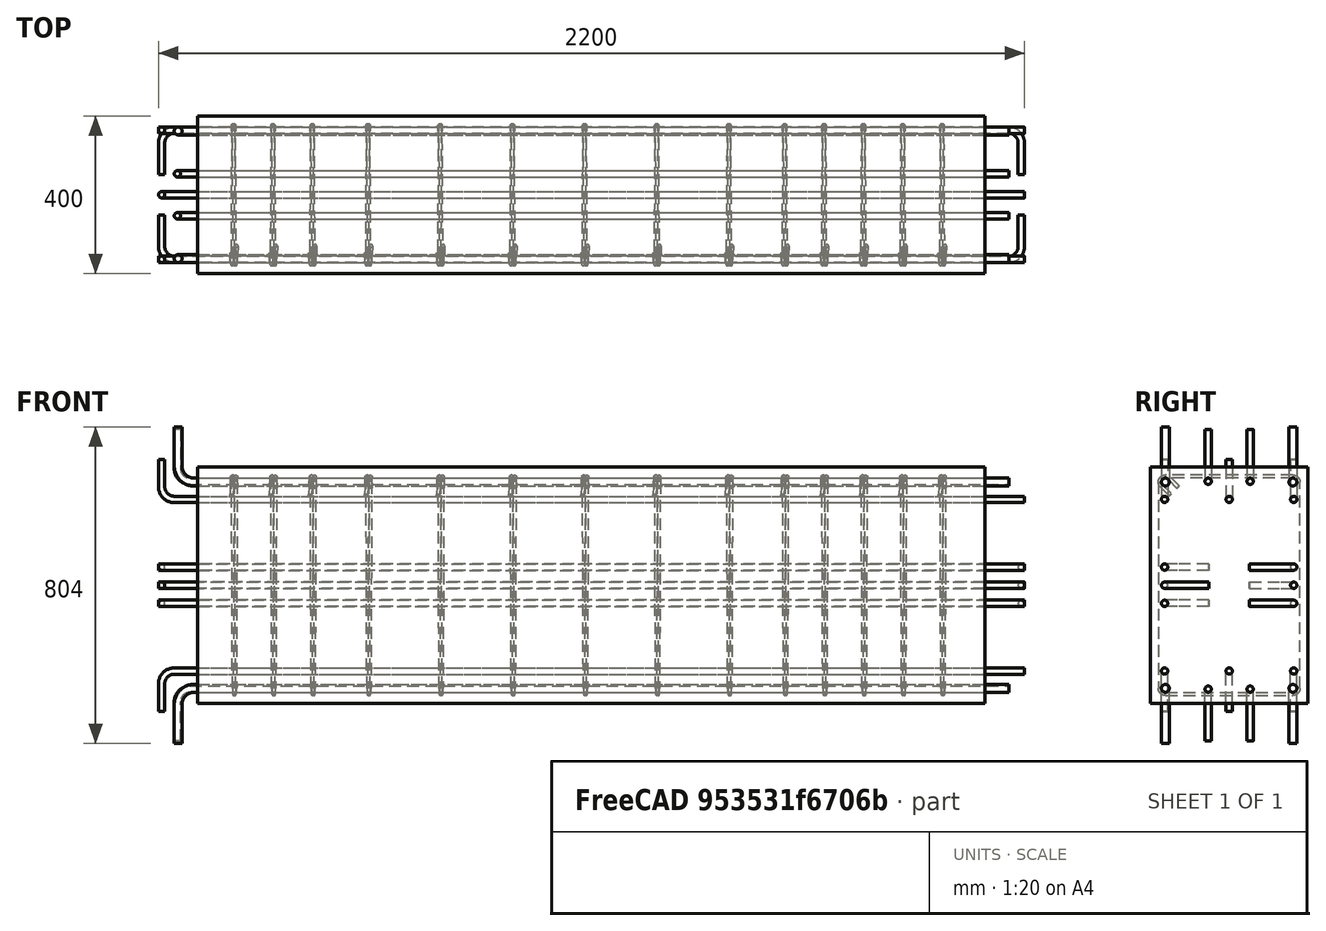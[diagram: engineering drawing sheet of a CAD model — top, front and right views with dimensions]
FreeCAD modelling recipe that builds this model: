
FCSTD DOCUMENT  (FreeCAD 0.19R20802 (Git))
Label: beam_drawing_dimension
License: All rights reserved
LicenseURL: http://en.wikipedia.org/wiki/All_rights_reserved
objects: TechDraw::DrawViewSymbolPython×88, Part::FeaturePython×16, Sketcher::SketchObject×14, App::DocumentObjectGroupPython×7, TechDraw::DrawSVGTemplate×6, TechDraw::DrawPage×6, Part::Part2DObjectPython×1
note: 31 computed .brp shape members not serialized (recipe doc carries the construction recipe); baked Part::Feature solids carry a one-line shape summary decoded from their .brp

FEATURE [Part::FeaturePython] Structure  label="Beam"  # Arch/BIM 7 (typed FeaturePython)
  FaceMaker = 0
  Height = 600
  HorizontalArea = 800000
  IfcData = attributes={"GlobalId": {"name": "GlobalId", "type": "IfcGloballyUniqueId", "is_enum": false, "enum_values": []}, "Description": {"... (+475 chars omitted),+1 more (map truncated)
  IfcType = 7
  Length = 2000
  MoveBase = false
  MoveWithHost = false
  Nodes = (2) [(0,0,1.11022e-15),(0,0,2000)]
  NodesOffset = 0
  Normal = (0,0,0)
  PerimeterLength = 4800
  PredefinedType = 0
  VerticalArea = 2880000
  Width = 400
FEATURE [Part::Part2DObjectPython] Wire  # Draft 2D object (typed FeaturePython)
  Area = 0
  ChamferSize = 0
  Closed = false
  End = (1989.44,-149.272,229.473)
  FilletRadius = 0
  Length = 1979.28
  MakeFace = true
  Points = (7) [(2002.11,-129.473,249.272),(2000,-176,295.799),(1997.89,-176,-276),(1995.78,176,-276),(1993.66,176,276),(1991.55,-195.799,276),(1989.44,-149.272,229.473)]
  Start = (2002.11,-129.473,249.272)
  Subdivisions = 0
  Support = -> [Structure]
FEATURE [Part::FeaturePython] Rebar  label="Stirrup"  # Arch/BIM 110 (typed FeaturePython)
  Amount = 14
  AmountCheck = false
  Base = -> Wire
  BentAngle = 135
  BentFactor = 4
  BottomCover = 20
  CustomSpacing = 5@100.0+6@183.33333333333334+3@100.0
  Diameter = 8
  Direction = (-1,0,0)
  Distance = 0
  FrontCover = 100
  HorizontalArea = 0
  Host = -> Structure
  IfcType = 110
  LeftCover = 20
  Length = 1979.28
  Mark = STRP
  MoveBase = false
  MoveWithHost = false
  OffsetEnd = 104
  OffsetStart = 104
  PerimeterLength = 0
  PlacementList = 14 placements: [(-104,0,0),(-204,0,0),(-304,0,0),(-404,0,0),(-504,0,0),(-645.667,0,0),(-829,0,0),(-1012.33,0,0),(-1195.67,0,0),(-1379,0,0),(-1562.33,0,0),(-1704,0,0),(-1804,0,0),(-1904,0,0)]
  RebarShape = 3
  RightCover = 20
  Rounding = 1.75
  Spacing = 0
  TopCover = 20
  TotalLength = 27710
  TrueSpacing = 100
  VerticalArea = 0
FEATURE [App::DocumentObjectGroupPython] Stirrups  # scripted group (container) (typed FeaturePython)
  Group = -> [Rebar]
  Stirrups = -> [Rebar]
  StirrupsConfiguration = Two Legged Stirrups
FEATURE [Sketcher::SketchObject] Sketch
  MapMode = 5
  Placement = pos=(0,-200,0) rot=(1,0,0;1.5708rad)
  Support = -> [Structure]
  sketch-geometry (2):
    g0: LineSegment StartX=-50 StartY=402 StartZ=0 EndX=-50 EndY=262 EndZ=0
    g1: LineSegment StartX=-50 StartY=262 StartZ=0 EndX=2060 EndY=262 EndZ=0
FEATURE [Part::FeaturePython] Rebar001  label="LShapeRebar"  # Arch/BIM 110 (typed FeaturePython)
  Amount = 1
  AmountCheck = true
  Base = -> Sketch
  BottomCover = 702
  Diameter = 20
  Direction = (0,0,0)
  Distance = 0
  FrontCover = 28
  HorizontalArea = 0
  Host = -> Structure
  IfcType = 110
  LeftCover = -60
  Length = 2250
  Mark = TLRb
  MoveBase = false
  MoveWithHost = false
  OffsetEnd = 38
  OffsetStart = 38
  Orientation = Top Left
  PerimeterLength = 0
  PlacementList = 1 placements: [(0,38,-8.43769e-15)]
  RebarShape = 2
  RightCover = -60
  Rounding = 2
  Spacing = 0
  TopCover = 28
  TotalLength = 2250
  TrueSpacing = 1
  VerticalArea = 0
FEATURE [Sketcher::SketchObject] Sketch001
  MapMode = 5
  Placement = pos=(0,-200,0) rot=(1,0,0;1.5708rad)
  Support = -> [Structure]
  sketch-geometry (2):
    g0: LineSegment StartX=-52 StartY=396 StartZ=0 EndX=-52 EndY=264 EndZ=0
    g1: LineSegment StartX=-52 StartY=264 StartZ=0 EndX=2060 EndY=264 EndZ=0
FEATURE [Part::FeaturePython] Rebar002  label="LShapeRebar001"  # Arch/BIM 110 (typed FeaturePython)
  Amount = 2
  AmountCheck = true
  Base = -> Sketch001
  BottomCover = 696
  Diameter = 16
  Direction = (0,0,0)
  Distance = 0
  FrontCover = 138.667
  HorizontalArea = 0
  Host = -> Structure
  IfcType = 110
  LeftCover = -60
  Length = 2244
  Mark = TLRb
  MoveBase = false
  MoveWithHost = false
  OffsetEnd = 146.667
  OffsetStart = 146.667
  Orientation = Top Left
  PerimeterLength = 0
  PlacementList = 2 placements: [(0,146.667,-3.25665e-14),(0,253.333,-5.62513e-14)]
  RebarShape = 2
  RightCover = -60
  Rounding = 2
  Spacing = 106.667
  TopCover = 28
  TotalLength = 4488
  TrueSpacing = 2
  VerticalArea = 0
FEATURE [Sketcher::SketchObject] Sketch002
  MapMode = 5
  Placement = pos=(0,-200,0) rot=(1,0,0;1.5708rad)
  Support = -> [Structure]
  sketch-geometry (2):
    g0: LineSegment StartX=-50 StartY=402 StartZ=0 EndX=-50 EndY=262 EndZ=0
    g1: LineSegment StartX=-50 StartY=262 StartZ=0 EndX=2060 EndY=262 EndZ=0
FEATURE [Part::FeaturePython] Rebar003  label="LShapeRebar002"  # Arch/BIM 110 (typed FeaturePython)
  Amount = 1
  AmountCheck = true
  Base = -> Sketch002
  BottomCover = 702
  Diameter = 20
  Direction = (0,0,0)
  Distance = 0
  FrontCover = 352
  HorizontalArea = 0
  Host = -> Structure
  IfcType = 110
  LeftCover = -60
  Length = 2250
  Mark = TLRb
  MoveBase = false
  MoveWithHost = false
  OffsetEnd = 362
  OffsetStart = 362
  Orientation = Top Left
  PerimeterLength = 0
  PlacementList = 1 placements: [(0,362,-8.03801e-14)]
  RebarShape = 2
  RightCover = -60
  Rounding = 2
  Spacing = 0
  TopCover = 28
  TotalLength = 2250
  TrueSpacing = 1
  VerticalArea = 0
FEATURE [Sketcher::SketchObject] Sketch003
  MapMode = 5
  Placement = pos=(0,-200,0) rot=(1,0,0;1.5708rad)
  Support = -> [Structure]
  sketch-geometry (2):
    g0: LineSegment StartX=-92 StartY=320 StartZ=0 EndX=-92 EndY=218 EndZ=0
    g1: LineSegment StartX=-92 StartY=218 StartZ=0 EndX=2100 EndY=218 EndZ=0
FEATURE [Part::FeaturePython] Rebar004  label="LShapeRebar003"  # Arch/BIM 110 (typed FeaturePython)
  Amount = 3
  AmountCheck = true
  Base = -> Sketch003
  BottomCover = 620
  Diameter = 16
  Direction = (0,0,0)
  Distance = 0
  FrontCover = 28
  HorizontalArea = 0
  Host = -> Structure
  IfcType = 110
  LeftCover = -100
  Length = 2294
  Mark = TLRb
  MoveBase = false
  MoveWithHost = false
  OffsetEnd = 36
  OffsetStart = 36
  Orientation = Top Left
  PerimeterLength = 0
  PlacementList = 3 placements: arithmetic series from (0,36,-7.99361e-15) step (0,164,-3.64153e-14) to (0,364,-8.08242e-14)
  RebarShape = 2
  RightCover = -100
  Rounding = 2
  Spacing = 164
  TopCover = 74
  TotalLength = 6882
  TrueSpacing = 3
  VerticalArea = 0
FEATURE [App::DocumentObjectGroupPython] TopReinforcement  # scripted group (container) (typed FeaturePython)
  Group = -> [Rebar001,Rebar002,Rebar003,Rebar004]
  HookExtension = [(100.0, 100.0, 100.0), (100.0,)]
  HookOrientation = [('Rear Outside', 'Rear Outside', 'Rear Outside'), ('Rear Outside',)]
  LRebarRounding = [(2, 2, 2), (2,)]
  LayerSpacing = [30,30]
  NumberDiameterOffset = 1#20@-60+2#16@-60+1#20@-60 | 3#16@-100
  RebarType = [('LShapeRebar', 'LShapeRebar', 'LShapeRebar'), ('LShapeRebar',)]
  TopRebars = -> [Rebar001,Rebar002,Rebar003,Rebar004]
FEATURE [Sketcher::SketchObject] Sketch004
  MapMode = 5
  Placement = pos=(0,-200,0) rot=(1,0,0;1.5708rad)
  Support = -> [Structure]
  sketch-geometry (2):
    g0: LineSegment StartX=-50 StartY=-402 StartZ=0 EndX=-50 EndY=-262 EndZ=0
    g1: LineSegment StartX=-50 StartY=-262 StartZ=0 EndX=2060 EndY=-262 EndZ=0
FEATURE [Part::FeaturePython] Rebar005  label="LShapeRebar004"  # Arch/BIM 110 (typed FeaturePython)
  Amount = 1
  AmountCheck = true
  Base = -> Sketch004
  BottomCover = 28
  Diameter = 20
  Direction = (0,0,0)
  Distance = 0
  FrontCover = 28
  HorizontalArea = 0
  Host = -> Structure
  IfcType = 110
  LeftCover = -60
  Length = 2250
  Mark = BLRb
  MoveBase = false
  MoveWithHost = false
  OffsetEnd = 38
  OffsetStart = 38
  Orientation = Bottom Left
  PerimeterLength = 0
  PlacementList = 1 placements: [(0,38,-8.43769e-15)]
  RebarShape = 2
  RightCover = -60
  Rounding = 2
  Spacing = 0
  TopCover = 702
  TotalLength = 2250
  TrueSpacing = 1
  VerticalArea = 0
FEATURE [Sketcher::SketchObject] Sketch005
  MapMode = 5
  Placement = pos=(0,-200,0) rot=(1,0,0;1.5708rad)
  Support = -> [Structure]
  sketch-geometry (2):
    g0: LineSegment StartX=-52 StartY=-396 StartZ=0 EndX=-52 EndY=-264 EndZ=0
    g1: LineSegment StartX=-52 StartY=-264 StartZ=0 EndX=2060 EndY=-264 EndZ=0
FEATURE [Part::FeaturePython] Rebar006  label="LShapeRebar005"  # Arch/BIM 110 (typed FeaturePython)
  Amount = 2
  AmountCheck = true
  Base = -> Sketch005
  BottomCover = 28
  Diameter = 16
  Direction = (0,0,0)
  Distance = 0
  FrontCover = 138.667
  HorizontalArea = 0
  Host = -> Structure
  IfcType = 110
  LeftCover = -60
  Length = 2244
  Mark = BLRb
  MoveBase = false
  MoveWithHost = false
  OffsetEnd = 146.667
  OffsetStart = 146.667
  Orientation = Bottom Left
  PerimeterLength = 0
  PlacementList = 2 placements: [(0,146.667,-3.25665e-14),(0,253.333,-5.62513e-14)]
  RebarShape = 2
  RightCover = -60
  Rounding = 2
  Spacing = 106.667
  TopCover = 696
  TotalLength = 4488
  TrueSpacing = 2
  VerticalArea = 0
FEATURE [Sketcher::SketchObject] Sketch006
  MapMode = 5
  Placement = pos=(0,-200,0) rot=(1,0,0;1.5708rad)
  Support = -> [Structure]
  sketch-geometry (2):
    g0: LineSegment StartX=-50 StartY=-402 StartZ=0 EndX=-50 EndY=-262 EndZ=0
    g1: LineSegment StartX=-50 StartY=-262 StartZ=0 EndX=2060 EndY=-262 EndZ=0
FEATURE [Part::FeaturePython] Rebar007  label="LShapeRebar006"  # Arch/BIM 110 (typed FeaturePython)
  Amount = 1
  AmountCheck = true
  Base = -> Sketch006
  BottomCover = 28
  Diameter = 20
  Direction = (0,0,0)
  Distance = 0
  FrontCover = 352
  HorizontalArea = 0
  Host = -> Structure
  IfcType = 110
  LeftCover = -60
  Length = 2250
  Mark = BLRb
  MoveBase = false
  MoveWithHost = false
  OffsetEnd = 362
  OffsetStart = 362
  Orientation = Bottom Left
  PerimeterLength = 0
  PlacementList = 1 placements: [(0,362,-8.03801e-14)]
  RebarShape = 2
  RightCover = -60
  Rounding = 2
  Spacing = 0
  TopCover = 702
  TotalLength = 2250
  TrueSpacing = 1
  VerticalArea = 0
FEATURE [Sketcher::SketchObject] Sketch007
  MapMode = 5
  Placement = pos=(0,-200,0) rot=(1,0,0;1.5708rad)
  Support = -> [Structure]
  sketch-geometry (2):
    g0: LineSegment StartX=-92 StartY=-320 StartZ=0 EndX=-92 EndY=-218 EndZ=0
    g1: LineSegment StartX=-92 StartY=-218 StartZ=0 EndX=2100 EndY=-218 EndZ=0
FEATURE [Part::FeaturePython] Rebar008  label="LShapeRebar007"  # Arch/BIM 110 (typed FeaturePython)
  Amount = 3
  AmountCheck = true
  Base = -> Sketch007
  BottomCover = 74
  Diameter = 16
  Direction = (0,0,0)
  Distance = 0
  FrontCover = 28
  HorizontalArea = 0
  Host = -> Structure
  IfcType = 110
  LeftCover = -100
  Length = 2294
  Mark = BLRb
  MoveBase = false
  MoveWithHost = false
  OffsetEnd = 36
  OffsetStart = 36
  Orientation = Bottom Left
  PerimeterLength = 0
  PlacementList = 3 placements: arithmetic series from (0,36,-7.99361e-15) step (0,164,-3.64153e-14) to (0,364,-8.08242e-14)
  RebarShape = 2
  RightCover = -100
  Rounding = 2
  Spacing = 164
  TopCover = 620
  TotalLength = 6882
  TrueSpacing = 3
  VerticalArea = 0
FEATURE [App::DocumentObjectGroupPython] BottomReinforcement  # scripted group (container) (typed FeaturePython)
  BottomRebars = -> [Rebar005,Rebar006,Rebar007,Rebar008]
  Group = -> [Rebar005,Rebar006,Rebar007,Rebar008]
  HookExtension = [(100.0, 100.0, 100.0), (100.0,)]
  HookOrientation = [('Rear Outside', 'Rear Outside', 'Rear Outside'), ('Rear Outside',)]
  LRebarRounding = [(2, 2, 2), (2,)]
  LayerSpacing = [30,30]
  NumberDiameterOffset = 1#20@-60+2#16@-60+1#20@-60 | 3#16@-100
  RebarType = [('LShapeRebar', 'LShapeRebar', 'LShapeRebar'), ('LShapeRebar',)]
FEATURE [Sketcher::SketchObject] Sketch008
  MapMode = 5
  Placement = pos=(6.6e-14,0,-300) rot=(1,0,0;3.14159rad)
  Support = -> [Structure]
  sketch-geometry (2):
    g0: LineSegment StartX=-92 StartY=52 StartZ=0 EndX=-92 EndY=164 EndZ=0
    g1: LineSegment StartX=-92 StartY=164 StartZ=0 EndX=2100 EndY=164 EndZ=0
FEATURE [Part::FeaturePython] Rebar009  label="LShapeRebar008"  # Arch/BIM 110 (typed FeaturePython)
  Amount = 1
  AmountCheck = true
  Base = -> Sketch008
  BottomCover = 252
  Diameter = 16
  Direction = (0,0,0)
  Distance = 0
  FrontCover = 246
  HorizontalArea = 0
  Host = -> Structure
  IfcType = 110
  LeftCover = -100
  Length = 2304
  Mark = LLRb
  MoveBase = false
  MoveWithHost = false
  OffsetEnd = 346
  OffsetStart = 254
  Orientation = Top Left
  PerimeterLength = 0
  PlacementList = 1 placements: [(-5.588e-14,0,254)]
  RebarShape = 2
  RightCover = -100
  Rounding = 2
  Spacing = 0
  TopCover = 28
  TotalLength = 2304
  TrueSpacing = 1
  VerticalArea = 0
FEATURE [Sketcher::SketchObject] Sketch009
  MapMode = 5
  Placement = pos=(6.6e-14,0,-300) rot=(1,0,0;3.14159rad)
  Support = -> [Structure]
  sketch-geometry (2):
    g0: LineSegment StartX=2092 StartY=52 StartZ=0 EndX=2092 EndY=164 EndZ=0
    g1: LineSegment StartX=2092 StartY=164 StartZ=0 EndX=-100 EndY=164 EndZ=0
FEATURE [Part::FeaturePython] Rebar010  label="LShapeRebar009"  # Arch/BIM 110 (typed FeaturePython)
  Amount = 1
  AmountCheck = true
  Base = -> Sketch009
  BottomCover = 252
  Diameter = 16
  Direction = (0,0,0)
  Distance = 0
  FrontCover = 292
  HorizontalArea = 0
  Host = -> Structure
  IfcType = 110
  LeftCover = -100
  Length = 2304
  Mark = LLRb
  MoveBase = false
  MoveWithHost = false
  OffsetEnd = 300
  OffsetStart = 300
  Orientation = Top Right
  PerimeterLength = 0
  PlacementList = 1 placements: [(-6.6e-14,0,300)]
  RebarShape = 2
  RightCover = -100
  Rounding = 2
  Spacing = 0
  TopCover = 28
  TotalLength = 2304
  TrueSpacing = 1
  VerticalArea = 0
FEATURE [Sketcher::SketchObject] Sketch010
  MapMode = 5
  Placement = pos=(6.6e-14,0,-300) rot=(1,0,0;3.14159rad)
  Support = -> [Structure]
  sketch-geometry (2):
    g0: LineSegment StartX=-92 StartY=52 StartZ=0 EndX=-92 EndY=164 EndZ=0
    g1: LineSegment StartX=-92 StartY=164 StartZ=0 EndX=2100 EndY=164 EndZ=0
FEATURE [Part::FeaturePython] Rebar011  label="LShapeRebar010"  # Arch/BIM 110 (typed FeaturePython)
  Amount = 1
  AmountCheck = true
  Base = -> Sketch010
  BottomCover = 252
  Diameter = 16
  Direction = (0,0,0)
  Distance = 0
  FrontCover = 338
  HorizontalArea = 0
  Host = -> Structure
  IfcType = 110
  LeftCover = -100
  Length = 2304
  Mark = LLRb
  MoveBase = false
  MoveWithHost = false
  OffsetEnd = 254
  OffsetStart = 346
  Orientation = Top Left
  PerimeterLength = 0
  PlacementList = 1 placements: [(-7.612e-14,0,346)]
  RebarShape = 2
  RightCover = -100
  Rounding = 2
  Spacing = 0
  TopCover = 28
  TotalLength = 2304
  TrueSpacing = 1
  VerticalArea = 0
FEATURE [App::DocumentObjectGroupPython] LeftRebars  # scripted group (container) (typed FeaturePython)
  Group = -> [Rebar009,Rebar010,Rebar011]
  HookExtension = [80,80,80]
  HookOrientation = Rear Inside | Front Inside | Rear Inside
  LRebarRounding = [2,2,2]
  LeftRebars = -> [Rebar009,Rebar010,Rebar011]
  NumberDiameterOffset = 1#16@-100+1#16@-100+1#16@-100
  RebarSpacing = 30
  RebarType = LShapeRebar | LShapeRebar | LShapeRebar
FEATURE [Sketcher::SketchObject] Sketch011
  MapMode = 5
  Placement = pos=(6.6e-14,0,-300) rot=(1,0,0;3.14159rad)
  Support = -> [Structure]
  sketch-geometry (2):
    g0: LineSegment StartX=2092 StartY=-52 StartZ=0 EndX=2092 EndY=-164 EndZ=0
    g1: LineSegment StartX=2092 StartY=-164 StartZ=0 EndX=-100 EndY=-164 EndZ=0
FEATURE [Part::FeaturePython] Rebar012  label="LShapeRebar011"  # Arch/BIM 110 (typed FeaturePython)
  Amount = 1
  AmountCheck = true
  Base = -> Sketch011
  BottomCover = 28
  Diameter = 16
  Direction = (0,0,0)
  Distance = 0
  FrontCover = 246
  HorizontalArea = 0
  Host = -> Structure
  IfcType = 110
  LeftCover = -100
  Length = 2304
  Mark = RLRb
  MoveBase = false
  MoveWithHost = false
  OffsetEnd = 346
  OffsetStart = 254
  Orientation = Bottom Right
  PerimeterLength = 0
  PlacementList = 1 placements: [(-5.588e-14,0,254)]
  RebarShape = 2
  RightCover = -100
  Rounding = 2
  Spacing = 0
  TopCover = 252
  TotalLength = 2304
  TrueSpacing = 1
  VerticalArea = 0
FEATURE [Sketcher::SketchObject] Sketch012
  MapMode = 5
  Placement = pos=(6.6e-14,0,-300) rot=(1,0,0;3.14159rad)
  Support = -> [Structure]
  sketch-geometry (2):
    g0: LineSegment StartX=-92 StartY=-52 StartZ=0 EndX=-92 EndY=-164 EndZ=0
    g1: LineSegment StartX=-92 StartY=-164 StartZ=0 EndX=2100 EndY=-164 EndZ=0
FEATURE [Part::FeaturePython] Rebar013  label="LShapeRebar012"  # Arch/BIM 110 (typed FeaturePython)
  Amount = 1
  AmountCheck = true
  Base = -> Sketch012
  BottomCover = 28
  Diameter = 16
  Direction = (0,0,0)
  Distance = 0
  FrontCover = 292
  HorizontalArea = 0
  Host = -> Structure
  IfcType = 110
  LeftCover = -100
  Length = 2304
  Mark = RLRb
  MoveBase = false
  MoveWithHost = false
  OffsetEnd = 300
  OffsetStart = 300
  Orientation = Bottom Left
  PerimeterLength = 0
  PlacementList = 1 placements: [(-6.6e-14,0,300)]
  RebarShape = 2
  RightCover = -100
  Rounding = 2
  Spacing = 0
  TopCover = 252
  TotalLength = 2304
  TrueSpacing = 1
  VerticalArea = 0
FEATURE [Sketcher::SketchObject] Sketch013
  MapMode = 5
  Placement = pos=(6.6e-14,0,-300) rot=(1,0,0;3.14159rad)
  Support = -> [Structure]
  sketch-geometry (2):
    g0: LineSegment StartX=2092 StartY=-52 StartZ=0 EndX=2092 EndY=-164 EndZ=0
    g1: LineSegment StartX=2092 StartY=-164 StartZ=0 EndX=-100 EndY=-164 EndZ=0
FEATURE [Part::FeaturePython] Rebar014  label="LShapeRebar013"  # Arch/BIM 110 (typed FeaturePython)
  Amount = 1
  AmountCheck = true
  Base = -> Sketch013
  BottomCover = 28
  Diameter = 16
  Direction = (0,0,0)
  Distance = 0
  FrontCover = 338
  HorizontalArea = 0
  Host = -> Structure
  IfcType = 110
  LeftCover = -100
  Length = 2304
  Mark = RLRb
  MoveBase = false
  MoveWithHost = false
  OffsetEnd = 254
  OffsetStart = 346
  Orientation = Bottom Right
  PerimeterLength = 0
  PlacementList = 1 placements: [(-7.612e-14,0,346)]
  RebarShape = 2
  RightCover = -100
  Rounding = 2
  Spacing = 0
  TopCover = 252
  TotalLength = 2304
  TrueSpacing = 1
  VerticalArea = 0
FEATURE [App::DocumentObjectGroupPython] RightRebars  # scripted group (container) (typed FeaturePython)
  Group = -> [Rebar012,Rebar013,Rebar014]
  HookExtension = [80,80,80]
  HookOrientation = Front Inside | Rear Inside | Front Inside
  LRebarRounding = [2,2,2]
  NumberDiameterOffset = 1#16@-100+1#16@-100+1#16@-100
  RebarSpacing = 30
  RebarType = LShapeRebar | LShapeRebar | LShapeRebar
  RightRebars = -> [Rebar012,Rebar013,Rebar014]
FEATURE [App::DocumentObjectGroupPython] ShearReinforcement  # scripted group (container) (typed FeaturePython)
  Group = -> [LeftRebars,RightRebars]
  ShearReinforcementGroups = -> [LeftRebars,RightRebars]
FEATURE [App::DocumentObjectGroupPython] BeamReinforcement  # scripted group (container) (typed FeaturePython)
  Group = -> [Stirrups,TopReinforcement,BottomReinforcement,ShearReinforcement]
  ReinforcementGroups = -> [Stirrups,TopReinforcement,BottomReinforcement,ShearReinforcement]
FEATURE [TechDraw::DrawSVGTemplate] Template
  Height = 210
  Orientation = 1
  Width = 297
FEATURE [TechDraw::DrawViewSymbolPython] ReinforcementDrawingView  label="Front View"  # drawing view (typed FeaturePython)
  DimensionBottomOffset = 40
  DimensionLeftOffset = 10
  DimensionRightOffset = 10
  DimensionTopOffset = 58
  Height = 804
  LeftOffset = 20
  LockPosition = false
  MaxHeight = 210
  MaxWidth = 297
  MinBottomOffset = 20
  MinRightOffset = 20
  PositionType = 0
  Rebars = -> [Rebar,Rebar001,Rebar002,Rebar003,Rebar004,Rebar005,Rebar006,Rebar007,Rebar008,Rebar009,Rebar010,Rebar011,Rebar012,Rebar013,Rebar014]
  RebarsColorStyle = 0
  RebarsStrokeWidth = 0.35
  Rotation = 0
  Scale = 0.116818
  ScaleType = 1
  Structure = -> Structure
  StructureColorStyle = 0
  StructureStrokeWidth = 0.5
  Symbol = <blob: 8325 chars omitted>
  Template = -> Template
  TopOffset = 58.0391
  View = 0
  VisibleRebars = -> [Rebar,Rebar001,Rebar002,Rebar004,Rebar005,Rebar006,Rebar008,Rebar009,Rebar010,Rebar011,Rebar012,Rebar013,Rebar014]
  Width = 2200
  X = 148.5
  Y = 105
  expr: TopOffset = .Template.Height.Value / 2 - .Height.Value * .Scale / 2
  expr: LeftOffset = .Template.Width.Value / 2 - .Width.Value * .Scale / 2
FEATURE [TechDraw::DrawViewSymbolPython] ReinforcementDimensioning  # drawing view (typed FeaturePython)
  DimensionBottomOffset = 10
  DimensionFormat = %M %C⌀%D,span=%S
  DimensionLeftOffset = 10
  DimensionRightOffset = 10
  DimensionTopOffset = 10
  Font = DejaVu Sans
  FontSize = 3
  LineEndSymbol = 0
  LineMidPointSymbol = 1
  LineStartSymbol = 3
  LineStyle = 0
  LockPosition = false
  MultiRebar_LineEndSymbol = 0
  MultiRebar_LineStartSymbol = 0
  MultiRebar_OuterDimension = true
  MultiRebar_TextPositionType = 0
  ParentDrawingView = -> ReinforcementDrawingView
  Rebar = -> Rebar
  Rotation = 0
  Scale = 0.116818
  ScaleType = 2
  SingleRebar_LineEndSymbol = 0
  SingleRebar_LineStartSymbol = 3
  SingleRebar_OuterDimension = false
  SingleRebar_TextPositionType = 1
  StrokeWidth = 0.25
  Symbol = <blob: 5914 chars omitted>
  TextPositionType = 0
  WayPoints = (2) [(0,0,0),(50,0,0)]
  WayPointsType = 0
  X = 148.5
  Y = 105
FEATURE [TechDraw::DrawViewSymbolPython] ReinforcementDimensioning001  # drawing view (typed FeaturePython)
  DimensionBottomOffset = 10
  DimensionFormat = %M %C⌀%D,span=%S
  DimensionLeftOffset = 10
  DimensionRightOffset = 10
  DimensionTopOffset = 16
  Font = DejaVu Sans
  FontSize = 3
  LineEndSymbol = 0
  LineMidPointSymbol = 1
  LineStartSymbol = 3
  LineStyle = 0
  LockPosition = false
  MultiRebar_LineEndSymbol = 0
  MultiRebar_LineStartSymbol = 0
  MultiRebar_OuterDimension = true
  MultiRebar_TextPositionType = 0
  ParentDrawingView = -> ReinforcementDrawingView
  Rebar = -> Rebar001
  Rotation = 0
  Scale = 0.116818
  ScaleType = 2
  SingleRebar_LineEndSymbol = 0
  SingleRebar_LineStartSymbol = 3
  SingleRebar_OuterDimension = false
  SingleRebar_TextPositionType = 1
  StrokeWidth = 0.25
  Symbol = <svg version="1.1" xmlns="http://www.w3.org/2000/svg" xmlns:xlink="http://www.w3.org/1999/xlink" xmlns:freecad="http://www.freecadweb.org/wiki/index.php?title=Svg_Namespace" width="2200.0mm" height="804.0mm" viewBox="0 0 2200.0 804.0"><g transform="translate(100.00000000000023, 402.0000000000002)"><g><path d="M1197.0 -538.9649805447473 L1197.0 -262.0000000000002" style="stroke:#00007f;stroke-width:2.140077821011673;stroke-linecap:round;fill:none;" stroke-dasharray="" /><g id="line_mid_points" /><path d="M0,0 -8,-1.5 V1.5 L0,0" style="stroke:#00007f;fill:#00007f;stroke-width:2.140077821011673;stroke-linecap:round;stroke-linejoin:bevel;" transform="translate(1197.0 -262.0000000000002) rotate(90.0 0 0)" /></g><text x="1197.0" y="-538.9649805447473" style="white-space:pre;" fill="#005400" font-family="DejaVu Sans" font-size="25.68093385214008" text-anchor="middle" dominant-baseline="baseline" xml:space="preserve">TLRb 1⌀20,span=0</text></g></svg>
  TextPositionType = 0
  WayPoints = (2) [(0,0,0),(50,0,0)]
  WayPointsType = 0
  X = 148.5
  Y = 105
FEATURE [TechDraw::DrawViewSymbolPython] ReinforcementDimensioning002  # drawing view (typed FeaturePython)
  DimensionBottomOffset = 10
  DimensionFormat = %M %C⌀%D,span=%S
  DimensionLeftOffset = 10
  DimensionRightOffset = 10
  DimensionTopOffset = 22
  Font = DejaVu Sans
  FontSize = 3
  LineEndSymbol = 0
  LineMidPointSymbol = 1
  LineStartSymbol = 3
  LineStyle = 0
  LockPosition = false
  MultiRebar_LineEndSymbol = 0
  MultiRebar_LineStartSymbol = 0
  MultiRebar_OuterDimension = true
  MultiRebar_TextPositionType = 0
  ParentDrawingView = -> ReinforcementDrawingView
  Rebar = -> Rebar002
  Rotation = 0
  Scale = 0.116818
  ScaleType = 2
  SingleRebar_LineEndSymbol = 0
  SingleRebar_LineStartSymbol = 3
  SingleRebar_OuterDimension = false
  SingleRebar_TextPositionType = 1
  StrokeWidth = 0.25
  Symbol = <svg version="1.1" xmlns="http://www.w3.org/2000/svg" xmlns:xlink="http://www.w3.org/1999/xlink" xmlns:freecad="http://www.freecadweb.org/wiki/index.php?title=Svg_Namespace" width="2200.0mm" height="804.0mm" viewBox="0 0 2200.0 804.0"><g transform="translate(100.00000000000023, 402.0000000000002)"><g><path d="M1213.0 -590.3268482490274 L1213.0 -264.00000000000017" style="stroke:#00007f;stroke-width:2.140077821011673;stroke-linecap:round;fill:none;" stroke-dasharray="" /><g id="line_mid_points" /><path d="M0,0 -8,-1.5 V1.5 L0,0" style="stroke:#00007f;fill:#00007f;stroke-width:2.140077821011673;stroke-linecap:round;stroke-linejoin:bevel;" transform="translate(1213.0 -264.00000000000017) rotate(90.0 0 0)" /></g><text x="1213.0" y="-590.3268482490274" style="white-space:pre;" fill="#005400" font-family="DejaVu Sans" font-size="25.68093385214008" text-anchor="middle" dominant-baseline="baseline" xml:space="preserve">TLRb 2⌀16,span=107</text></g></svg>
  TextPositionType = 0
  WayPoints = (2) [(0,0,0),(50,0,0)]
  WayPointsType = 0
  X = 148.5
  Y = 105
FEATURE [TechDraw::DrawViewSymbolPython] ReinforcementDimensioning003  # drawing view (typed FeaturePython)
  DimensionBottomOffset = 10
  DimensionFormat = %M %C⌀%D,span=%S
  DimensionLeftOffset = 10
  DimensionRightOffset = 10
  DimensionTopOffset = 28
  Font = DejaVu Sans
  FontSize = 3
  LineEndSymbol = 0
  LineMidPointSymbol = 1
  LineStartSymbol = 3
  LineStyle = 0
  LockPosition = false
  MultiRebar_LineEndSymbol = 0
  MultiRebar_LineStartSymbol = 0
  MultiRebar_OuterDimension = true
  MultiRebar_TextPositionType = 0
  ParentDrawingView = -> ReinforcementDrawingView
  Rebar = -> Rebar004
  Rotation = 0
  Scale = 0.116818
  ScaleType = 2
  SingleRebar_LineEndSymbol = 0
  SingleRebar_LineStartSymbol = 3
  SingleRebar_OuterDimension = false
  SingleRebar_TextPositionType = 1
  StrokeWidth = 0.25
  Symbol = <svg version="1.1" xmlns="http://www.w3.org/2000/svg" xmlns:xlink="http://www.w3.org/1999/xlink" xmlns:freecad="http://www.freecadweb.org/wiki/index.php?title=Svg_Namespace" width="2200.0mm" height="804.0mm" viewBox="0 0 2200.0 804.0"><g transform="translate(100.00000000000023, 402.0000000000002)"><g><path d="M1938.0 -641.6887159533076 L1938.0 -218.00000000000023" style="stroke:#00007f;stroke-width:2.140077821011673;stroke-linecap:round;fill:none;" stroke-dasharray="" /><g id="line_mid_points" /><path d="M0,0 -8,-1.5 V1.5 L0,0" style="stroke:#00007f;fill:#00007f;stroke-width:2.140077821011673;stroke-linecap:round;stroke-linejoin:bevel;" transform="translate(1938.0 -218.00000000000023) rotate(90.0 0 0)" /></g><text x="1938.0" y="-641.6887159533076" style="white-space:pre;" fill="#005400" font-family="DejaVu Sans" font-size="25.68093385214008" text-anchor="middle" dominant-baseline="baseline" xml:space="preserve">TLRb 3⌀16,span=328</text></g></svg>
  TextPositionType = 0
  WayPoints = (2) [(0,0,0),(50,0,0)]
  WayPointsType = 0
  X = 148.5
  Y = 105
FEATURE [TechDraw::DrawViewSymbolPython] ReinforcementDimensioning004  # drawing view (typed FeaturePython)
  DimensionBottomOffset = 10
  DimensionFormat = %M %C⌀%D,span=%S
  DimensionLeftOffset = 10
  DimensionRightOffset = 10
  DimensionTopOffset = 34
  Font = DejaVu Sans
  FontSize = 3
  LineEndSymbol = 0
  LineMidPointSymbol = 1
  LineStartSymbol = 3
  LineStyle = 0
  LockPosition = false
  MultiRebar_LineEndSymbol = 0
  MultiRebar_LineStartSymbol = 0
  MultiRebar_OuterDimension = true
  MultiRebar_TextPositionType = 0
  ParentDrawingView = -> ReinforcementDrawingView
  Rebar = -> Rebar005
  Rotation = 0
  Scale = 0.116818
  ScaleType = 2
  SingleRebar_LineEndSymbol = 0
  SingleRebar_LineStartSymbol = 3
  SingleRebar_OuterDimension = false
  SingleRebar_TextPositionType = 1
  StrokeWidth = 0.25
  Symbol = <svg version="1.1" xmlns="http://www.w3.org/2000/svg" xmlns:xlink="http://www.w3.org/1999/xlink" xmlns:freecad="http://www.freecadweb.org/wiki/index.php?title=Svg_Namespace" width="2200.0mm" height="804.0mm" viewBox="0 0 2200.0 804.0"><g transform="translate(100.00000000000023, 402.0000000000002)"><g><path d="M319.0 487.60311284046674 L319.0 261.9999999999998" style="stroke:#00007f;stroke-width:2.140077821011673;stroke-linecap:round;fill:none;" stroke-dasharray="" /><g id="line_mid_points" /><path d="M0,0 -8,-1.5 V1.5 L0,0" style="stroke:#00007f;fill:#00007f;stroke-width:2.140077821011673;stroke-linecap:round;stroke-linejoin:bevel;" transform="translate(319.0 261.9999999999998) rotate(-90.0 0 0)" /></g><text x="319.0" y="500.4435797665368" style="white-space:pre;" fill="#005400" font-family="DejaVu Sans" font-size="25.68093385214008" text-anchor="middle" dominant-baseline="baseline" xml:space="preserve">BLRb 1⌀20,span=0</text></g></svg>
  TextPositionType = 0
  WayPoints = (2) [(0,0,0),(50,0,0)]
  WayPointsType = 0
  X = 148.5
  Y = 105
FEATURE [TechDraw::DrawViewSymbolPython] ReinforcementDimensioning005  # drawing view (typed FeaturePython)
  DimensionBottomOffset = 16
  DimensionFormat = %M %C⌀%D,span=%S
  DimensionLeftOffset = 10
  DimensionRightOffset = 10
  DimensionTopOffset = 34
  Font = DejaVu Sans
  FontSize = 3
  LineEndSymbol = 0
  LineMidPointSymbol = 1
  LineStartSymbol = 3
  LineStyle = 0
  LockPosition = false
  MultiRebar_LineEndSymbol = 0
  MultiRebar_LineStartSymbol = 0
  MultiRebar_OuterDimension = true
  MultiRebar_TextPositionType = 0
  ParentDrawingView = -> ReinforcementDrawingView
  Rebar = -> Rebar006
  Rotation = 0
  Scale = 0.116818
  ScaleType = 2
  SingleRebar_LineEndSymbol = 0
  SingleRebar_LineStartSymbol = 3
  SingleRebar_OuterDimension = false
  SingleRebar_TextPositionType = 1
  StrokeWidth = 0.25
  Symbol = <svg version="1.1" xmlns="http://www.w3.org/2000/svg" xmlns:xlink="http://www.w3.org/1999/xlink" xmlns:freecad="http://www.freecadweb.org/wiki/index.php?title=Svg_Namespace" width="2200.0mm" height="804.0mm" viewBox="0 0 2200.0 804.0"><g transform="translate(100.00000000000023, 402.0000000000002)"><g><path d="M1466.0 538.9649805447469 L1466.0 263.99999999999983" style="stroke:#00007f;stroke-width:2.140077821011673;stroke-linecap:round;fill:none;" stroke-dasharray="" /><g id="line_mid_points" /><path d="M0,0 -8,-1.5 V1.5 L0,0" style="stroke:#00007f;fill:#00007f;stroke-width:2.140077821011673;stroke-linecap:round;stroke-linejoin:bevel;" transform="translate(1466.0 263.99999999999983) rotate(-90.0 0 0)" /></g><text x="1466.0" y="551.805447470817" style="white-space:pre;" fill="#005400" font-family="DejaVu Sans" font-size="25.68093385214008" text-anchor="middle" dominant-baseline="baseline" xml:space="preserve">BLRb 2⌀16,span=107</text></g></svg>
  TextPositionType = 0
  WayPoints = (2) [(0,0,0),(50,0,0)]
  WayPointsType = 0
  X = 148.5
  Y = 105
FEATURE [TechDraw::DrawViewSymbolPython] ReinforcementDimensioning006  # drawing view (typed FeaturePython)
  DimensionBottomOffset = 22
  DimensionFormat = %M %C⌀%D,span=%S
  DimensionLeftOffset = 10
  DimensionRightOffset = 10
  DimensionTopOffset = 34
  Font = DejaVu Sans
  FontSize = 3
  LineEndSymbol = 0
  LineMidPointSymbol = 1
  LineStartSymbol = 3
  LineStyle = 0
  LockPosition = false
  MultiRebar_LineEndSymbol = 0
  MultiRebar_LineStartSymbol = 0
  MultiRebar_OuterDimension = true
  MultiRebar_TextPositionType = 0
  ParentDrawingView = -> ReinforcementDrawingView
  Rebar = -> Rebar008
  Rotation = 0
  Scale = 0.116818
  ScaleType = 2
  SingleRebar_LineEndSymbol = 0
  SingleRebar_LineStartSymbol = 3
  SingleRebar_OuterDimension = false
  SingleRebar_TextPositionType = 1
  StrokeWidth = 0.25
  Symbol = <svg version="1.1" xmlns="http://www.w3.org/2000/svg" xmlns:xlink="http://www.w3.org/1999/xlink" xmlns:freecad="http://www.freecadweb.org/wiki/index.php?title=Svg_Namespace" width="2200.0mm" height="804.0mm" viewBox="0 0 2200.0 804.0"><g transform="translate(100.00000000000023, 402.0000000000002)"><g><path d="M1960.0 590.3268482490271 L1960.0 217.99999999999977" style="stroke:#00007f;stroke-width:2.140077821011673;stroke-linecap:round;fill:none;" stroke-dasharray="" /><g id="line_mid_points" /><path d="M0,0 -8,-1.5 V1.5 L0,0" style="stroke:#00007f;fill:#00007f;stroke-width:2.140077821011673;stroke-linecap:round;stroke-linejoin:bevel;" transform="translate(1960.0 217.99999999999977) rotate(-90.0 0 0)" /></g><text x="1960.0" y="603.1673151750971" style="white-space:pre;" fill="#005400" font-family="DejaVu Sans" font-size="25.68093385214008" text-anchor="middle" dominant-baseline="baseline" xml:space="preserve">BLRb 3⌀16,span=328</text></g></svg>
  TextPositionType = 0
  WayPoints = (2) [(0,0,0),(50,0,0)]
  WayPointsType = 0
  X = 148.5
  Y = 105
FEATURE [TechDraw::DrawViewSymbolPython] ReinforcementDimensioning007  # drawing view (typed FeaturePython)
  DimensionBottomOffset = 28
  DimensionFormat = %M %C⌀%D,span=%S
  DimensionLeftOffset = 10
  DimensionRightOffset = 10
  DimensionTopOffset = 34
  Font = DejaVu Sans
  FontSize = 3
  LineEndSymbol = 0
  LineMidPointSymbol = 1
  LineStartSymbol = 3
  LineStyle = 0
  LockPosition = false
  MultiRebar_LineEndSymbol = 0
  MultiRebar_LineStartSymbol = 0
  MultiRebar_OuterDimension = true
  MultiRebar_TextPositionType = 0
  ParentDrawingView = -> ReinforcementDrawingView
  Rebar = -> Rebar009
  Rotation = 0
  Scale = 0.116818
  ScaleType = 2
  SingleRebar_LineEndSymbol = 0
  SingleRebar_LineStartSymbol = 3
  SingleRebar_OuterDimension = false
  SingleRebar_TextPositionType = 1
  StrokeWidth = 0.25
  Symbol = <svg version="1.1" xmlns="http://www.w3.org/2000/svg" xmlns:xlink="http://www.w3.org/1999/xlink" xmlns:freecad="http://www.freecadweb.org/wiki/index.php?title=Svg_Namespace" width="2200.0mm" height="804.0mm" viewBox="0 0 2200.0 804.0"><g transform="translate(100.00000000000023, 402.0000000000002)"><g><path d="M18.0 641.6887159533072 L18.0 45.99999999999998" style="stroke:#00007f;stroke-width:2.140077821011673;stroke-linecap:round;fill:none;" stroke-dasharray="" /><g id="line_mid_points" /><path d="M0,0 -8,-1.5 V1.5 L0,0" style="stroke:#00007f;fill:#00007f;stroke-width:2.140077821011673;stroke-linecap:round;stroke-linejoin:bevel;" transform="translate(18.0 45.99999999999998) rotate(-90.0 0 0)" /></g><text x="18.0" y="654.5291828793772" style="white-space:pre;" fill="#005400" font-family="DejaVu Sans" font-size="25.68093385214008" text-anchor="middle" dominant-baseline="baseline" xml:space="preserve">LLRb 1⌀16,span=0</text></g></svg>
  TextPositionType = 0
  WayPoints = (2) [(0,0,0),(50,0,0)]
  WayPointsType = 0
  X = 148.5
  Y = 105
FEATURE [TechDraw::DrawViewSymbolPython] ReinforcementDimensioning008  # drawing view (typed FeaturePython)
  DimensionBottomOffset = 34
  DimensionFormat = %M %C⌀%D,span=%S
  DimensionLeftOffset = 10
  DimensionRightOffset = 10
  DimensionTopOffset = 34
  Font = DejaVu Sans
  FontSize = 3
  LineEndSymbol = 0
  LineMidPointSymbol = 1
  LineStartSymbol = 3
  LineStyle = 0
  LockPosition = false
  MultiRebar_LineEndSymbol = 0
  MultiRebar_LineStartSymbol = 0
  MultiRebar_OuterDimension = true
  MultiRebar_TextPositionType = 0
  ParentDrawingView = -> ReinforcementDrawingView
  Rebar = -> Rebar010
  Rotation = 0
  Scale = 0.116818
  ScaleType = 2
  SingleRebar_LineEndSymbol = 0
  SingleRebar_LineStartSymbol = 3
  SingleRebar_OuterDimension = false
  SingleRebar_TextPositionType = 1
  StrokeWidth = 0.25
  Symbol = <svg version="1.1" xmlns="http://www.w3.org/2000/svg" xmlns:xlink="http://www.w3.org/1999/xlink" xmlns:freecad="http://www.freecadweb.org/wiki/index.php?title=Svg_Namespace" width="2200.0mm" height="804.0mm" viewBox="0 0 2200.0 804.0"><g transform="translate(100.00000000000023, 402.0000000000002)"><g><path d="M809.0 -693.0505836575878 L809.0 -1.8857907935939593e-13" style="stroke:#00007f;stroke-width:2.140077821011673;stroke-linecap:round;fill:none;" stroke-dasharray="" /><g id="line_mid_points" /><path d="M0,0 -8,-1.5 V1.5 L0,0" style="stroke:#00007f;fill:#00007f;stroke-width:2.140077821011673;stroke-linecap:round;stroke-linejoin:bevel;" transform="translate(809.0 -1.8857907935939593e-13) rotate(90.0 0 0)" /></g><text x="809.0" y="-693.0505836575878" style="white-space:pre;" fill="#005400" font-family="DejaVu Sans" font-size="25.68093385214008" text-anchor="middle" dominant-baseline="baseline" xml:space="preserve">LLRb 1⌀16,span=0</text></g></svg>
  TextPositionType = 0
  WayPoints = (2) [(0,0,0),(50,0,0)]
  WayPointsType = 0
  X = 148.5
  Y = 105
FEATURE [TechDraw::DrawViewSymbolPython] ReinforcementDimensioning009  # drawing view (typed FeaturePython)
  DimensionBottomOffset = 34
  DimensionFormat = %M %C⌀%D,span=%S
  DimensionLeftOffset = 10
  DimensionRightOffset = 10
  DimensionTopOffset = 40
  Font = DejaVu Sans
  FontSize = 3
  LineEndSymbol = 0
  LineMidPointSymbol = 1
  LineStartSymbol = 3
  LineStyle = 0
  LockPosition = false
  MultiRebar_LineEndSymbol = 0
  MultiRebar_LineStartSymbol = 0
  MultiRebar_OuterDimension = true
  MultiRebar_TextPositionType = 0
  ParentDrawingView = -> ReinforcementDrawingView
  Rebar = -> Rebar011
  Rotation = 0
  Scale = 0.116818
  ScaleType = 2
  SingleRebar_LineEndSymbol = 0
  SingleRebar_LineStartSymbol = 3
  SingleRebar_OuterDimension = false
  SingleRebar_TextPositionType = 1
  StrokeWidth = 0.25
  Symbol = <svg version="1.1" xmlns="http://www.w3.org/2000/svg" xmlns:xlink="http://www.w3.org/1999/xlink" xmlns:freecad="http://www.freecadweb.org/wiki/index.php?title=Svg_Namespace" width="2200.0mm" height="804.0mm" viewBox="0 0 2200.0 804.0"><g transform="translate(100.00000000000023, 402.0000000000002)"><g><path d="M1230.0 -744.4124513618679 L1230.0 -46.00000000000028" style="stroke:#00007f;stroke-width:2.140077821011673;stroke-linecap:round;fill:none;" stroke-dasharray="" /><g id="line_mid_points" /><path d="M0,0 -8,-1.5 V1.5 L0,0" style="stroke:#00007f;fill:#00007f;stroke-width:2.140077821011673;stroke-linecap:round;stroke-linejoin:bevel;" transform="translate(1230.0 -46.00000000000028) rotate(90.0 0 0)" /></g><text x="1230.0" y="-744.4124513618679" style="white-space:pre;" fill="#005400" font-family="DejaVu Sans" font-size="25.68093385214008" text-anchor="middle" dominant-baseline="baseline" xml:space="preserve">LLRb 1⌀16,span=0</text></g></svg>
  TextPositionType = 0
  WayPoints = (2) [(0,0,0),(50,0,0)]
  WayPointsType = 0
  X = 148.5
  Y = 105
FEATURE [TechDraw::DrawViewSymbolPython] ReinforcementDimensioning010  # drawing view (typed FeaturePython)
  DimensionBottomOffset = 34
  DimensionFormat = %M %C⌀%D,span=%S
  DimensionLeftOffset = 10
  DimensionRightOffset = 10
  DimensionTopOffset = 46
  Font = DejaVu Sans
  FontSize = 3
  LineEndSymbol = 0
  LineMidPointSymbol = 1
  LineStartSymbol = 3
  LineStyle = 0
  LockPosition = false
  MultiRebar_LineEndSymbol = 0
  MultiRebar_LineStartSymbol = 0
  MultiRebar_OuterDimension = true
  MultiRebar_TextPositionType = 0
  ParentDrawingView = -> ReinforcementDrawingView
  Rebar = -> Rebar012
  Rotation = 0
  Scale = 0.116818
  ScaleType = 2
  SingleRebar_LineEndSymbol = 0
  SingleRebar_LineStartSymbol = 3
  SingleRebar_OuterDimension = false
  SingleRebar_TextPositionType = 1
  StrokeWidth = 0.25
  Symbol = <svg version="1.1" xmlns="http://www.w3.org/2000/svg" xmlns:xlink="http://www.w3.org/1999/xlink" xmlns:freecad="http://www.freecadweb.org/wiki/index.php?title=Svg_Namespace" width="2200.0mm" height="804.0mm" viewBox="0 0 2200.0 804.0"><g transform="translate(100.00000000000023, 402.0000000000002)"><g><path d="M536.0 693.0505836575874 L536.0 45.999999999999865" style="stroke:#00007f;stroke-width:2.140077821011673;stroke-linecap:round;fill:none;" stroke-dasharray="" /><g id="line_mid_points" /><path d="M0,0 -8,-1.5 V1.5 L0,0" style="stroke:#00007f;fill:#00007f;stroke-width:2.140077821011673;stroke-linecap:round;stroke-linejoin:bevel;" transform="translate(536.0 45.999999999999865) rotate(-90.0 0 0)" /></g><text x="536.0" y="705.8910505836574" style="white-space:pre;" fill="#005400" font-family="DejaVu Sans" font-size="25.68093385214008" text-anchor="middle" dominant-baseline="baseline" xml:space="preserve">RLRb 1⌀16,span=0</text></g></svg>
  TextPositionType = 0
  WayPoints = (2) [(0,0,0),(50,0,0)]
  WayPointsType = 0
  X = 148.5
  Y = 105
FEATURE [TechDraw::DrawViewSymbolPython] ReinforcementDimensioning011  # drawing view (typed FeaturePython)
  DimensionBottomOffset = 40
  DimensionFormat = %M %C⌀%D,span=%S
  DimensionLeftOffset = 10
  DimensionRightOffset = 10
  DimensionTopOffset = 46
  Font = DejaVu Sans
  FontSize = 3
  LineEndSymbol = 0
  LineMidPointSymbol = 1
  LineStartSymbol = 3
  LineStyle = 0
  LockPosition = false
  MultiRebar_LineEndSymbol = 0
  MultiRebar_LineStartSymbol = 0
  MultiRebar_OuterDimension = true
  MultiRebar_TextPositionType = 0
  ParentDrawingView = -> ReinforcementDrawingView
  Rebar = -> Rebar013
  Rotation = 0
  Scale = 0.116818
  ScaleType = 2
  SingleRebar_LineEndSymbol = 0
  SingleRebar_LineStartSymbol = 3
  SingleRebar_OuterDimension = false
  SingleRebar_TextPositionType = 1
  StrokeWidth = 0.25
  Symbol = <svg version="1.1" xmlns="http://www.w3.org/2000/svg" xmlns:xlink="http://www.w3.org/1999/xlink" xmlns:freecad="http://www.freecadweb.org/wiki/index.php?title=Svg_Namespace" width="2200.0mm" height="804.0mm" viewBox="0 0 2200.0 804.0"><g transform="translate(100.00000000000023, 402.0000000000002)"><g><path d="M241.0 -795.7743190661481 L241.0 -6.90834251118579e-14" style="stroke:#00007f;stroke-width:2.140077821011673;stroke-linecap:round;fill:none;" stroke-dasharray="" /><g id="line_mid_points" /><path d="M0,0 -8,-1.5 V1.5 L0,0" style="stroke:#00007f;fill:#00007f;stroke-width:2.140077821011673;stroke-linecap:round;stroke-linejoin:bevel;" transform="translate(241.0 -6.90834251118579e-14) rotate(90.0 0 0)" /></g><text x="241.0" y="-795.7743190661481" style="white-space:pre;" fill="#005400" font-family="DejaVu Sans" font-size="25.68093385214008" text-anchor="middle" dominant-baseline="baseline" xml:space="preserve">RLRb 1⌀16,span=0</text></g></svg>
  TextPositionType = 0
  WayPoints = (2) [(0,0,0),(50,0,0)]
  WayPointsType = 0
  X = 148.5
  Y = 105
FEATURE [TechDraw::DrawViewSymbolPython] ReinforcementDimensioning012  # drawing view (typed FeaturePython)
  DimensionBottomOffset = 40
  DimensionFormat = %M %C⌀%D,span=%S
  DimensionLeftOffset = 10
  DimensionRightOffset = 10
  DimensionTopOffset = 52
  Font = DejaVu Sans
  FontSize = 3
  LineEndSymbol = 0
  LineMidPointSymbol = 1
  LineStartSymbol = 3
  LineStyle = 0
  LockPosition = false
  MultiRebar_LineEndSymbol = 0
  MultiRebar_LineStartSymbol = 0
  MultiRebar_OuterDimension = true
  MultiRebar_TextPositionType = 0
  ParentDrawingView = -> ReinforcementDrawingView
  Rebar = -> Rebar014
  Rotation = 0
  Scale = 0.116818
  ScaleType = 2
  SingleRebar_LineEndSymbol = 0
  SingleRebar_LineStartSymbol = 3
  SingleRebar_OuterDimension = false
  SingleRebar_TextPositionType = 1
  StrokeWidth = 0.25
  Symbol = <svg version="1.1" xmlns="http://www.w3.org/2000/svg" xmlns:xlink="http://www.w3.org/1999/xlink" xmlns:freecad="http://www.freecadweb.org/wiki/index.php?title=Svg_Namespace" width="2200.0mm" height="804.0mm" viewBox="0 0 2200.0 804.0"><g transform="translate(100.00000000000023, 402.0000000000002)"><g><path d="M728.0 -847.1361867704283 L728.0 -46.00000000000017" style="stroke:#00007f;stroke-width:2.140077821011673;stroke-linecap:round;fill:none;" stroke-dasharray="" /><g id="line_mid_points" /><path d="M0,0 -8,-1.5 V1.5 L0,0" style="stroke:#00007f;fill:#00007f;stroke-width:2.140077821011673;stroke-linecap:round;stroke-linejoin:bevel;" transform="translate(728.0 -46.00000000000017) rotate(90.0 0 0)" /></g><text x="728.0" y="-847.1361867704283" style="white-space:pre;" fill="#005400" font-family="DejaVu Sans" font-size="25.68093385214008" text-anchor="middle" dominant-baseline="baseline" xml:space="preserve">RLRb 1⌀16,span=0</text></g></svg>
  TextPositionType = 0
  WayPoints = (2) [(0,0,0),(50,0,0)]
  WayPointsType = 0
  X = 148.5
  Y = 105
FEATURE [TechDraw::DrawPage] TechDraw__DrawPage  label="Beam Drawing"
  KeepUpdated = true
  NextBalloonIndex = 1
  ProjectionType = 0
  Template = -> Template
  Views = -> [ReinforcementDrawingView,ReinforcementDimensioning,ReinforcementDimensioning001,ReinforcementDimensioning002,ReinforcementDimensioning003,ReinforcementDimensioning004,ReinforcementDimensioning005,ReinforcementDimensioning006,ReinforcementDimensioning007,ReinforcementDimensioning008,ReinforcementDimensioning009,ReinforcementDimensioning010,ReinforcementDimensioning011,ReinforcementDimensioning012]
FEATURE [TechDraw::DrawSVGTemplate] Template001
  Height = 210
  Orientation = 1
  Width = 297
FEATURE [TechDraw::DrawViewSymbolPython] ReinforcementDrawingView001  label="Rear View"  # drawing view (typed FeaturePython)
  DimensionBottomOffset = 40
  DimensionLeftOffset = 10
  DimensionRightOffset = 10
  DimensionTopOffset = 58
  Height = 804
  LeftOffset = 20
  LockPosition = false
  MaxHeight = 210
  MaxWidth = 297
  MinBottomOffset = 20
  MinRightOffset = 20
  PositionType = 0
  Rebars = -> [Rebar,Rebar001,Rebar002,Rebar003,Rebar004,Rebar005,Rebar006,Rebar007,Rebar008,Rebar009,Rebar010,Rebar011,Rebar012,Rebar013,Rebar014]
  RebarsColorStyle = 0
  RebarsStrokeWidth = 0.35
  Rotation = 0
  Scale = 0.116818
  ScaleType = 1
  Structure = -> Structure
  StructureColorStyle = 0
  StructureStrokeWidth = 0.5
  Symbol = <blob: 8343 chars omitted>
  Template = -> Template001
  TopOffset = 58.0391
  View = 1
  VisibleRebars = -> [Rebar,Rebar001,Rebar002,Rebar004,Rebar005,Rebar006,Rebar008,Rebar009,Rebar010,Rebar011,Rebar012,Rebar013,Rebar014]
  Width = 2200
  X = 148.5
  Y = 105
  expr: TopOffset = .Template.Height.Value / 2 - .Height.Value * .Scale / 2
  expr: LeftOffset = .Template.Width.Value / 2 - .Width.Value * .Scale / 2
FEATURE [TechDraw::DrawViewSymbolPython] ReinforcementDimensioning013  # drawing view (typed FeaturePython)
  DimensionBottomOffset = 10
  DimensionFormat = %M %C⌀%D,span=%S
  DimensionLeftOffset = 10
  DimensionRightOffset = 10
  DimensionTopOffset = 10
  Font = DejaVu Sans
  FontSize = 3
  LineEndSymbol = 0
  LineMidPointSymbol = 1
  LineStartSymbol = 3
  LineStyle = 0
  LockPosition = false
  MultiRebar_LineEndSymbol = 0
  MultiRebar_LineStartSymbol = 0
  MultiRebar_OuterDimension = true
  MultiRebar_TextPositionType = 0
  ParentDrawingView = -> ReinforcementDrawingView001
  Rebar = -> Rebar
  Rotation = 0
  Scale = 0.116818
  ScaleType = 2
  SingleRebar_LineEndSymbol = 0
  SingleRebar_LineStartSymbol = 3
  SingleRebar_OuterDimension = false
  SingleRebar_TextPositionType = 1
  StrokeWidth = 0.25
  Symbol = <blob: 5899 chars omitted>
  TextPositionType = 0
  WayPoints = (2) [(0,0,0),(50,0,0)]
  WayPointsType = 0
  X = 148.5
  Y = 105
FEATURE [TechDraw::DrawViewSymbolPython] ReinforcementDimensioning014  # drawing view (typed FeaturePython)
  DimensionBottomOffset = 10
  DimensionFormat = %M %C⌀%D,span=%S
  DimensionLeftOffset = 10
  DimensionRightOffset = 10
  DimensionTopOffset = 16
  Font = DejaVu Sans
  FontSize = 3
  LineEndSymbol = 0
  LineMidPointSymbol = 1
  LineStartSymbol = 3
  LineStyle = 0
  LockPosition = false
  MultiRebar_LineEndSymbol = 0
  MultiRebar_LineStartSymbol = 0
  MultiRebar_OuterDimension = true
  MultiRebar_TextPositionType = 0
  ParentDrawingView = -> ReinforcementDrawingView001
  Rebar = -> Rebar001
  Rotation = 0
  Scale = 0.116818
  ScaleType = 2
  SingleRebar_LineEndSymbol = 0
  SingleRebar_LineStartSymbol = 3
  SingleRebar_OuterDimension = false
  SingleRebar_TextPositionType = 1
  StrokeWidth = 0.25
  Symbol = <svg version="1.1" xmlns="http://www.w3.org/2000/svg" xmlns:xlink="http://www.w3.org/1999/xlink" xmlns:freecad="http://www.freecadweb.org/wiki/index.php?title=Svg_Namespace" width="2200.0mm" height="804.0mm" viewBox="0 0 2200.0 804.0"><g transform="translate(2100.0, 402.0000000000002)"><g><path d="M-1297.0 -538.9649805447473 L-1297.0 -262.0000000000002" style="stroke:#00007f;stroke-width:2.140077821011673;stroke-linecap:round;fill:none;" stroke-dasharray="" /><g id="line_mid_points" /><path d="M0,0 -8,-1.5 V1.5 L0,0" style="stroke:#00007f;fill:#00007f;stroke-width:2.140077821011673;stroke-linecap:round;stroke-linejoin:bevel;" transform="translate(-1297.0 -262.0000000000002) rotate(90.0 0 0)" /></g><text x="-1297.0" y="-538.9649805447473" style="white-space:pre;" fill="#005400" font-family="DejaVu Sans" font-size="25.68093385214008" text-anchor="middle" dominant-baseline="baseline" xml:space="preserve">TLRb 1⌀20,span=0</text></g></svg>
  TextPositionType = 0
  WayPoints = (2) [(0,0,0),(50,0,0)]
  WayPointsType = 0
  X = 148.5
  Y = 105
FEATURE [TechDraw::DrawViewSymbolPython] ReinforcementDimensioning015  # drawing view (typed FeaturePython)
  DimensionBottomOffset = 10
  DimensionFormat = %M %C⌀%D,span=%S
  DimensionLeftOffset = 10
  DimensionRightOffset = 10
  DimensionTopOffset = 22
  Font = DejaVu Sans
  FontSize = 3
  LineEndSymbol = 0
  LineMidPointSymbol = 1
  LineStartSymbol = 3
  LineStyle = 0
  LockPosition = false
  MultiRebar_LineEndSymbol = 0
  MultiRebar_LineStartSymbol = 0
  MultiRebar_OuterDimension = true
  MultiRebar_TextPositionType = 0
  ParentDrawingView = -> ReinforcementDrawingView001
  Rebar = -> Rebar002
  Rotation = 0
  Scale = 0.116818
  ScaleType = 2
  SingleRebar_LineEndSymbol = 0
  SingleRebar_LineStartSymbol = 3
  SingleRebar_OuterDimension = false
  SingleRebar_TextPositionType = 1
  StrokeWidth = 0.25
  Symbol = <svg version="1.1" xmlns="http://www.w3.org/2000/svg" xmlns:xlink="http://www.w3.org/1999/xlink" xmlns:freecad="http://www.freecadweb.org/wiki/index.php?title=Svg_Namespace" width="2200.0mm" height="804.0mm" viewBox="0 0 2200.0 804.0"><g transform="translate(2100.0, 402.0000000000002)"><g><path d="M-1574.0 -590.3268482490274 L-1574.0 -264.00000000000017" style="stroke:#00007f;stroke-width:2.140077821011673;stroke-linecap:round;fill:none;" stroke-dasharray="" /><g id="line_mid_points" /><path d="M0,0 -8,-1.5 V1.5 L0,0" style="stroke:#00007f;fill:#00007f;stroke-width:2.140077821011673;stroke-linecap:round;stroke-linejoin:bevel;" transform="translate(-1574.0 -264.00000000000017) rotate(90.0 0 0)" /></g><text x="-1574.0" y="-590.3268482490274" style="white-space:pre;" fill="#005400" font-family="DejaVu Sans" font-size="25.68093385214008" text-anchor="middle" dominant-baseline="baseline" xml:space="preserve">TLRb 2⌀16,span=107</text></g></svg>
  TextPositionType = 0
  WayPoints = (2) [(0,0,0),(50,0,0)]
  WayPointsType = 0
  X = 148.5
  Y = 105
FEATURE [TechDraw::DrawViewSymbolPython] ReinforcementDimensioning016  # drawing view (typed FeaturePython)
  DimensionBottomOffset = 10
  DimensionFormat = %M %C⌀%D,span=%S
  DimensionLeftOffset = 10
  DimensionRightOffset = 10
  DimensionTopOffset = 28
  Font = DejaVu Sans
  FontSize = 3
  LineEndSymbol = 0
  LineMidPointSymbol = 1
  LineStartSymbol = 3
  LineStyle = 0
  LockPosition = false
  MultiRebar_LineEndSymbol = 0
  MultiRebar_LineStartSymbol = 0
  MultiRebar_OuterDimension = true
  MultiRebar_TextPositionType = 0
  ParentDrawingView = -> ReinforcementDrawingView001
  Rebar = -> Rebar004
  Rotation = 0
  Scale = 0.116818
  ScaleType = 2
  SingleRebar_LineEndSymbol = 0
  SingleRebar_LineStartSymbol = 3
  SingleRebar_OuterDimension = false
  SingleRebar_TextPositionType = 1
  StrokeWidth = 0.25
  Symbol = <svg version="1.1" xmlns="http://www.w3.org/2000/svg" xmlns:xlink="http://www.w3.org/1999/xlink" xmlns:freecad="http://www.freecadweb.org/wiki/index.php?title=Svg_Namespace" width="2200.0mm" height="804.0mm" viewBox="0 0 2200.0 804.0"><g transform="translate(2100.0, 402.0000000000002)"><g><path d="M-248.0 -641.6887159533076 L-248.0 -218.00000000000023" style="stroke:#00007f;stroke-width:2.140077821011673;stroke-linecap:round;fill:none;" stroke-dasharray="" /><g id="line_mid_points" /><path d="M0,0 -8,-1.5 V1.5 L0,0" style="stroke:#00007f;fill:#00007f;stroke-width:2.140077821011673;stroke-linecap:round;stroke-linejoin:bevel;" transform="translate(-248.0 -218.00000000000023) rotate(90.0 0 0)" /></g><text x="-248.0" y="-641.6887159533076" style="white-space:pre;" fill="#005400" font-family="DejaVu Sans" font-size="25.68093385214008" text-anchor="middle" dominant-baseline="baseline" xml:space="preserve">TLRb 3⌀16,span=328</text></g></svg>
  TextPositionType = 0
  WayPoints = (2) [(0,0,0),(50,0,0)]
  WayPointsType = 0
  X = 148.5
  Y = 105
FEATURE [TechDraw::DrawViewSymbolPython] ReinforcementDimensioning017  # drawing view (typed FeaturePython)
  DimensionBottomOffset = 10
  DimensionFormat = %M %C⌀%D,span=%S
  DimensionLeftOffset = 10
  DimensionRightOffset = 10
  DimensionTopOffset = 34
  Font = DejaVu Sans
  FontSize = 3
  LineEndSymbol = 0
  LineMidPointSymbol = 1
  LineStartSymbol = 3
  LineStyle = 0
  LockPosition = false
  MultiRebar_LineEndSymbol = 0
  MultiRebar_LineStartSymbol = 0
  MultiRebar_OuterDimension = true
  MultiRebar_TextPositionType = 0
  ParentDrawingView = -> ReinforcementDrawingView001
  Rebar = -> Rebar005
  Rotation = 0
  Scale = 0.116818
  ScaleType = 2
  SingleRebar_LineEndSymbol = 0
  SingleRebar_LineStartSymbol = 3
  SingleRebar_OuterDimension = false
  SingleRebar_TextPositionType = 1
  StrokeWidth = 0.25
  Symbol = <svg version="1.1" xmlns="http://www.w3.org/2000/svg" xmlns:xlink="http://www.w3.org/1999/xlink" xmlns:freecad="http://www.freecadweb.org/wiki/index.php?title=Svg_Namespace" width="2200.0mm" height="804.0mm" viewBox="0 0 2200.0 804.0"><g transform="translate(2100.0, 402.0000000000002)"><g><path d="M-166.0 487.60311284046674 L-166.0 261.9999999999998" style="stroke:#00007f;stroke-width:2.140077821011673;stroke-linecap:round;fill:none;" stroke-dasharray="" /><g id="line_mid_points" /><path d="M0,0 -8,-1.5 V1.5 L0,0" style="stroke:#00007f;fill:#00007f;stroke-width:2.140077821011673;stroke-linecap:round;stroke-linejoin:bevel;" transform="translate(-166.0 261.9999999999998) rotate(-90.0 0 0)" /></g><text x="-166.0" y="500.4435797665368" style="white-space:pre;" fill="#005400" font-family="DejaVu Sans" font-size="25.68093385214008" text-anchor="middle" dominant-baseline="baseline" xml:space="preserve">BLRb 1⌀20,span=0</text></g></svg>
  TextPositionType = 0
  WayPoints = (2) [(0,0,0),(50,0,0)]
  WayPointsType = 0
  X = 148.5
  Y = 105
FEATURE [TechDraw::DrawViewSymbolPython] ReinforcementDimensioning018  # drawing view (typed FeaturePython)
  DimensionBottomOffset = 16
  DimensionFormat = %M %C⌀%D,span=%S
  DimensionLeftOffset = 10
  DimensionRightOffset = 10
  DimensionTopOffset = 34
  Font = DejaVu Sans
  FontSize = 3
  LineEndSymbol = 0
  LineMidPointSymbol = 1
  LineStartSymbol = 3
  LineStyle = 0
  LockPosition = false
  MultiRebar_LineEndSymbol = 0
  MultiRebar_LineStartSymbol = 0
  MultiRebar_OuterDimension = true
  MultiRebar_TextPositionType = 0
  ParentDrawingView = -> ReinforcementDrawingView001
  Rebar = -> Rebar006
  Rotation = 0
  Scale = 0.116818
  ScaleType = 2
  SingleRebar_LineEndSymbol = 0
  SingleRebar_LineStartSymbol = 3
  SingleRebar_OuterDimension = false
  SingleRebar_TextPositionType = 1
  StrokeWidth = 0.25
  Symbol = <svg version="1.1" xmlns="http://www.w3.org/2000/svg" xmlns:xlink="http://www.w3.org/1999/xlink" xmlns:freecad="http://www.freecadweb.org/wiki/index.php?title=Svg_Namespace" width="2200.0mm" height="804.0mm" viewBox="0 0 2200.0 804.0"><g transform="translate(2100.0, 402.0000000000002)"><g><path d="M-1002.0 538.9649805447469 L-1002.0 263.99999999999983" style="stroke:#00007f;stroke-width:2.140077821011673;stroke-linecap:round;fill:none;" stroke-dasharray="" /><g id="line_mid_points" /><path d="M0,0 -8,-1.5 V1.5 L0,0" style="stroke:#00007f;fill:#00007f;stroke-width:2.140077821011673;stroke-linecap:round;stroke-linejoin:bevel;" transform="translate(-1002.0 263.99999999999983) rotate(-90.0 0 0)" /></g><text x="-1002.0" y="551.805447470817" style="white-space:pre;" fill="#005400" font-family="DejaVu Sans" font-size="25.68093385214008" text-anchor="middle" dominant-baseline="baseline" xml:space="preserve">BLRb 2⌀16,span=107</text></g></svg>
  TextPositionType = 0
  WayPoints = (2) [(0,0,0),(50,0,0)]
  WayPointsType = 0
  X = 148.5
  Y = 105
FEATURE [TechDraw::DrawViewSymbolPython] ReinforcementDimensioning019  # drawing view (typed FeaturePython)
  DimensionBottomOffset = 22
  DimensionFormat = %M %C⌀%D,span=%S
  DimensionLeftOffset = 10
  DimensionRightOffset = 10
  DimensionTopOffset = 34
  Font = DejaVu Sans
  FontSize = 3
  LineEndSymbol = 0
  LineMidPointSymbol = 1
  LineStartSymbol = 3
  LineStyle = 0
  LockPosition = false
  MultiRebar_LineEndSymbol = 0
  MultiRebar_LineStartSymbol = 0
  MultiRebar_OuterDimension = true
  MultiRebar_TextPositionType = 0
  ParentDrawingView = -> ReinforcementDrawingView001
  Rebar = -> Rebar008
  Rotation = 0
  Scale = 0.116818
  ScaleType = 2
  SingleRebar_LineEndSymbol = 0
  SingleRebar_LineStartSymbol = 3
  SingleRebar_OuterDimension = false
  SingleRebar_TextPositionType = 1
  StrokeWidth = 0.25
  Symbol = <svg version="1.1" xmlns="http://www.w3.org/2000/svg" xmlns:xlink="http://www.w3.org/1999/xlink" xmlns:freecad="http://www.freecadweb.org/wiki/index.php?title=Svg_Namespace" width="2200.0mm" height="804.0mm" viewBox="0 0 2200.0 804.0"><g transform="translate(2100.0, 402.0000000000002)"><g><path d="M-1748.0 590.3268482490271 L-1748.0 217.99999999999977" style="stroke:#00007f;stroke-width:2.140077821011673;stroke-linecap:round;fill:none;" stroke-dasharray="" /><g id="line_mid_points" /><path d="M0,0 -8,-1.5 V1.5 L0,0" style="stroke:#00007f;fill:#00007f;stroke-width:2.140077821011673;stroke-linecap:round;stroke-linejoin:bevel;" transform="translate(-1748.0 217.99999999999977) rotate(-90.0 0 0)" /></g><text x="-1748.0" y="603.1673151750971" style="white-space:pre;" fill="#005400" font-family="DejaVu Sans" font-size="25.68093385214008" text-anchor="middle" dominant-baseline="baseline" xml:space="preserve">BLRb 3⌀16,span=328</text></g></svg>
  TextPositionType = 0
  WayPoints = (2) [(0,0,0),(50,0,0)]
  WayPointsType = 0
  X = 148.5
  Y = 105
FEATURE [TechDraw::DrawViewSymbolPython] ReinforcementDimensioning020  # drawing view (typed FeaturePython)
  DimensionBottomOffset = 28
  DimensionFormat = %M %C⌀%D,span=%S
  DimensionLeftOffset = 10
  DimensionRightOffset = 10
  DimensionTopOffset = 34
  Font = DejaVu Sans
  FontSize = 3
  LineEndSymbol = 0
  LineMidPointSymbol = 1
  LineStartSymbol = 3
  LineStyle = 0
  LockPosition = false
  MultiRebar_LineEndSymbol = 0
  MultiRebar_LineStartSymbol = 0
  MultiRebar_OuterDimension = true
  MultiRebar_TextPositionType = 0
  ParentDrawingView = -> ReinforcementDrawingView001
  Rebar = -> Rebar009
  Rotation = 0
  Scale = 0.116818
  ScaleType = 2
  SingleRebar_LineEndSymbol = 0
  SingleRebar_LineStartSymbol = 3
  SingleRebar_OuterDimension = false
  SingleRebar_TextPositionType = 1
  StrokeWidth = 0.25
  Symbol = <svg version="1.1" xmlns="http://www.w3.org/2000/svg" xmlns:xlink="http://www.w3.org/1999/xlink" xmlns:freecad="http://www.freecadweb.org/wiki/index.php?title=Svg_Namespace" width="2200.0mm" height="804.0mm" viewBox="0 0 2200.0 804.0"><g transform="translate(2100.0, 402.0000000000002)"><g><path d="M-1728.0 641.6887159533072 L-1728.0 45.99999999999962" style="stroke:#00007f;stroke-width:2.140077821011673;stroke-linecap:round;fill:none;" stroke-dasharray="" /><g id="line_mid_points" /><path d="M0,0 -8,-1.5 V1.5 L0,0" style="stroke:#00007f;fill:#00007f;stroke-width:2.140077821011673;stroke-linecap:round;stroke-linejoin:bevel;" transform="translate(-1728.0 45.99999999999962) rotate(-90.0 0 0)" /></g><text x="-1728.0" y="654.5291828793772" style="white-space:pre;" fill="#005400" font-family="DejaVu Sans" font-size="25.68093385214008" text-anchor="middle" dominant-baseline="baseline" xml:space="preserve">LLRb 1⌀16,span=0</text></g></svg>
  TextPositionType = 0
  WayPoints = (2) [(0,0,0),(50,0,0)]
  WayPointsType = 0
  X = 148.5
  Y = 105
FEATURE [TechDraw::DrawViewSymbolPython] ReinforcementDimensioning021  # drawing view (typed FeaturePython)
  DimensionBottomOffset = 34
  DimensionFormat = %M %C⌀%D,span=%S
  DimensionLeftOffset = 10
  DimensionRightOffset = 10
  DimensionTopOffset = 34
  Font = DejaVu Sans
  FontSize = 3
  LineEndSymbol = 0
  LineMidPointSymbol = 1
  LineStartSymbol = 3
  LineStyle = 0
  LockPosition = false
  MultiRebar_LineEndSymbol = 0
  MultiRebar_LineStartSymbol = 0
  MultiRebar_OuterDimension = true
  MultiRebar_TextPositionType = 0
  ParentDrawingView = -> ReinforcementDrawingView001
  Rebar = -> Rebar010
  Rotation = 0
  Scale = 0.116818
  ScaleType = 2
  SingleRebar_LineEndSymbol = 0
  SingleRebar_LineStartSymbol = 3
  SingleRebar_OuterDimension = false
  SingleRebar_TextPositionType = 1
  StrokeWidth = 0.25
  Symbol = <svg version="1.1" xmlns="http://www.w3.org/2000/svg" xmlns:xlink="http://www.w3.org/1999/xlink" xmlns:freecad="http://www.freecadweb.org/wiki/index.php?title=Svg_Namespace" width="2200.0mm" height="804.0mm" viewBox="0 0 2200.0 804.0"><g transform="translate(2100.0, 402.0000000000002)"><g><path d="M-235.0 -693.0505836575878 L-235.0 -6.94983405779952e-14" style="stroke:#00007f;stroke-width:2.140077821011673;stroke-linecap:round;fill:none;" stroke-dasharray="" /><g id="line_mid_points" /><path d="M0,0 -8,-1.5 V1.5 L0,0" style="stroke:#00007f;fill:#00007f;stroke-width:2.140077821011673;stroke-linecap:round;stroke-linejoin:bevel;" transform="translate(-235.0 -6.94983405779952e-14) rotate(90.0 0 0)" /></g><text x="-235.0" y="-693.0505836575878" style="white-space:pre;" fill="#005400" font-family="DejaVu Sans" font-size="25.68093385214008" text-anchor="middle" dominant-baseline="baseline" xml:space="preserve">LLRb 1⌀16,span=0</text></g></svg>
  TextPositionType = 0
  WayPoints = (2) [(0,0,0),(50,0,0)]
  WayPointsType = 0
  X = 148.5
  Y = 105
FEATURE [TechDraw::DrawViewSymbolPython] ReinforcementDimensioning022  # drawing view (typed FeaturePython)
  DimensionBottomOffset = 34
  DimensionFormat = %M %C⌀%D,span=%S
  DimensionLeftOffset = 10
  DimensionRightOffset = 10
  DimensionTopOffset = 40
  Font = DejaVu Sans
  FontSize = 3
  LineEndSymbol = 0
  LineMidPointSymbol = 1
  LineStartSymbol = 3
  LineStyle = 0
  LockPosition = false
  MultiRebar_LineEndSymbol = 0
  MultiRebar_LineStartSymbol = 0
  MultiRebar_OuterDimension = true
  MultiRebar_TextPositionType = 0
  ParentDrawingView = -> ReinforcementDrawingView001
  Rebar = -> Rebar011
  Rotation = 0
  Scale = 0.116818
  ScaleType = 2
  SingleRebar_LineEndSymbol = 0
  SingleRebar_LineStartSymbol = 3
  SingleRebar_OuterDimension = false
  SingleRebar_TextPositionType = 1
  StrokeWidth = 0.25
  Symbol = <svg version="1.1" xmlns="http://www.w3.org/2000/svg" xmlns:xlink="http://www.w3.org/1999/xlink" xmlns:freecad="http://www.freecadweb.org/wiki/index.php?title=Svg_Namespace" width="2200.0mm" height="804.0mm" viewBox="0 0 2200.0 804.0"><g transform="translate(2100.0, 402.0000000000002)"><g><path d="M-1028.0 -744.4124513618679 L-1028.0 -46.000000000000234" style="stroke:#00007f;stroke-width:2.140077821011673;stroke-linecap:round;fill:none;" stroke-dasharray="" /><g id="line_mid_points" /><path d="M0,0 -8,-1.5 V1.5 L0,0" style="stroke:#00007f;fill:#00007f;stroke-width:2.140077821011673;stroke-linecap:round;stroke-linejoin:bevel;" transform="translate(-1028.0 -46.000000000000234) rotate(90.0 0 0)" /></g><text x="-1028.0" y="-744.4124513618679" style="white-space:pre;" fill="#005400" font-family="DejaVu Sans" font-size="25.68093385214008" text-anchor="middle" dominant-baseline="baseline" xml:space="preserve">LLRb 1⌀16,span=0</text></g></svg>
  TextPositionType = 0
  WayPoints = (2) [(0,0,0),(50,0,0)]
  WayPointsType = 0
  X = 148.5
  Y = 105
FEATURE [TechDraw::DrawViewSymbolPython] ReinforcementDimensioning023  # drawing view (typed FeaturePython)
  DimensionBottomOffset = 34
  DimensionFormat = %M %C⌀%D,span=%S
  DimensionLeftOffset = 10
  DimensionRightOffset = 10
  DimensionTopOffset = 46
  Font = DejaVu Sans
  FontSize = 3
  LineEndSymbol = 0
  LineMidPointSymbol = 1
  LineStartSymbol = 3
  LineStyle = 0
  LockPosition = false
  MultiRebar_LineEndSymbol = 0
  MultiRebar_LineStartSymbol = 0
  MultiRebar_OuterDimension = true
  MultiRebar_TextPositionType = 0
  ParentDrawingView = -> ReinforcementDrawingView001
  Rebar = -> Rebar012
  Rotation = 0
  Scale = 0.116818
  ScaleType = 2
  SingleRebar_LineEndSymbol = 0
  SingleRebar_LineStartSymbol = 3
  SingleRebar_OuterDimension = false
  SingleRebar_TextPositionType = 1
  StrokeWidth = 0.25
  Symbol = <svg version="1.1" xmlns="http://www.w3.org/2000/svg" xmlns:xlink="http://www.w3.org/1999/xlink" xmlns:freecad="http://www.freecadweb.org/wiki/index.php?title=Svg_Namespace" width="2200.0mm" height="804.0mm" viewBox="0 0 2200.0 804.0"><g transform="translate(2100.0, 402.0000000000002)"><g><path d="M-863.0 693.0505836575874 L-863.0 45.9999999999998" style="stroke:#00007f;stroke-width:2.140077821011673;stroke-linecap:round;fill:none;" stroke-dasharray="" /><g id="line_mid_points" /><path d="M0,0 -8,-1.5 V1.5 L0,0" style="stroke:#00007f;fill:#00007f;stroke-width:2.140077821011673;stroke-linecap:round;stroke-linejoin:bevel;" transform="translate(-863.0 45.9999999999998) rotate(-90.0 0 0)" /></g><text x="-863.0" y="705.8910505836574" style="white-space:pre;" fill="#005400" font-family="DejaVu Sans" font-size="25.68093385214008" text-anchor="middle" dominant-baseline="baseline" xml:space="preserve">RLRb 1⌀16,span=0</text></g></svg>
  TextPositionType = 0
  WayPoints = (2) [(0,0,0),(50,0,0)]
  WayPointsType = 0
  X = 148.5
  Y = 105
FEATURE [TechDraw::DrawViewSymbolPython] ReinforcementDimensioning024  # drawing view (typed FeaturePython)
  DimensionBottomOffset = 40
  DimensionFormat = %M %C⌀%D,span=%S
  DimensionLeftOffset = 10
  DimensionRightOffset = 10
  DimensionTopOffset = 46
  Font = DejaVu Sans
  FontSize = 3
  LineEndSymbol = 0
  LineMidPointSymbol = 1
  LineStartSymbol = 3
  LineStyle = 0
  LockPosition = false
  MultiRebar_LineEndSymbol = 0
  MultiRebar_LineStartSymbol = 0
  MultiRebar_OuterDimension = true
  MultiRebar_TextPositionType = 0
  ParentDrawingView = -> ReinforcementDrawingView001
  Rebar = -> Rebar013
  Rotation = 0
  Scale = 0.116818
  ScaleType = 2
  SingleRebar_LineEndSymbol = 0
  SingleRebar_LineStartSymbol = 3
  SingleRebar_OuterDimension = false
  SingleRebar_TextPositionType = 1
  StrokeWidth = 0.25
  Symbol = <svg version="1.1" xmlns="http://www.w3.org/2000/svg" xmlns:xlink="http://www.w3.org/1999/xlink" xmlns:freecad="http://www.freecadweb.org/wiki/index.php?title=Svg_Namespace" width="2200.0mm" height="804.0mm" viewBox="0 0 2200.0 804.0"><g transform="translate(2100.0, 402.0000000000002)"><g><path d="M-1331.0 -795.7743190661481 L-1331.0 -2.9521235415667815e-13" style="stroke:#00007f;stroke-width:2.140077821011673;stroke-linecap:round;fill:none;" stroke-dasharray="" /><g id="line_mid_points" /><path d="M0,0 -8,-1.5 V1.5 L0,0" style="stroke:#00007f;fill:#00007f;stroke-width:2.140077821011673;stroke-linecap:round;stroke-linejoin:bevel;" transform="translate(-1331.0 -2.9521235415667815e-13) rotate(90.0 0 0)" /></g><text x="-1331.0" y="-795.7743190661481" style="white-space:pre;" fill="#005400" font-family="DejaVu Sans" font-size="25.68093385214008" text-anchor="middle" dominant-baseline="baseline" xml:space="preserve">RLRb 1⌀16,span=0</text></g></svg>
  TextPositionType = 0
  WayPoints = (2) [(0,0,0),(50,0,0)]
  WayPointsType = 0
  X = 148.5
  Y = 105
FEATURE [TechDraw::DrawViewSymbolPython] ReinforcementDimensioning025  # drawing view (typed FeaturePython)
  DimensionBottomOffset = 40
  DimensionFormat = %M %C⌀%D,span=%S
  DimensionLeftOffset = 10
  DimensionRightOffset = 10
  DimensionTopOffset = 52
  Font = DejaVu Sans
  FontSize = 3
  LineEndSymbol = 0
  LineMidPointSymbol = 1
  LineStartSymbol = 3
  LineStyle = 0
  LockPosition = false
  MultiRebar_LineEndSymbol = 0
  MultiRebar_LineStartSymbol = 0
  MultiRebar_OuterDimension = true
  MultiRebar_TextPositionType = 0
  ParentDrawingView = -> ReinforcementDrawingView001
  Rebar = -> Rebar014
  Rotation = 0
  Scale = 0.116818
  ScaleType = 2
  SingleRebar_LineEndSymbol = 0
  SingleRebar_LineStartSymbol = 3
  SingleRebar_OuterDimension = false
  SingleRebar_TextPositionType = 1
  StrokeWidth = 0.25
  Symbol = <svg version="1.1" xmlns="http://www.w3.org/2000/svg" xmlns:xlink="http://www.w3.org/1999/xlink" xmlns:freecad="http://www.freecadweb.org/wiki/index.php?title=Svg_Namespace" width="2200.0mm" height="804.0mm" viewBox="0 0 2200.0 804.0"><g transform="translate(2100.0, 402.0000000000002)"><g><path d="M-351.0 -847.1361867704283 L-351.0 -46.00000000000009" style="stroke:#00007f;stroke-width:2.140077821011673;stroke-linecap:round;fill:none;" stroke-dasharray="" /><g id="line_mid_points" /><path d="M0,0 -8,-1.5 V1.5 L0,0" style="stroke:#00007f;fill:#00007f;stroke-width:2.140077821011673;stroke-linecap:round;stroke-linejoin:bevel;" transform="translate(-351.0 -46.00000000000009) rotate(90.0 0 0)" /></g><text x="-351.0" y="-847.1361867704283" style="white-space:pre;" fill="#005400" font-family="DejaVu Sans" font-size="25.68093385214008" text-anchor="middle" dominant-baseline="baseline" xml:space="preserve">RLRb 1⌀16,span=0</text></g></svg>
  TextPositionType = 0
  WayPoints = (2) [(0,0,0),(50,0,0)]
  WayPointsType = 0
  X = 148.5
  Y = 105
FEATURE [TechDraw::DrawPage] TechDraw__DrawPage001  label="Beam Drawing001"
  KeepUpdated = true
  NextBalloonIndex = 1
  ProjectionType = 0
  Template = -> Template001
  Views = -> [ReinforcementDrawingView001,ReinforcementDimensioning013,ReinforcementDimensioning014,ReinforcementDimensioning015,ReinforcementDimensioning016,ReinforcementDimensioning017,ReinforcementDimensioning018,ReinforcementDimensioning019,ReinforcementDimensioning020,ReinforcementDimensioning021,ReinforcementDimensioning022,ReinforcementDimensioning023,ReinforcementDimensioning024,+1 more]
FEATURE [TechDraw::DrawSVGTemplate] Template002
  Height = 210
  Orientation = 1
  Width = 297
FEATURE [TechDraw::DrawViewSymbolPython] ReinforcementDrawingView002  label="Left View"  # drawing view (typed FeaturePython)
  DimensionBottomOffset = 40
  DimensionLeftOffset = 22
  DimensionRightOffset = 22
  DimensionTopOffset = 40
  Height = 804
  LeftOffset = 108.699
  LockPosition = false
  MaxHeight = 210
  MaxWidth = 297
  MinBottomOffset = 30
  MinRightOffset = 20
  PositionType = 0
  Rebars = -> [Rebar,Rebar001,Rebar002,Rebar003,Rebar004,Rebar005,Rebar006,Rebar007,Rebar008,Rebar009,Rebar010,Rebar011,Rebar012,Rebar013,Rebar014]
  RebarsColorStyle = 0
  RebarsStrokeWidth = 0.35
  Rotation = 0
  Scale = 0.186567
  ScaleType = 1
  Structure = -> Structure
  StructureColorStyle = 0
  StructureStrokeWidth = 0.5
  Symbol = <blob: 10176 chars omitted>
  Template = -> Template002
  TopOffset = 30
  View = 2
  VisibleRebars = -> [Rebar,Rebar001,Rebar002,Rebar003,Rebar004,Rebar005,Rebar006,Rebar007,Rebar008,Rebar009,Rebar010,Rebar011,Rebar012,Rebar013,Rebar014]
  Width = 400
  X = 146.012
  Y = 105
  expr: LeftOffset = .Template.Width.Value / 2 - .Width.Value * .Scale / 2
FEATURE [TechDraw::DrawViewSymbolPython] ReinforcementDimensioning026  # drawing view (typed FeaturePython)
  DimensionBottomOffset = 10
  DimensionFormat = %M %C⌀%D,span=%S
  DimensionLeftOffset = 10
  DimensionRightOffset = 10
  DimensionTopOffset = 10
  Font = DejaVu Sans
  FontSize = 3
  LineEndSymbol = 0
  LineMidPointSymbol = 1
  LineStartSymbol = 3
  LineStyle = 0
  LockPosition = false
  MultiRebar_LineEndSymbol = 0
  MultiRebar_LineStartSymbol = 0
  MultiRebar_OuterDimension = true
  MultiRebar_TextPositionType = 0
  ParentDrawingView = -> ReinforcementDrawingView002
  Rebar = -> Rebar
  Rotation = 0
  Scale = 0.186567
  ScaleType = 2
  SingleRebar_LineEndSymbol = 0
  SingleRebar_LineStartSymbol = 3
  SingleRebar_OuterDimension = false
  SingleRebar_TextPositionType = 1
  StrokeWidth = 0.25
  Symbol = <svg version="1.1" xmlns="http://www.w3.org/2000/svg" xmlns:xlink="http://www.w3.org/1999/xlink" xmlns:freecad="http://www.freecadweb.org/wiki/index.php?title=Svg_Namespace" width="400.0mm" height="804.0mm" viewBox="0 0 400.0 804.0"><text x="-176.0" y="-4.547473508864641e-13" style="white-space:pre;" fill="#005400" font-family="DejaVu Sans" font-size="16.08" text-anchor="middle" dominant-baseline="baseline" xml:space="preserve" transform="translate(200.0, 402.0000000000002)">STRP 14⌀8,span=1800</text></svg>
  TextPositionType = 0
  WayPoints = (2) [(0,0,0),(50,0,0)]
  WayPointsType = 0
  X = 146.012
  Y = 105
FEATURE [TechDraw::DrawViewSymbolPython] ReinforcementDimensioning027  # drawing view (typed FeaturePython)
  DimensionBottomOffset = 10
  DimensionFormat = %M %C⌀%D,span=%S
  DimensionLeftOffset = 10
  DimensionRightOffset = 10
  DimensionTopOffset = 10
  Font = DejaVu Sans
  FontSize = 3
  LineEndSymbol = 0
  LineMidPointSymbol = 1
  LineStartSymbol = 3
  LineStyle = 0
  LockPosition = false
  MultiRebar_LineEndSymbol = 0
  MultiRebar_LineStartSymbol = 0
  MultiRebar_OuterDimension = true
  MultiRebar_TextPositionType = 0
  ParentDrawingView = -> ReinforcementDrawingView002
  Rebar = -> Rebar001
  Rotation = 0
  Scale = 0.186567
  ScaleType = 2
  SingleRebar_LineEndSymbol = 0
  SingleRebar_LineStartSymbol = 3
  SingleRebar_OuterDimension = false
  SingleRebar_TextPositionType = 1
  StrokeWidth = 0.25
  Symbol = <svg version="1.1" xmlns="http://www.w3.org/2000/svg" xmlns:xlink="http://www.w3.org/1999/xlink" xmlns:freecad="http://www.freecadweb.org/wiki/index.php?title=Svg_Namespace" width="400.0mm" height="804.0mm" viewBox="0 0 400.0 804.0"><g transform="translate(200.0, 402.0000000000002)"><g><path d="M253.6 -351.0 L161.99999999999991 -351.0" style="stroke:#00007f;stroke-width:1.3399999999999999;stroke-linecap:round;fill:none;" stroke-dasharray="" /><g id="line_mid_points" /><path d="M0,0 -8,-1.5 V1.5 L0,0" style="stroke:#00007f;fill:#00007f;stroke-width:1.3399999999999999;stroke-linecap:round;stroke-linejoin:bevel;" transform="translate(161.99999999999991 -351.0) rotate(180.0 0 0)" /></g><text x="253.6" y="-342.96" style="white-space:pre;" fill="#005400" font-family="DejaVu Sans" font-size="16.08" text-anchor="start" dominant-baseline="baseline" xml:space="preserve">TLRb 1⌀20,span=0</text></g></svg>
  TextPositionType = 0
  WayPoints = (2) [(0,0,0),(50,0,0)]
  WayPointsType = 0
  X = 146.012
  Y = 105
FEATURE [TechDraw::DrawViewSymbolPython] ReinforcementDimensioning028  # drawing view (typed FeaturePython)
  DimensionBottomOffset = 10
  DimensionFormat = %M %C⌀%D,span=%S
  DimensionLeftOffset = 10
  DimensionRightOffset = 16
  DimensionTopOffset = 10
  Font = DejaVu Sans
  FontSize = 3
  LineEndSymbol = 0
  LineMidPointSymbol = 1
  LineStartSymbol = 3
  LineStyle = 0
  LockPosition = false
  MultiRebar_LineEndSymbol = 0
  MultiRebar_LineStartSymbol = 0
  MultiRebar_OuterDimension = true
  MultiRebar_TextPositionType = 0
  ParentDrawingView = -> ReinforcementDrawingView002
  Rebar = -> Rebar002
  Rotation = 0
  Scale = 0.186567
  ScaleType = 2
  SingleRebar_LineEndSymbol = 0
  SingleRebar_LineStartSymbol = 3
  SingleRebar_OuterDimension = false
  SingleRebar_TextPositionType = 1
  StrokeWidth = 0.25
  Symbol = <svg version="1.1" xmlns="http://www.w3.org/2000/svg" xmlns:xlink="http://www.w3.org/1999/xlink" xmlns:freecad="http://www.freecadweb.org/wiki/index.php?title=Svg_Namespace" width="400.0mm" height="804.0mm" viewBox="0 0 400.0 804.0"><g transform="translate(200.0, 402.0000000000002)"><g><path d="M53.33333333333323 -428.80000000000024 L53.33333333333323 -455.60000000000025 L-53.33333333333351 -455.60000000000025 L-53.33333333333351 -428.80000000000024" style="stroke:#00007f;stroke-width:1.3399999999999999;stroke-linecap:round;fill:none;" stroke-dasharray="" /><path d="M0,0 -8,-1.5 V1.5 L0,0" style="stroke:#00007f;fill:#00007f;stroke-width:1.3399999999999999;stroke-linecap:round;stroke-linejoin:bevel;" transform="translate(53.33333333333323 -428.80000000000024) rotate(90.0 0 0)" /><g id="line_mid_points"><circle cx="0" cy="0" r="2.6799999999999997" fill="#00007f" transform="translate(53.33333333333323 -455.60000000000025) rotate(-90.0 0 0)" /><circle cx="0" cy="0" r="2.6799999999999997" fill="#00007f" transform="translate(-53.33333333333351 -455.60000000000025) rotate(180.0 0 0)" /></g><path d="M0,0 -8,-1.5 V1.5 L0,0" style="stroke:#00007f;fill:#00007f;stroke-width:1.3399999999999999;stroke-linecap:round;stroke-linejoin:bevel;" transform="translate(-53.33333333333351 -428.80000000000024) rotate(90.0 0 0)" /></g><text x="-1.4210854715202004e-13" y="-458.28000000000026" style="white-space:pre;" fill="#005400" font-family="DejaVu Sans" font-size="16.08" text-anchor="middle" dominant-baseline="baseline" xml:space="preserve" transform="rotate(-0.0 -1.4210854715202004e-13 -455.60000000000025)">TLRb 2⌀16,span=107</text></g></svg>
  TextPositionType = 0
  WayPoints = (2) [(0,0,0),(50,0,0)]
  WayPointsType = 0
  X = 146.012
  Y = 105
FEATURE [TechDraw::DrawViewSymbolPython] ReinforcementDimensioning029  # drawing view (typed FeaturePython)
  DimensionBottomOffset = 10
  DimensionFormat = %M %C⌀%D,span=%S
  DimensionLeftOffset = 10
  DimensionRightOffset = 16
  DimensionTopOffset = 16
  Font = DejaVu Sans
  FontSize = 3
  LineEndSymbol = 0
  LineMidPointSymbol = 1
  LineStartSymbol = 3
  LineStyle = 0
  LockPosition = false
  MultiRebar_LineEndSymbol = 0
  MultiRebar_LineStartSymbol = 0
  MultiRebar_OuterDimension = true
  MultiRebar_TextPositionType = 0
  ParentDrawingView = -> ReinforcementDrawingView002
  Rebar = -> Rebar003
  Rotation = 0
  Scale = 0.186567
  ScaleType = 2
  SingleRebar_LineEndSymbol = 0
  SingleRebar_LineStartSymbol = 3
  SingleRebar_OuterDimension = false
  SingleRebar_TextPositionType = 1
  StrokeWidth = 0.25
  Symbol = <svg version="1.1" xmlns="http://www.w3.org/2000/svg" xmlns:xlink="http://www.w3.org/1999/xlink" xmlns:freecad="http://www.freecadweb.org/wiki/index.php?title=Svg_Namespace" width="400.0mm" height="804.0mm" viewBox="0 0 400.0 804.0"><g transform="translate(200.0, 402.0000000000002)"><g><path d="M-253.6 -326.0 L-162.00000000000006 -326.0" style="stroke:#00007f;stroke-width:1.3399999999999999;stroke-linecap:round;fill:none;" stroke-dasharray="" /><g id="line_mid_points" /><path d="M0,0 -8,-1.5 V1.5 L0,0" style="stroke:#00007f;fill:#00007f;stroke-width:1.3399999999999999;stroke-linecap:round;stroke-linejoin:bevel;" transform="translate(-162.00000000000006 -326.0) rotate(0.0 0 0)" /></g><text x="-253.6" y="-317.96" style="white-space:pre;" fill="#005400" font-family="DejaVu Sans" font-size="16.08" text-anchor="end" dominant-baseline="baseline" xml:space="preserve">TLRb 1⌀20,span=0</text></g></svg>
  TextPositionType = 0
  WayPoints = (2) [(0,0,0),(50,0,0)]
  WayPointsType = 0
  X = 146.012
  Y = 105
FEATURE [TechDraw::DrawViewSymbolPython] ReinforcementDimensioning030  # drawing view (typed FeaturePython)
  DimensionBottomOffset = 10
  DimensionFormat = %M %C⌀%D,span=%S
  DimensionLeftOffset = 16
  DimensionRightOffset = 16
  DimensionTopOffset = 16
  Font = DejaVu Sans
  FontSize = 3
  LineEndSymbol = 0
  LineMidPointSymbol = 1
  LineStartSymbol = 3
  LineStyle = 0
  LockPosition = false
  MultiRebar_LineEndSymbol = 0
  MultiRebar_LineStartSymbol = 0
  MultiRebar_OuterDimension = true
  MultiRebar_TextPositionType = 0
  ParentDrawingView = -> ReinforcementDrawingView002
  Rebar = -> Rebar004
  Rotation = 0
  Scale = 0.186567
  ScaleType = 2
  SingleRebar_LineEndSymbol = 0
  SingleRebar_LineStartSymbol = 3
  SingleRebar_OuterDimension = false
  SingleRebar_TextPositionType = 1
  StrokeWidth = 0.25
  Symbol = <svg version="1.1" xmlns="http://www.w3.org/2000/svg" xmlns:xlink="http://www.w3.org/1999/xlink" xmlns:freecad="http://www.freecadweb.org/wiki/index.php?title=Svg_Namespace" width="400.0mm" height="804.0mm" viewBox="0 0 400.0 804.0"><g transform="translate(200.0, 402.0000000000002)"><g><path d="M163.99999999999991 -460.9600000000002 L163.99999999999991 -487.7600000000002 L-1.4210854715202004e-13 -487.7600000000002 L-164.0000000000002 -487.7600000000002 L-164.0000000000002 -460.9600000000002" style="stroke:#00007f;stroke-width:1.3399999999999999;stroke-linecap:round;fill:none;" stroke-dasharray="" /><path d="M0,0 -8,-1.5 V1.5 L0,0" style="stroke:#00007f;fill:#00007f;stroke-width:1.3399999999999999;stroke-linecap:round;stroke-linejoin:bevel;" transform="translate(163.99999999999991 -460.9600000000002) rotate(90.0 0 0)" /><g id="line_mid_points"><circle cx="0" cy="0" r="2.6799999999999997" fill="#00007f" transform="translate(163.99999999999991 -487.7600000000002) rotate(-90.0 0 0)" /><circle cx="0" cy="0" r="2.6799999999999997" fill="#00007f" transform="translate(-1.4210854715202004e-13 -487.7600000000002) rotate(180.0 0 0)" /><circle cx="0" cy="0" r="2.6799999999999997" fill="#00007f" transform="translate(-164.0000000000002 -487.7600000000002) rotate(180.0 0 0)" /></g><path d="M0,0 -8,-1.5 V1.5 L0,0" style="stroke:#00007f;fill:#00007f;stroke-width:1.3399999999999999;stroke-linecap:round;stroke-linejoin:bevel;" transform="translate(-164.0000000000002 -460.9600000000002) rotate(90.0 0 0)" /></g><text x="-1.4210854715202004e-13" y="-490.4400000000002" style="white-space:pre;" fill="#005400" font-family="DejaVu Sans" font-size="16.08" text-anchor="middle" dominant-baseline="baseline" xml:space="preserve" transform="rotate(-0.0 -1.4210854715202004e-13 -487.7600000000002)">TLRb 3⌀16,span=328</text></g></svg>
  TextPositionType = 0
  WayPoints = (2) [(0,0,0),(50,0,0)]
  WayPointsType = 0
  X = 146.012
  Y = 105
FEATURE [TechDraw::DrawViewSymbolPython] ReinforcementDimensioning031  # drawing view (typed FeaturePython)
  DimensionBottomOffset = 10
  DimensionFormat = %M %C⌀%D,span=%S
  DimensionLeftOffset = 16
  DimensionRightOffset = 16
  DimensionTopOffset = 22
  Font = DejaVu Sans
  FontSize = 3
  LineEndSymbol = 0
  LineMidPointSymbol = 1
  LineStartSymbol = 3
  LineStyle = 0
  LockPosition = false
  MultiRebar_LineEndSymbol = 0
  MultiRebar_LineStartSymbol = 0
  MultiRebar_OuterDimension = true
  MultiRebar_TextPositionType = 0
  ParentDrawingView = -> ReinforcementDrawingView002
  Rebar = -> Rebar005
  Rotation = 0
  Scale = 0.186567
  ScaleType = 2
  SingleRebar_LineEndSymbol = 0
  SingleRebar_LineStartSymbol = 3
  SingleRebar_OuterDimension = false
  SingleRebar_TextPositionType = 1
  StrokeWidth = 0.25
  Symbol = <svg version="1.1" xmlns="http://www.w3.org/2000/svg" xmlns:xlink="http://www.w3.org/1999/xlink" xmlns:freecad="http://www.freecadweb.org/wiki/index.php?title=Svg_Namespace" width="400.0mm" height="804.0mm" viewBox="0 0 400.0 804.0"><g transform="translate(200.0, 402.0000000000002)"><g><path d="M285.76 320.0 L162.00000000000006 320.0" style="stroke:#00007f;stroke-width:1.3399999999999999;stroke-linecap:round;fill:none;" stroke-dasharray="" /><g id="line_mid_points" /><path d="M0,0 -8,-1.5 V1.5 L0,0" style="stroke:#00007f;fill:#00007f;stroke-width:1.3399999999999999;stroke-linecap:round;stroke-linejoin:bevel;" transform="translate(162.00000000000006 320.0) rotate(180.0 0 0)" /></g><text x="285.76" y="328.04" style="white-space:pre;" fill="#005400" font-family="DejaVu Sans" font-size="16.08" text-anchor="start" dominant-baseline="baseline" xml:space="preserve">BLRb 1⌀20,span=0</text></g></svg>
  TextPositionType = 0
  WayPoints = (2) [(0,0,0),(50,0,0)]
  WayPointsType = 0
  X = 146.012
  Y = 105
FEATURE [TechDraw::DrawViewSymbolPython] ReinforcementDimensioning032  # drawing view (typed FeaturePython)
  DimensionBottomOffset = 10
  DimensionFormat = %M %C⌀%D,span=%S
  DimensionLeftOffset = 16
  DimensionRightOffset = 22
  DimensionTopOffset = 22
  Font = DejaVu Sans
  FontSize = 3
  LineEndSymbol = 0
  LineMidPointSymbol = 1
  LineStartSymbol = 3
  LineStyle = 0
  LockPosition = false
  MultiRebar_LineEndSymbol = 0
  MultiRebar_LineStartSymbol = 0
  MultiRebar_OuterDimension = true
  MultiRebar_TextPositionType = 0
  ParentDrawingView = -> ReinforcementDrawingView002
  Rebar = -> Rebar006
  Rotation = 0
  Scale = 0.186567
  ScaleType = 2
  SingleRebar_LineEndSymbol = 0
  SingleRebar_LineStartSymbol = 3
  SingleRebar_OuterDimension = false
  SingleRebar_TextPositionType = 1
  StrokeWidth = 0.25
  Symbol = <svg version="1.1" xmlns="http://www.w3.org/2000/svg" xmlns:xlink="http://www.w3.org/1999/xlink" xmlns:freecad="http://www.freecadweb.org/wiki/index.php?title=Svg_Namespace" width="400.0mm" height="804.0mm" viewBox="0 0 400.0 804.0"><g transform="translate(200.0, 402.0000000000002)"><g><path d="M53.3333333333334 428.7999999999998 L53.3333333333334 455.5999999999998 L-53.33333333333334 455.5999999999998 L-53.33333333333334 428.7999999999998" style="stroke:#00007f;stroke-width:1.3399999999999999;stroke-linecap:round;fill:none;" stroke-dasharray="" /><path d="M0,0 -8,-1.5 V1.5 L0,0" style="stroke:#00007f;fill:#00007f;stroke-width:1.3399999999999999;stroke-linecap:round;stroke-linejoin:bevel;" transform="translate(53.3333333333334 428.7999999999998) rotate(-90.0 0 0)" /><g id="line_mid_points"><circle cx="0" cy="0" r="2.6799999999999997" fill="#00007f" transform="translate(53.3333333333334 455.5999999999998) rotate(90.0 0 0)" /><circle cx="0" cy="0" r="2.6799999999999997" fill="#00007f" transform="translate(-53.33333333333334 455.5999999999998) rotate(180.0 0 0)" /></g><path d="M0,0 -8,-1.5 V1.5 L0,0" style="stroke:#00007f;fill:#00007f;stroke-width:1.3399999999999999;stroke-linecap:round;stroke-linejoin:bevel;" transform="translate(-53.33333333333334 428.7999999999998) rotate(-90.0 0 0)" /></g><text x="2.842170943040401e-14" y="452.9199999999998" style="white-space:pre;" fill="#005400" font-family="DejaVu Sans" font-size="16.08" text-anchor="middle" dominant-baseline="baseline" xml:space="preserve" transform="rotate(-0.0 2.842170943040401e-14 455.5999999999998)">BLRb 2⌀16,span=107</text></g></svg>
  TextPositionType = 0
  WayPoints = (2) [(0,0,0),(50,0,0)]
  WayPointsType = 0
  X = 146.012
  Y = 105
FEATURE [TechDraw::DrawViewSymbolPython] ReinforcementDimensioning033  # drawing view (typed FeaturePython)
  DimensionBottomOffset = 16
  DimensionFormat = %M %C⌀%D,span=%S
  DimensionLeftOffset = 16
  DimensionRightOffset = 22
  DimensionTopOffset = 22
  Font = DejaVu Sans
  FontSize = 3
  LineEndSymbol = 0
  LineMidPointSymbol = 1
  LineStartSymbol = 3
  LineStyle = 0
  LockPosition = false
  MultiRebar_LineEndSymbol = 0
  MultiRebar_LineStartSymbol = 0
  MultiRebar_OuterDimension = true
  MultiRebar_TextPositionType = 0
  ParentDrawingView = -> ReinforcementDrawingView002
  Rebar = -> Rebar007
  Rotation = 0
  Scale = 0.186567
  ScaleType = 2
  SingleRebar_LineEndSymbol = 0
  SingleRebar_LineStartSymbol = 3
  SingleRebar_OuterDimension = false
  SingleRebar_TextPositionType = 1
  StrokeWidth = 0.25
  Symbol = <svg version="1.1" xmlns="http://www.w3.org/2000/svg" xmlns:xlink="http://www.w3.org/1999/xlink" xmlns:freecad="http://www.freecadweb.org/wiki/index.php?title=Svg_Namespace" width="400.0mm" height="804.0mm" viewBox="0 0 400.0 804.0"><g transform="translate(200.0, 402.0000000000002)"><g><path d="M-285.76 328.0 L-161.99999999999994 328.0" style="stroke:#00007f;stroke-width:1.3399999999999999;stroke-linecap:round;fill:none;" stroke-dasharray="" /><g id="line_mid_points" /><path d="M0,0 -8,-1.5 V1.5 L0,0" style="stroke:#00007f;fill:#00007f;stroke-width:1.3399999999999999;stroke-linecap:round;stroke-linejoin:bevel;" transform="translate(-161.99999999999994 328.0) rotate(0.0 0 0)" /></g><text x="-285.76" y="336.04" style="white-space:pre;" fill="#005400" font-family="DejaVu Sans" font-size="16.08" text-anchor="end" dominant-baseline="baseline" xml:space="preserve">BLRb 1⌀20,span=0</text></g></svg>
  TextPositionType = 0
  WayPoints = (2) [(0,0,0),(50,0,0)]
  WayPointsType = 0
  X = 146.012
  Y = 105
FEATURE [TechDraw::DrawViewSymbolPython] ReinforcementDimensioning034  # drawing view (typed FeaturePython)
  DimensionBottomOffset = 16
  DimensionFormat = %M %C⌀%D,span=%S
  DimensionLeftOffset = 22
  DimensionRightOffset = 22
  DimensionTopOffset = 22
  Font = DejaVu Sans
  FontSize = 3
  LineEndSymbol = 0
  LineMidPointSymbol = 1
  LineStartSymbol = 3
  LineStyle = 0
  LockPosition = false
  MultiRebar_LineEndSymbol = 0
  MultiRebar_LineStartSymbol = 0
  MultiRebar_OuterDimension = true
  MultiRebar_TextPositionType = 0
  ParentDrawingView = -> ReinforcementDrawingView002
  Rebar = -> Rebar008
  Rotation = 0
  Scale = 0.186567
  ScaleType = 2
  SingleRebar_LineEndSymbol = 0
  SingleRebar_LineStartSymbol = 3
  SingleRebar_OuterDimension = false
  SingleRebar_TextPositionType = 1
  StrokeWidth = 0.25
  Symbol = <svg version="1.1" xmlns="http://www.w3.org/2000/svg" xmlns:xlink="http://www.w3.org/1999/xlink" xmlns:freecad="http://www.freecadweb.org/wiki/index.php?title=Svg_Namespace" width="400.0mm" height="804.0mm" viewBox="0 0 400.0 804.0"><g transform="translate(200.0, 402.0000000000002)"><g><path d="M164.00000000000006 460.9599999999998 L164.00000000000006 487.7599999999998 L-0.0 487.7599999999998 L-164.00000000000006 487.7599999999998 L-164.00000000000006 460.9599999999998" style="stroke:#00007f;stroke-width:1.3399999999999999;stroke-linecap:round;fill:none;" stroke-dasharray="" /><path d="M0,0 -8,-1.5 V1.5 L0,0" style="stroke:#00007f;fill:#00007f;stroke-width:1.3399999999999999;stroke-linecap:round;stroke-linejoin:bevel;" transform="translate(164.00000000000006 460.9599999999998) rotate(-90.0 0 0)" /><g id="line_mid_points"><circle cx="0" cy="0" r="2.6799999999999997" fill="#00007f" transform="translate(164.00000000000006 487.7599999999998) rotate(90.0 0 0)" /><circle cx="0" cy="0" r="2.6799999999999997" fill="#00007f" transform="translate(-0.0 487.7599999999998) rotate(180.0 0 0)" /><circle cx="0" cy="0" r="2.6799999999999997" fill="#00007f" transform="translate(-164.00000000000006 487.7599999999998) rotate(180.0 0 0)" /></g><path d="M0,0 -8,-1.5 V1.5 L0,0" style="stroke:#00007f;fill:#00007f;stroke-width:1.3399999999999999;stroke-linecap:round;stroke-linejoin:bevel;" transform="translate(-164.00000000000006 460.9599999999998) rotate(-90.0 0 0)" /></g><text x="-0.0" y="485.0799999999998" style="white-space:pre;" fill="#005400" font-family="DejaVu Sans" font-size="16.08" text-anchor="middle" dominant-baseline="baseline" xml:space="preserve" transform="rotate(-0.0 -0.0 487.7599999999998)">BLRb 3⌀16,span=328</text></g></svg>
  TextPositionType = 0
  WayPoints = (2) [(0,0,0),(50,0,0)]
  WayPointsType = 0
  X = 146.012
  Y = 105
FEATURE [TechDraw::DrawViewSymbolPython] ReinforcementDimensioning035  # drawing view (typed FeaturePython)
  DimensionBottomOffset = 22
  DimensionFormat = %M %C⌀%D,span=%S
  DimensionLeftOffset = 22
  DimensionRightOffset = 22
  DimensionTopOffset = 22
  Font = DejaVu Sans
  FontSize = 3
  LineEndSymbol = 0
  LineMidPointSymbol = 1
  LineStartSymbol = 3
  LineStyle = 0
  LockPosition = false
  MultiRebar_LineEndSymbol = 0
  MultiRebar_LineStartSymbol = 0
  MultiRebar_OuterDimension = true
  MultiRebar_TextPositionType = 0
  ParentDrawingView = -> ReinforcementDrawingView002
  Rebar = -> Rebar009
  Rotation = 0
  Scale = 0.186567
  ScaleType = 2
  SingleRebar_LineEndSymbol = 0
  SingleRebar_LineStartSymbol = 3
  SingleRebar_OuterDimension = false
  SingleRebar_TextPositionType = 1
  StrokeWidth = 0.25
  Symbol = <svg version="1.1" xmlns="http://www.w3.org/2000/svg" xmlns:xlink="http://www.w3.org/1999/xlink" xmlns:freecad="http://www.freecadweb.org/wiki/index.php?title=Svg_Namespace" width="400.0mm" height="804.0mm" viewBox="0 0 400.0 804.0"><g transform="translate(200.0, 402.0000000000002)"><g><path d="M70.0 519.9199999999998 L70.0 46.0" style="stroke:#00007f;stroke-width:1.3399999999999999;stroke-linecap:round;fill:none;" stroke-dasharray="" /><g id="line_mid_points" /><path d="M0,0 -8,-1.5 V1.5 L0,0" style="stroke:#00007f;fill:#00007f;stroke-width:1.3399999999999999;stroke-linecap:round;stroke-linejoin:bevel;" transform="translate(70.0 46.0) rotate(-90.0 0 0)" /></g><text x="70.0" y="527.9599999999998" style="white-space:pre;" fill="#005400" font-family="DejaVu Sans" font-size="16.08" text-anchor="middle" dominant-baseline="baseline" xml:space="preserve">LLRb 1⌀16,span=0</text></g></svg>
  TextPositionType = 0
  WayPoints = (2) [(0,0,0),(50,0,0)]
  WayPointsType = 0
  X = 146.012
  Y = 105
FEATURE [TechDraw::DrawViewSymbolPython] ReinforcementDimensioning036  # drawing view (typed FeaturePython)
  DimensionBottomOffset = 28
  DimensionFormat = %M %C⌀%D,span=%S
  DimensionLeftOffset = 22
  DimensionRightOffset = 22
  DimensionTopOffset = 22
  Font = DejaVu Sans
  FontSize = 3
  LineEndSymbol = 0
  LineMidPointSymbol = 1
  LineStartSymbol = 3
  LineStyle = 0
  LockPosition = false
  MultiRebar_LineEndSymbol = 0
  MultiRebar_LineStartSymbol = 0
  MultiRebar_OuterDimension = true
  MultiRebar_TextPositionType = 0
  ParentDrawingView = -> ReinforcementDrawingView002
  Rebar = -> Rebar010
  Rotation = 0
  Scale = 0.186567
  ScaleType = 2
  SingleRebar_LineEndSymbol = 0
  SingleRebar_LineStartSymbol = 3
  SingleRebar_OuterDimension = false
  SingleRebar_TextPositionType = 1
  StrokeWidth = 0.25
  Symbol = <svg version="1.1" xmlns="http://www.w3.org/2000/svg" xmlns:xlink="http://www.w3.org/1999/xlink" xmlns:freecad="http://www.freecadweb.org/wiki/index.php?title=Svg_Namespace" width="400.0mm" height="804.0mm" viewBox="0 0 400.0 804.0"><g transform="translate(200.0, 402.0000000000002)"><g><path d="M136.0 -519.9200000000002 L136.0 -4.547473508864641e-13" style="stroke:#00007f;stroke-width:1.3399999999999999;stroke-linecap:round;fill:none;" stroke-dasharray="" /><g id="line_mid_points" /><path d="M0,0 -8,-1.5 V1.5 L0,0" style="stroke:#00007f;fill:#00007f;stroke-width:1.3399999999999999;stroke-linecap:round;stroke-linejoin:bevel;" transform="translate(136.0 -4.547473508864641e-13) rotate(90.0 0 0)" /></g><text x="136.0" y="-519.9200000000002" style="white-space:pre;" fill="#005400" font-family="DejaVu Sans" font-size="16.08" text-anchor="middle" dominant-baseline="baseline" xml:space="preserve">LLRb 1⌀16,span=0</text></g></svg>
  TextPositionType = 0
  WayPoints = (2) [(0,0,0),(50,0,0)]
  WayPointsType = 0
  X = 146.012
  Y = 105
FEATURE [TechDraw::DrawViewSymbolPython] ReinforcementDimensioning037  # drawing view (typed FeaturePython)
  DimensionBottomOffset = 28
  DimensionFormat = %M %C⌀%D,span=%S
  DimensionLeftOffset = 22
  DimensionRightOffset = 22
  DimensionTopOffset = 28
  Font = DejaVu Sans
  FontSize = 3
  LineEndSymbol = 0
  LineMidPointSymbol = 1
  LineStartSymbol = 3
  LineStyle = 0
  LockPosition = false
  MultiRebar_LineEndSymbol = 0
  MultiRebar_LineStartSymbol = 0
  MultiRebar_OuterDimension = true
  MultiRebar_TextPositionType = 0
  ParentDrawingView = -> ReinforcementDrawingView002
  Rebar = -> Rebar011
  Rotation = 0
  Scale = 0.186567
  ScaleType = 2
  SingleRebar_LineEndSymbol = 0
  SingleRebar_LineStartSymbol = 3
  SingleRebar_OuterDimension = false
  SingleRebar_TextPositionType = 1
  StrokeWidth = 0.25
  Symbol = <svg version="1.1" xmlns="http://www.w3.org/2000/svg" xmlns:xlink="http://www.w3.org/1999/xlink" xmlns:freecad="http://www.freecadweb.org/wiki/index.php?title=Svg_Namespace" width="400.0mm" height="804.0mm" viewBox="0 0 400.0 804.0"><g transform="translate(200.0, 402.0000000000002)"><g><path d="M63.0 -552.0800000000002 L63.0 -46.0" style="stroke:#00007f;stroke-width:1.3399999999999999;stroke-linecap:round;fill:none;" stroke-dasharray="" /><g id="line_mid_points" /><path d="M0,0 -8,-1.5 V1.5 L0,0" style="stroke:#00007f;fill:#00007f;stroke-width:1.3399999999999999;stroke-linecap:round;stroke-linejoin:bevel;" transform="translate(63.0 -46.0) rotate(90.0 0 0)" /></g><text x="63.0" y="-552.0800000000002" style="white-space:pre;" fill="#005400" font-family="DejaVu Sans" font-size="16.08" text-anchor="middle" dominant-baseline="baseline" xml:space="preserve">LLRb 1⌀16,span=0</text></g></svg>
  TextPositionType = 0
  WayPoints = (2) [(0,0,0),(50,0,0)]
  WayPointsType = 0
  X = 146.012
  Y = 105
FEATURE [TechDraw::DrawViewSymbolPython] ReinforcementDimensioning038  # drawing view (typed FeaturePython)
  DimensionBottomOffset = 28
  DimensionFormat = %M %C⌀%D,span=%S
  DimensionLeftOffset = 22
  DimensionRightOffset = 22
  DimensionTopOffset = 34
  Font = DejaVu Sans
  FontSize = 3
  LineEndSymbol = 0
  LineMidPointSymbol = 1
  LineStartSymbol = 3
  LineStyle = 0
  LockPosition = false
  MultiRebar_LineEndSymbol = 0
  MultiRebar_LineStartSymbol = 0
  MultiRebar_OuterDimension = true
  MultiRebar_TextPositionType = 0
  ParentDrawingView = -> ReinforcementDrawingView002
  Rebar = -> Rebar012
  Rotation = 0
  Scale = 0.186567
  ScaleType = 2
  SingleRebar_LineEndSymbol = 0
  SingleRebar_LineStartSymbol = 3
  SingleRebar_OuterDimension = false
  SingleRebar_TextPositionType = 1
  StrokeWidth = 0.25
  Symbol = <svg version="1.1" xmlns="http://www.w3.org/2000/svg" xmlns:xlink="http://www.w3.org/1999/xlink" xmlns:freecad="http://www.freecadweb.org/wiki/index.php?title=Svg_Namespace" width="400.0mm" height="804.0mm" viewBox="0 0 400.0 804.0"><g transform="translate(200.0, 402.0000000000002)"><g><path d="M-98.0 552.0799999999998 L-98.0 45.999999999999545" style="stroke:#00007f;stroke-width:1.3399999999999999;stroke-linecap:round;fill:none;" stroke-dasharray="" /><g id="line_mid_points" /><path d="M0,0 -8,-1.5 V1.5 L0,0" style="stroke:#00007f;fill:#00007f;stroke-width:1.3399999999999999;stroke-linecap:round;stroke-linejoin:bevel;" transform="translate(-98.0 45.999999999999545) rotate(-90.0 0 0)" /></g><text x="-98.0" y="560.1199999999998" style="white-space:pre;" fill="#005400" font-family="DejaVu Sans" font-size="16.08" text-anchor="middle" dominant-baseline="baseline" xml:space="preserve">RLRb 1⌀16,span=0</text></g></svg>
  TextPositionType = 0
  WayPoints = (2) [(0,0,0),(50,0,0)]
  WayPointsType = 0
  X = 146.012
  Y = 105
FEATURE [TechDraw::DrawViewSymbolPython] ReinforcementDimensioning039  # drawing view (typed FeaturePython)
  DimensionBottomOffset = 34
  DimensionFormat = %M %C⌀%D,span=%S
  DimensionLeftOffset = 22
  DimensionRightOffset = 22
  DimensionTopOffset = 34
  Font = DejaVu Sans
  FontSize = 3
  LineEndSymbol = 0
  LineMidPointSymbol = 1
  LineStartSymbol = 3
  LineStyle = 0
  LockPosition = false
  MultiRebar_LineEndSymbol = 0
  MultiRebar_LineStartSymbol = 0
  MultiRebar_OuterDimension = true
  MultiRebar_TextPositionType = 0
  ParentDrawingView = -> ReinforcementDrawingView002
  Rebar = -> Rebar013
  Rotation = 0
  Scale = 0.186567
  ScaleType = 2
  SingleRebar_LineEndSymbol = 0
  SingleRebar_LineStartSymbol = 3
  SingleRebar_OuterDimension = false
  SingleRebar_TextPositionType = 1
  StrokeWidth = 0.25
  Symbol = <svg version="1.1" xmlns="http://www.w3.org/2000/svg" xmlns:xlink="http://www.w3.org/1999/xlink" xmlns:freecad="http://www.freecadweb.org/wiki/index.php?title=Svg_Namespace" width="400.0mm" height="804.0mm" viewBox="0 0 400.0 804.0"><g transform="translate(200.0, 402.0000000000002)"><g><path d="M-63.0 584.2399999999998 L-63.0 0.0" style="stroke:#00007f;stroke-width:1.3399999999999999;stroke-linecap:round;fill:none;" stroke-dasharray="" /><g id="line_mid_points" /><path d="M0,0 -8,-1.5 V1.5 L0,0" style="stroke:#00007f;fill:#00007f;stroke-width:1.3399999999999999;stroke-linecap:round;stroke-linejoin:bevel;" transform="translate(-63.0 0.0) rotate(-90.0 0 0)" /></g><text x="-63.0" y="592.2799999999997" style="white-space:pre;" fill="#005400" font-family="DejaVu Sans" font-size="16.08" text-anchor="middle" dominant-baseline="baseline" xml:space="preserve">RLRb 1⌀16,span=0</text></g></svg>
  TextPositionType = 0
  WayPoints = (2) [(0,0,0),(50,0,0)]
  WayPointsType = 0
  X = 146.012
  Y = 105
FEATURE [TechDraw::DrawViewSymbolPython] ReinforcementDimensioning040  # drawing view (typed FeaturePython)
  DimensionBottomOffset = 40
  DimensionFormat = %M %C⌀%D,span=%S
  DimensionLeftOffset = 22
  DimensionRightOffset = 22
  DimensionTopOffset = 34
  Font = DejaVu Sans
  FontSize = 3
  LineEndSymbol = 0
  LineMidPointSymbol = 1
  LineStartSymbol = 3
  LineStyle = 0
  LockPosition = false
  MultiRebar_LineEndSymbol = 0
  MultiRebar_LineStartSymbol = 0
  MultiRebar_OuterDimension = true
  MultiRebar_TextPositionType = 0
  ParentDrawingView = -> ReinforcementDrawingView002
  Rebar = -> Rebar014
  Rotation = 0
  Scale = 0.186567
  ScaleType = 2
  SingleRebar_LineEndSymbol = 0
  SingleRebar_LineStartSymbol = 3
  SingleRebar_OuterDimension = false
  SingleRebar_TextPositionType = 1
  StrokeWidth = 0.25
  Symbol = <svg version="1.1" xmlns="http://www.w3.org/2000/svg" xmlns:xlink="http://www.w3.org/1999/xlink" xmlns:freecad="http://www.freecadweb.org/wiki/index.php?title=Svg_Namespace" width="400.0mm" height="804.0mm" viewBox="0 0 400.0 804.0"><g transform="translate(200.0, 402.0000000000002)"><g><path d="M-94.0 -584.2400000000002 L-94.0 -46.000000000000455" style="stroke:#00007f;stroke-width:1.3399999999999999;stroke-linecap:round;fill:none;" stroke-dasharray="" /><g id="line_mid_points" /><path d="M0,0 -8,-1.5 V1.5 L0,0" style="stroke:#00007f;fill:#00007f;stroke-width:1.3399999999999999;stroke-linecap:round;stroke-linejoin:bevel;" transform="translate(-94.0 -46.000000000000455) rotate(90.0 0 0)" /></g><text x="-94.0" y="-584.2400000000002" style="white-space:pre;" fill="#005400" font-family="DejaVu Sans" font-size="16.08" text-anchor="middle" dominant-baseline="baseline" xml:space="preserve">RLRb 1⌀16,span=0</text></g></svg>
  TextPositionType = 0
  WayPoints = (2) [(0,0,0),(50,0,0)]
  WayPointsType = 0
  X = 146.012
  Y = 105
FEATURE [TechDraw::DrawPage] TechDraw__DrawPage002  label="Beam Drawing002"
  KeepUpdated = true
  NextBalloonIndex = 1
  ProjectionType = 0
  Template = -> Template002
  Views = -> [ReinforcementDrawingView002,ReinforcementDimensioning026,ReinforcementDimensioning027,ReinforcementDimensioning028,ReinforcementDimensioning029,ReinforcementDimensioning030,ReinforcementDimensioning031,ReinforcementDimensioning032,ReinforcementDimensioning033,ReinforcementDimensioning034,ReinforcementDimensioning035,ReinforcementDimensioning036,ReinforcementDimensioning037,+3 more]
FEATURE [TechDraw::DrawSVGTemplate] Template003
  Height = 210
  Orientation = 1
  Width = 297
FEATURE [TechDraw::DrawViewSymbolPython] ReinforcementDrawingView003  label="Right View"  # drawing view (typed FeaturePython)
  DimensionBottomOffset = 40
  DimensionLeftOffset = 22
  DimensionRightOffset = 22
  DimensionTopOffset = 40
  Height = 804
  LeftOffset = 111.187
  LockPosition = false
  MaxHeight = 210
  MaxWidth = 297
  MinBottomOffset = 30
  MinRightOffset = 20
  PositionType = 0
  Rebars = -> [Rebar,Rebar001,Rebar002,Rebar003,Rebar004,Rebar005,Rebar006,Rebar007,Rebar008,Rebar009,Rebar010,Rebar011,Rebar012,Rebar013,Rebar014]
  RebarsColorStyle = 0
  RebarsStrokeWidth = 0.35
  Rotation = 0
  Scale = 0.186567
  ScaleType = 1
  Structure = -> Structure
  StructureColorStyle = 0
  StructureStrokeWidth = 0.5
  Symbol = <blob: 10182 chars omitted>
  Template = -> Template003
  TopOffset = 30
  View = 3
  VisibleRebars = -> [Rebar,Rebar001,Rebar002,Rebar003,Rebar004,Rebar005,Rebar006,Rebar007,Rebar008,Rebar009,Rebar010,Rebar011,Rebar012,Rebar013,Rebar014]
  Width = 400
  X = 148.5
  Y = 105
  expr: LeftOffset = .Template.Width.Value / 2 - .Width.Value * .Scale / 2
FEATURE [TechDraw::DrawViewSymbolPython] ReinforcementDimensioning041  # drawing view (typed FeaturePython)
  DimensionBottomOffset = 10
  DimensionFormat = %M %C⌀%D,span=%S
  DimensionLeftOffset = 10
  DimensionRightOffset = 10
  DimensionTopOffset = 10
  Font = DejaVu Sans
  FontSize = 3
  LineEndSymbol = 0
  LineMidPointSymbol = 1
  LineStartSymbol = 3
  LineStyle = 0
  LockPosition = false
  MultiRebar_LineEndSymbol = 0
  MultiRebar_LineStartSymbol = 0
  MultiRebar_OuterDimension = true
  MultiRebar_TextPositionType = 0
  ParentDrawingView = -> ReinforcementDrawingView003
  Rebar = -> Rebar
  Rotation = 0
  Scale = 0.186567
  ScaleType = 2
  SingleRebar_LineEndSymbol = 0
  SingleRebar_LineStartSymbol = 3
  SingleRebar_OuterDimension = false
  SingleRebar_TextPositionType = 1
  StrokeWidth = 0.25
  Symbol = <svg version="1.1" xmlns="http://www.w3.org/2000/svg" xmlns:xlink="http://www.w3.org/1999/xlink" xmlns:freecad="http://www.freecadweb.org/wiki/index.php?title=Svg_Namespace" width="400.0mm" height="804.0mm" viewBox="0 0 400.0 804.0"><text x="176.0" y="-4.547473508864641e-13" style="white-space:pre;" fill="#005400" font-family="DejaVu Sans" font-size="16.08" text-anchor="middle" dominant-baseline="baseline" xml:space="preserve" transform="translate(200.0, 402.0000000000002)">STRP 14⌀8,span=1800</text></svg>
  TextPositionType = 0
  WayPoints = (2) [(0,0,0),(50,0,0)]
  WayPointsType = 0
  X = 148.5
  Y = 105
FEATURE [TechDraw::DrawViewSymbolPython] ReinforcementDimensioning042  # drawing view (typed FeaturePython)
  DimensionBottomOffset = 10
  DimensionFormat = %M %C⌀%D,span=%S
  DimensionLeftOffset = 10
  DimensionRightOffset = 10
  DimensionTopOffset = 10
  Font = DejaVu Sans
  FontSize = 3
  LineEndSymbol = 0
  LineMidPointSymbol = 1
  LineStartSymbol = 3
  LineStyle = 0
  LockPosition = false
  MultiRebar_LineEndSymbol = 0
  MultiRebar_LineStartSymbol = 0
  MultiRebar_OuterDimension = true
  MultiRebar_TextPositionType = 0
  ParentDrawingView = -> ReinforcementDrawingView003
  Rebar = -> Rebar001
  Rotation = 0
  Scale = 0.186567
  ScaleType = 2
  SingleRebar_LineEndSymbol = 0
  SingleRebar_LineStartSymbol = 3
  SingleRebar_OuterDimension = false
  SingleRebar_TextPositionType = 1
  StrokeWidth = 0.25
  Symbol = <svg version="1.1" xmlns="http://www.w3.org/2000/svg" xmlns:xlink="http://www.w3.org/1999/xlink" xmlns:freecad="http://www.freecadweb.org/wiki/index.php?title=Svg_Namespace" width="400.0mm" height="804.0mm" viewBox="0 0 400.0 804.0"><g transform="translate(200.0, 402.0000000000002)"><g><path d="M-253.6 -277.0 L-161.99999999999994 -277.0" style="stroke:#00007f;stroke-width:1.3399999999999999;stroke-linecap:round;fill:none;" stroke-dasharray="" /><g id="line_mid_points" /><path d="M0,0 -8,-1.5 V1.5 L0,0" style="stroke:#00007f;fill:#00007f;stroke-width:1.3399999999999999;stroke-linecap:round;stroke-linejoin:bevel;" transform="translate(-161.99999999999994 -277.0) rotate(0.0 0 0)" /></g><text x="-253.6" y="-268.96" style="white-space:pre;" fill="#005400" font-family="DejaVu Sans" font-size="16.08" text-anchor="end" dominant-baseline="baseline" xml:space="preserve">TLRb 1⌀20,span=0</text></g></svg>
  TextPositionType = 0
  WayPoints = (2) [(0,0,0),(50,0,0)]
  WayPointsType = 0
  X = 148.5
  Y = 105
FEATURE [TechDraw::DrawViewSymbolPython] ReinforcementDimensioning043  # drawing view (typed FeaturePython)
  DimensionBottomOffset = 10
  DimensionFormat = %M %C⌀%D,span=%S
  DimensionLeftOffset = 16
  DimensionRightOffset = 10
  DimensionTopOffset = 10
  Font = DejaVu Sans
  FontSize = 3
  LineEndSymbol = 0
  LineMidPointSymbol = 1
  LineStartSymbol = 3
  LineStyle = 0
  LockPosition = false
  MultiRebar_LineEndSymbol = 0
  MultiRebar_LineStartSymbol = 0
  MultiRebar_OuterDimension = true
  MultiRebar_TextPositionType = 0
  ParentDrawingView = -> ReinforcementDrawingView003
  Rebar = -> Rebar002
  Rotation = 0
  Scale = 0.186567
  ScaleType = 2
  SingleRebar_LineEndSymbol = 0
  SingleRebar_LineStartSymbol = 3
  SingleRebar_OuterDimension = false
  SingleRebar_TextPositionType = 1
  StrokeWidth = 0.25
  Symbol = <svg version="1.1" xmlns="http://www.w3.org/2000/svg" xmlns:xlink="http://www.w3.org/1999/xlink" xmlns:freecad="http://www.freecadweb.org/wiki/index.php?title=Svg_Namespace" width="400.0mm" height="804.0mm" viewBox="0 0 400.0 804.0"><g transform="translate(200.0, 402.0000000000002)"><g><path d="M-53.33333333333323 -428.80000000000024 L-53.33333333333323 -455.60000000000025 L53.33333333333351 -455.60000000000025 L53.33333333333351 -428.80000000000024" style="stroke:#00007f;stroke-width:1.3399999999999999;stroke-linecap:round;fill:none;" stroke-dasharray="" /><path d="M0,0 -8,-1.5 V1.5 L0,0" style="stroke:#00007f;fill:#00007f;stroke-width:1.3399999999999999;stroke-linecap:round;stroke-linejoin:bevel;" transform="translate(-53.33333333333323 -428.80000000000024) rotate(90.0 0 0)" /><g id="line_mid_points"><circle cx="0" cy="0" r="2.6799999999999997" fill="#00007f" transform="translate(-53.33333333333323 -455.60000000000025) rotate(-90.0 0 0)" /><circle cx="0" cy="0" r="2.6799999999999997" fill="#00007f" transform="translate(53.33333333333351 -455.60000000000025) rotate(0.0 0 0)" /></g><path d="M0,0 -8,-1.5 V1.5 L0,0" style="stroke:#00007f;fill:#00007f;stroke-width:1.3399999999999999;stroke-linecap:round;stroke-linejoin:bevel;" transform="translate(53.33333333333351 -428.80000000000024) rotate(90.0 0 0)" /></g><text x="1.4210854715202004e-13" y="-458.28000000000026" style="white-space:pre;" fill="#005400" font-family="DejaVu Sans" font-size="16.08" text-anchor="middle" dominant-baseline="baseline" xml:space="preserve" transform="rotate(0.0 1.4210854715202004e-13 -455.60000000000025)">TLRb 2⌀16,span=107</text></g></svg>
  TextPositionType = 0
  WayPoints = (2) [(0,0,0),(50,0,0)]
  WayPointsType = 0
  X = 148.5
  Y = 105
FEATURE [TechDraw::DrawViewSymbolPython] ReinforcementDimensioning044  # drawing view (typed FeaturePython)
  DimensionBottomOffset = 10
  DimensionFormat = %M %C⌀%D,span=%S
  DimensionLeftOffset = 16
  DimensionRightOffset = 10
  DimensionTopOffset = 16
  Font = DejaVu Sans
  FontSize = 3
  LineEndSymbol = 0
  LineMidPointSymbol = 1
  LineStartSymbol = 3
  LineStyle = 0
  LockPosition = false
  MultiRebar_LineEndSymbol = 0
  MultiRebar_LineStartSymbol = 0
  MultiRebar_OuterDimension = true
  MultiRebar_TextPositionType = 0
  ParentDrawingView = -> ReinforcementDrawingView003
  Rebar = -> Rebar003
  Rotation = 0
  Scale = 0.186567
  ScaleType = 2
  SingleRebar_LineEndSymbol = 0
  SingleRebar_LineStartSymbol = 3
  SingleRebar_OuterDimension = false
  SingleRebar_TextPositionType = 1
  StrokeWidth = 0.25
  Symbol = <svg version="1.1" xmlns="http://www.w3.org/2000/svg" xmlns:xlink="http://www.w3.org/1999/xlink" xmlns:freecad="http://www.freecadweb.org/wiki/index.php?title=Svg_Namespace" width="400.0mm" height="804.0mm" viewBox="0 0 400.0 804.0"><g transform="translate(200.0, 402.0000000000002)"><g><path d="M253.6 -400.0 L162.00000000000009 -400.0" style="stroke:#00007f;stroke-width:1.3399999999999999;stroke-linecap:round;fill:none;" stroke-dasharray="" /><g id="line_mid_points" /><path d="M0,0 -8,-1.5 V1.5 L0,0" style="stroke:#00007f;fill:#00007f;stroke-width:1.3399999999999999;stroke-linecap:round;stroke-linejoin:bevel;" transform="translate(162.00000000000009 -400.0) rotate(180.0 0 0)" /></g><text x="253.6" y="-391.96" style="white-space:pre;" fill="#005400" font-family="DejaVu Sans" font-size="16.08" text-anchor="start" dominant-baseline="baseline" xml:space="preserve">TLRb 1⌀20,span=0</text></g></svg>
  TextPositionType = 0
  WayPoints = (2) [(0,0,0),(50,0,0)]
  WayPointsType = 0
  X = 148.5
  Y = 105
FEATURE [TechDraw::DrawViewSymbolPython] ReinforcementDimensioning045  # drawing view (typed FeaturePython)
  DimensionBottomOffset = 10
  DimensionFormat = %M %C⌀%D,span=%S
  DimensionLeftOffset = 16
  DimensionRightOffset = 16
  DimensionTopOffset = 16
  Font = DejaVu Sans
  FontSize = 3
  LineEndSymbol = 0
  LineMidPointSymbol = 1
  LineStartSymbol = 3
  LineStyle = 0
  LockPosition = false
  MultiRebar_LineEndSymbol = 0
  MultiRebar_LineStartSymbol = 0
  MultiRebar_OuterDimension = true
  MultiRebar_TextPositionType = 0
  ParentDrawingView = -> ReinforcementDrawingView003
  Rebar = -> Rebar004
  Rotation = 0
  Scale = 0.186567
  ScaleType = 2
  SingleRebar_LineEndSymbol = 0
  SingleRebar_LineStartSymbol = 3
  SingleRebar_OuterDimension = false
  SingleRebar_TextPositionType = 1
  StrokeWidth = 0.25
  Symbol = <svg version="1.1" xmlns="http://www.w3.org/2000/svg" xmlns:xlink="http://www.w3.org/1999/xlink" xmlns:freecad="http://www.freecadweb.org/wiki/index.php?title=Svg_Namespace" width="400.0mm" height="804.0mm" viewBox="0 0 400.0 804.0"><g transform="translate(200.0, 402.0000000000002)"><g><path d="M-163.99999999999991 -460.9600000000002 L-163.99999999999991 -487.7600000000002 L-1.4210854715202004e-13 -487.7600000000002 L164.0000000000002 -487.7600000000002 L164.0000000000002 -460.9600000000002" style="stroke:#00007f;stroke-width:1.3399999999999999;stroke-linecap:round;fill:none;" stroke-dasharray="" /><path d="M0,0 -8,-1.5 V1.5 L0,0" style="stroke:#00007f;fill:#00007f;stroke-width:1.3399999999999999;stroke-linecap:round;stroke-linejoin:bevel;" transform="translate(-163.99999999999991 -460.9600000000002) rotate(90.0 0 0)" /><g id="line_mid_points"><circle cx="0" cy="0" r="2.6799999999999997" fill="#00007f" transform="translate(-163.99999999999991 -487.7600000000002) rotate(-90.0 0 0)" /><circle cx="0" cy="0" r="2.6799999999999997" fill="#00007f" transform="translate(-1.4210854715202004e-13 -487.7600000000002) rotate(0.0 0 0)" /><circle cx="0" cy="0" r="2.6799999999999997" fill="#00007f" transform="translate(164.0000000000002 -487.7600000000002) rotate(0.0 0 0)" /></g><path d="M0,0 -8,-1.5 V1.5 L0,0" style="stroke:#00007f;fill:#00007f;stroke-width:1.3399999999999999;stroke-linecap:round;stroke-linejoin:bevel;" transform="translate(164.0000000000002 -460.9600000000002) rotate(90.0 0 0)" /></g><text x="-1.4210854715202004e-13" y="-490.4400000000002" style="white-space:pre;" fill="#005400" font-family="DejaVu Sans" font-size="16.08" text-anchor="middle" dominant-baseline="baseline" xml:space="preserve" transform="rotate(0.0 -1.4210854715202004e-13 -487.7600000000002)">TLRb 3⌀16,span=328</text></g></svg>
  TextPositionType = 0
  WayPoints = (2) [(0,0,0),(50,0,0)]
  WayPointsType = 0
  X = 148.5
  Y = 105
FEATURE [TechDraw::DrawViewSymbolPython] ReinforcementDimensioning046  # drawing view (typed FeaturePython)
  DimensionBottomOffset = 10
  DimensionFormat = %M %C⌀%D,span=%S
  DimensionLeftOffset = 16
  DimensionRightOffset = 16
  DimensionTopOffset = 22
  Font = DejaVu Sans
  FontSize = 3
  LineEndSymbol = 0
  LineMidPointSymbol = 1
  LineStartSymbol = 3
  LineStyle = 0
  LockPosition = false
  MultiRebar_LineEndSymbol = 0
  MultiRebar_LineStartSymbol = 0
  MultiRebar_OuterDimension = true
  MultiRebar_TextPositionType = 0
  ParentDrawingView = -> ReinforcementDrawingView003
  Rebar = -> Rebar005
  Rotation = 0
  Scale = 0.186567
  ScaleType = 2
  SingleRebar_LineEndSymbol = 0
  SingleRebar_LineStartSymbol = 3
  SingleRebar_OuterDimension = false
  SingleRebar_TextPositionType = 1
  StrokeWidth = 0.25
  Symbol = <svg version="1.1" xmlns="http://www.w3.org/2000/svg" xmlns:xlink="http://www.w3.org/1999/xlink" xmlns:freecad="http://www.freecadweb.org/wiki/index.php?title=Svg_Namespace" width="400.0mm" height="804.0mm" viewBox="0 0 400.0 804.0"><g transform="translate(200.0, 402.0000000000002)"><g><path d="M-285.76 367.0 L-162.00000000000009 367.0" style="stroke:#00007f;stroke-width:1.3399999999999999;stroke-linecap:round;fill:none;" stroke-dasharray="" /><g id="line_mid_points" /><path d="M0,0 -8,-1.5 V1.5 L0,0" style="stroke:#00007f;fill:#00007f;stroke-width:1.3399999999999999;stroke-linecap:round;stroke-linejoin:bevel;" transform="translate(-162.00000000000009 367.0) rotate(0.0 0 0)" /></g><text x="-285.76" y="375.04" style="white-space:pre;" fill="#005400" font-family="DejaVu Sans" font-size="16.08" text-anchor="end" dominant-baseline="baseline" xml:space="preserve">BLRb 1⌀20,span=0</text></g></svg>
  TextPositionType = 0
  WayPoints = (2) [(0,0,0),(50,0,0)]
  WayPointsType = 0
  X = 148.5
  Y = 105
FEATURE [TechDraw::DrawViewSymbolPython] ReinforcementDimensioning047  # drawing view (typed FeaturePython)
  DimensionBottomOffset = 10
  DimensionFormat = %M %C⌀%D,span=%S
  DimensionLeftOffset = 22
  DimensionRightOffset = 16
  DimensionTopOffset = 22
  Font = DejaVu Sans
  FontSize = 3
  LineEndSymbol = 0
  LineMidPointSymbol = 1
  LineStartSymbol = 3
  LineStyle = 0
  LockPosition = false
  MultiRebar_LineEndSymbol = 0
  MultiRebar_LineStartSymbol = 0
  MultiRebar_OuterDimension = true
  MultiRebar_TextPositionType = 0
  ParentDrawingView = -> ReinforcementDrawingView003
  Rebar = -> Rebar006
  Rotation = 0
  Scale = 0.186567
  ScaleType = 2
  SingleRebar_LineEndSymbol = 0
  SingleRebar_LineStartSymbol = 3
  SingleRebar_OuterDimension = false
  SingleRebar_TextPositionType = 1
  StrokeWidth = 0.25
  Symbol = <svg version="1.1" xmlns="http://www.w3.org/2000/svg" xmlns:xlink="http://www.w3.org/1999/xlink" xmlns:freecad="http://www.freecadweb.org/wiki/index.php?title=Svg_Namespace" width="400.0mm" height="804.0mm" viewBox="0 0 400.0 804.0"><g transform="translate(200.0, 402.0000000000002)"><g><path d="M-53.3333333333334 428.7999999999998 L-53.3333333333334 455.5999999999998 L53.33333333333334 455.5999999999998 L53.33333333333334 428.7999999999998" style="stroke:#00007f;stroke-width:1.3399999999999999;stroke-linecap:round;fill:none;" stroke-dasharray="" /><path d="M0,0 -8,-1.5 V1.5 L0,0" style="stroke:#00007f;fill:#00007f;stroke-width:1.3399999999999999;stroke-linecap:round;stroke-linejoin:bevel;" transform="translate(-53.3333333333334 428.7999999999998) rotate(-90.0 0 0)" /><g id="line_mid_points"><circle cx="0" cy="0" r="2.6799999999999997" fill="#00007f" transform="translate(-53.3333333333334 455.5999999999998) rotate(90.0 0 0)" /><circle cx="0" cy="0" r="2.6799999999999997" fill="#00007f" transform="translate(53.33333333333334 455.5999999999998) rotate(0.0 0 0)" /></g><path d="M0,0 -8,-1.5 V1.5 L0,0" style="stroke:#00007f;fill:#00007f;stroke-width:1.3399999999999999;stroke-linecap:round;stroke-linejoin:bevel;" transform="translate(53.33333333333334 428.7999999999998) rotate(-90.0 0 0)" /></g><text x="-2.842170943040401e-14" y="452.9199999999998" style="white-space:pre;" fill="#005400" font-family="DejaVu Sans" font-size="16.08" text-anchor="middle" dominant-baseline="baseline" xml:space="preserve" transform="rotate(0.0 -2.842170943040401e-14 455.5999999999998)">BLRb 2⌀16,span=107</text></g></svg>
  TextPositionType = 0
  WayPoints = (2) [(0,0,0),(50,0,0)]
  WayPointsType = 0
  X = 148.5
  Y = 105
FEATURE [TechDraw::DrawViewSymbolPython] ReinforcementDimensioning048  # drawing view (typed FeaturePython)
  DimensionBottomOffset = 16
  DimensionFormat = %M %C⌀%D,span=%S
  DimensionLeftOffset = 22
  DimensionRightOffset = 16
  DimensionTopOffset = 22
  Font = DejaVu Sans
  FontSize = 3
  LineEndSymbol = 0
  LineMidPointSymbol = 1
  LineStartSymbol = 3
  LineStyle = 0
  LockPosition = false
  MultiRebar_LineEndSymbol = 0
  MultiRebar_LineStartSymbol = 0
  MultiRebar_OuterDimension = true
  MultiRebar_TextPositionType = 0
  ParentDrawingView = -> ReinforcementDrawingView003
  Rebar = -> Rebar007
  Rotation = 0
  Scale = 0.186567
  ScaleType = 2
  SingleRebar_LineEndSymbol = 0
  SingleRebar_LineStartSymbol = 3
  SingleRebar_OuterDimension = false
  SingleRebar_TextPositionType = 1
  StrokeWidth = 0.25
  Symbol = <svg version="1.1" xmlns="http://www.w3.org/2000/svg" xmlns:xlink="http://www.w3.org/1999/xlink" xmlns:freecad="http://www.freecadweb.org/wiki/index.php?title=Svg_Namespace" width="400.0mm" height="804.0mm" viewBox="0 0 400.0 804.0"><g transform="translate(200.0, 402.0000000000002)"><g><path d="M285.76 383.0 L161.99999999999991 383.0" style="stroke:#00007f;stroke-width:1.3399999999999999;stroke-linecap:round;fill:none;" stroke-dasharray="" /><g id="line_mid_points" /><path d="M0,0 -8,-1.5 V1.5 L0,0" style="stroke:#00007f;fill:#00007f;stroke-width:1.3399999999999999;stroke-linecap:round;stroke-linejoin:bevel;" transform="translate(161.99999999999991 383.0) rotate(180.0 0 0)" /></g><text x="285.76" y="391.04" style="white-space:pre;" fill="#005400" font-family="DejaVu Sans" font-size="16.08" text-anchor="start" dominant-baseline="baseline" xml:space="preserve">BLRb 1⌀20,span=0</text></g></svg>
  TextPositionType = 0
  WayPoints = (2) [(0,0,0),(50,0,0)]
  WayPointsType = 0
  X = 148.5
  Y = 105
FEATURE [TechDraw::DrawViewSymbolPython] ReinforcementDimensioning049  # drawing view (typed FeaturePython)
  DimensionBottomOffset = 16
  DimensionFormat = %M %C⌀%D,span=%S
  DimensionLeftOffset = 22
  DimensionRightOffset = 22
  DimensionTopOffset = 22
  Font = DejaVu Sans
  FontSize = 3
  LineEndSymbol = 0
  LineMidPointSymbol = 1
  LineStartSymbol = 3
  LineStyle = 0
  LockPosition = false
  MultiRebar_LineEndSymbol = 0
  MultiRebar_LineStartSymbol = 0
  MultiRebar_OuterDimension = true
  MultiRebar_TextPositionType = 0
  ParentDrawingView = -> ReinforcementDrawingView003
  Rebar = -> Rebar008
  Rotation = 0
  Scale = 0.186567
  ScaleType = 2
  SingleRebar_LineEndSymbol = 0
  SingleRebar_LineStartSymbol = 3
  SingleRebar_OuterDimension = false
  SingleRebar_TextPositionType = 1
  StrokeWidth = 0.25
  Symbol = <svg version="1.1" xmlns="http://www.w3.org/2000/svg" xmlns:xlink="http://www.w3.org/1999/xlink" xmlns:freecad="http://www.freecadweb.org/wiki/index.php?title=Svg_Namespace" width="400.0mm" height="804.0mm" viewBox="0 0 400.0 804.0"><g transform="translate(200.0, 402.0000000000002)"><g><path d="M-164.00000000000006 460.9599999999998 L-164.00000000000006 487.7599999999998 L-0.0 487.7599999999998 L164.00000000000006 487.7599999999998 L164.00000000000006 460.9599999999998" style="stroke:#00007f;stroke-width:1.3399999999999999;stroke-linecap:round;fill:none;" stroke-dasharray="" /><path d="M0,0 -8,-1.5 V1.5 L0,0" style="stroke:#00007f;fill:#00007f;stroke-width:1.3399999999999999;stroke-linecap:round;stroke-linejoin:bevel;" transform="translate(-164.00000000000006 460.9599999999998) rotate(-90.0 0 0)" /><g id="line_mid_points"><circle cx="0" cy="0" r="2.6799999999999997" fill="#00007f" transform="translate(-164.00000000000006 487.7599999999998) rotate(90.0 0 0)" /><circle cx="0" cy="0" r="2.6799999999999997" fill="#00007f" transform="translate(-0.0 487.7599999999998) rotate(0.0 0 0)" /><circle cx="0" cy="0" r="2.6799999999999997" fill="#00007f" transform="translate(164.00000000000006 487.7599999999998) rotate(0.0 0 0)" /></g><path d="M0,0 -8,-1.5 V1.5 L0,0" style="stroke:#00007f;fill:#00007f;stroke-width:1.3399999999999999;stroke-linecap:round;stroke-linejoin:bevel;" transform="translate(164.00000000000006 460.9599999999998) rotate(-90.0 0 0)" /></g><text x="-0.0" y="485.0799999999998" style="white-space:pre;" fill="#005400" font-family="DejaVu Sans" font-size="16.08" text-anchor="middle" dominant-baseline="baseline" xml:space="preserve" transform="rotate(0.0 -0.0 487.7599999999998)">BLRb 3⌀16,span=328</text></g></svg>
  TextPositionType = 0
  WayPoints = (2) [(0,0,0),(50,0,0)]
  WayPointsType = 0
  X = 148.5
  Y = 105
FEATURE [TechDraw::DrawViewSymbolPython] ReinforcementDimensioning050  # drawing view (typed FeaturePython)
  DimensionBottomOffset = 22
  DimensionFormat = %M %C⌀%D,span=%S
  DimensionLeftOffset = 22
  DimensionRightOffset = 22
  DimensionTopOffset = 22
  Font = DejaVu Sans
  FontSize = 3
  LineEndSymbol = 0
  LineMidPointSymbol = 1
  LineStartSymbol = 3
  LineStyle = 0
  LockPosition = false
  MultiRebar_LineEndSymbol = 0
  MultiRebar_LineStartSymbol = 0
  MultiRebar_OuterDimension = true
  MultiRebar_TextPositionType = 0
  ParentDrawingView = -> ReinforcementDrawingView003
  Rebar = -> Rebar009
  Rotation = 0
  Scale = 0.186567
  ScaleType = 2
  SingleRebar_LineEndSymbol = 0
  SingleRebar_LineStartSymbol = 3
  SingleRebar_OuterDimension = false
  SingleRebar_TextPositionType = 1
  StrokeWidth = 0.25
  Symbol = <svg version="1.1" xmlns="http://www.w3.org/2000/svg" xmlns:xlink="http://www.w3.org/1999/xlink" xmlns:freecad="http://www.freecadweb.org/wiki/index.php?title=Svg_Namespace" width="400.0mm" height="804.0mm" viewBox="0 0 400.0 804.0"><g transform="translate(200.0, 402.0000000000002)"><g><path d="M-108.0 519.9199999999998 L-108.0 46.0" style="stroke:#00007f;stroke-width:1.3399999999999999;stroke-linecap:round;fill:none;" stroke-dasharray="" /><g id="line_mid_points" /><path d="M0,0 -8,-1.5 V1.5 L0,0" style="stroke:#00007f;fill:#00007f;stroke-width:1.3399999999999999;stroke-linecap:round;stroke-linejoin:bevel;" transform="translate(-108.0 46.0) rotate(-90.0 0 0)" /></g><text x="-108.0" y="527.9599999999998" style="white-space:pre;" fill="#005400" font-family="DejaVu Sans" font-size="16.08" text-anchor="middle" dominant-baseline="baseline" xml:space="preserve">LLRb 1⌀16,span=0</text></g></svg>
  TextPositionType = 0
  WayPoints = (2) [(0,0,0),(50,0,0)]
  WayPointsType = 0
  X = 148.5
  Y = 105
FEATURE [TechDraw::DrawViewSymbolPython] ReinforcementDimensioning051  # drawing view (typed FeaturePython)
  DimensionBottomOffset = 28
  DimensionFormat = %M %C⌀%D,span=%S
  DimensionLeftOffset = 22
  DimensionRightOffset = 22
  DimensionTopOffset = 22
  Font = DejaVu Sans
  FontSize = 3
  LineEndSymbol = 0
  LineMidPointSymbol = 1
  LineStartSymbol = 3
  LineStyle = 0
  LockPosition = false
  MultiRebar_LineEndSymbol = 0
  MultiRebar_LineStartSymbol = 0
  MultiRebar_OuterDimension = true
  MultiRebar_TextPositionType = 0
  ParentDrawingView = -> ReinforcementDrawingView003
  Rebar = -> Rebar010
  Rotation = 0
  Scale = 0.186567
  ScaleType = 2
  SingleRebar_LineEndSymbol = 0
  SingleRebar_LineStartSymbol = 3
  SingleRebar_OuterDimension = false
  SingleRebar_TextPositionType = 1
  StrokeWidth = 0.25
  Symbol = <svg version="1.1" xmlns="http://www.w3.org/2000/svg" xmlns:xlink="http://www.w3.org/1999/xlink" xmlns:freecad="http://www.freecadweb.org/wiki/index.php?title=Svg_Namespace" width="400.0mm" height="804.0mm" viewBox="0 0 400.0 804.0"><g transform="translate(200.0, 402.0000000000002)"><g><path d="M-143.0 -519.9200000000002 L-143.0 -4.547473508864641e-13" style="stroke:#00007f;stroke-width:1.3399999999999999;stroke-linecap:round;fill:none;" stroke-dasharray="" /><g id="line_mid_points" /><path d="M0,0 -8,-1.5 V1.5 L0,0" style="stroke:#00007f;fill:#00007f;stroke-width:1.3399999999999999;stroke-linecap:round;stroke-linejoin:bevel;" transform="translate(-143.0 -4.547473508864641e-13) rotate(90.0 0 0)" /></g><text x="-143.0" y="-519.9200000000002" style="white-space:pre;" fill="#005400" font-family="DejaVu Sans" font-size="16.08" text-anchor="middle" dominant-baseline="baseline" xml:space="preserve">LLRb 1⌀16,span=0</text></g></svg>
  TextPositionType = 0
  WayPoints = (2) [(0,0,0),(50,0,0)]
  WayPointsType = 0
  X = 148.5
  Y = 105
FEATURE [TechDraw::DrawViewSymbolPython] ReinforcementDimensioning052  # drawing view (typed FeaturePython)
  DimensionBottomOffset = 28
  DimensionFormat = %M %C⌀%D,span=%S
  DimensionLeftOffset = 22
  DimensionRightOffset = 22
  DimensionTopOffset = 28
  Font = DejaVu Sans
  FontSize = 3
  LineEndSymbol = 0
  LineMidPointSymbol = 1
  LineStartSymbol = 3
  LineStyle = 0
  LockPosition = false
  MultiRebar_LineEndSymbol = 0
  MultiRebar_LineStartSymbol = 0
  MultiRebar_OuterDimension = true
  MultiRebar_TextPositionType = 0
  ParentDrawingView = -> ReinforcementDrawingView003
  Rebar = -> Rebar011
  Rotation = 0
  Scale = 0.186567
  ScaleType = 2
  SingleRebar_LineEndSymbol = 0
  SingleRebar_LineStartSymbol = 3
  SingleRebar_OuterDimension = false
  SingleRebar_TextPositionType = 1
  StrokeWidth = 0.25
  Symbol = <svg version="1.1" xmlns="http://www.w3.org/2000/svg" xmlns:xlink="http://www.w3.org/1999/xlink" xmlns:freecad="http://www.freecadweb.org/wiki/index.php?title=Svg_Namespace" width="400.0mm" height="804.0mm" viewBox="0 0 400.0 804.0"><g transform="translate(200.0, 402.0000000000002)"><g><path d="M-76.0 -552.0800000000002 L-76.0 -46.0" style="stroke:#00007f;stroke-width:1.3399999999999999;stroke-linecap:round;fill:none;" stroke-dasharray="" /><g id="line_mid_points" /><path d="M0,0 -8,-1.5 V1.5 L0,0" style="stroke:#00007f;fill:#00007f;stroke-width:1.3399999999999999;stroke-linecap:round;stroke-linejoin:bevel;" transform="translate(-76.0 -46.0) rotate(90.0 0 0)" /></g><text x="-76.0" y="-552.0800000000002" style="white-space:pre;" fill="#005400" font-family="DejaVu Sans" font-size="16.08" text-anchor="middle" dominant-baseline="baseline" xml:space="preserve">LLRb 1⌀16,span=0</text></g></svg>
  TextPositionType = 0
  WayPoints = (2) [(0,0,0),(50,0,0)]
  WayPointsType = 0
  X = 148.5
  Y = 105
FEATURE [TechDraw::DrawViewSymbolPython] ReinforcementDimensioning053  # drawing view (typed FeaturePython)
  DimensionBottomOffset = 28
  DimensionFormat = %M %C⌀%D,span=%S
  DimensionLeftOffset = 22
  DimensionRightOffset = 22
  DimensionTopOffset = 34
  Font = DejaVu Sans
  FontSize = 3
  LineEndSymbol = 0
  LineMidPointSymbol = 1
  LineStartSymbol = 3
  LineStyle = 0
  LockPosition = false
  MultiRebar_LineEndSymbol = 0
  MultiRebar_LineStartSymbol = 0
  MultiRebar_OuterDimension = true
  MultiRebar_TextPositionType = 0
  ParentDrawingView = -> ReinforcementDrawingView003
  Rebar = -> Rebar012
  Rotation = 0
  Scale = 0.186567
  ScaleType = 2
  SingleRebar_LineEndSymbol = 0
  SingleRebar_LineStartSymbol = 3
  SingleRebar_OuterDimension = false
  SingleRebar_TextPositionType = 1
  StrokeWidth = 0.25
  Symbol = <svg version="1.1" xmlns="http://www.w3.org/2000/svg" xmlns:xlink="http://www.w3.org/1999/xlink" xmlns:freecad="http://www.freecadweb.org/wiki/index.php?title=Svg_Namespace" width="400.0mm" height="804.0mm" viewBox="0 0 400.0 804.0"><g transform="translate(200.0, 402.0000000000002)"><g><path d="M94.0 552.0799999999998 L94.0 45.999999999999545" style="stroke:#00007f;stroke-width:1.3399999999999999;stroke-linecap:round;fill:none;" stroke-dasharray="" /><g id="line_mid_points" /><path d="M0,0 -8,-1.5 V1.5 L0,0" style="stroke:#00007f;fill:#00007f;stroke-width:1.3399999999999999;stroke-linecap:round;stroke-linejoin:bevel;" transform="translate(94.0 45.999999999999545) rotate(-90.0 0 0)" /></g><text x="94.0" y="560.1199999999998" style="white-space:pre;" fill="#005400" font-family="DejaVu Sans" font-size="16.08" text-anchor="middle" dominant-baseline="baseline" xml:space="preserve">RLRb 1⌀16,span=0</text></g></svg>
  TextPositionType = 0
  WayPoints = (2) [(0,0,0),(50,0,0)]
  WayPointsType = 0
  X = 148.5
  Y = 105
FEATURE [TechDraw::DrawViewSymbolPython] ReinforcementDimensioning054  # drawing view (typed FeaturePython)
  DimensionBottomOffset = 34
  DimensionFormat = %M %C⌀%D,span=%S
  DimensionLeftOffset = 22
  DimensionRightOffset = 22
  DimensionTopOffset = 34
  Font = DejaVu Sans
  FontSize = 3
  LineEndSymbol = 0
  LineMidPointSymbol = 1
  LineStartSymbol = 3
  LineStyle = 0
  LockPosition = false
  MultiRebar_LineEndSymbol = 0
  MultiRebar_LineStartSymbol = 0
  MultiRebar_OuterDimension = true
  MultiRebar_TextPositionType = 0
  ParentDrawingView = -> ReinforcementDrawingView003
  Rebar = -> Rebar013
  Rotation = 0
  Scale = 0.186567
  ScaleType = 2
  SingleRebar_LineEndSymbol = 0
  SingleRebar_LineStartSymbol = 3
  SingleRebar_OuterDimension = false
  SingleRebar_TextPositionType = 1
  StrokeWidth = 0.25
  Symbol = <svg version="1.1" xmlns="http://www.w3.org/2000/svg" xmlns:xlink="http://www.w3.org/1999/xlink" xmlns:freecad="http://www.freecadweb.org/wiki/index.php?title=Svg_Namespace" width="400.0mm" height="804.0mm" viewBox="0 0 400.0 804.0"><g transform="translate(200.0, 402.0000000000002)"><g><path d="M111.0 584.2399999999998 L111.0 0.0" style="stroke:#00007f;stroke-width:1.3399999999999999;stroke-linecap:round;fill:none;" stroke-dasharray="" /><g id="line_mid_points" /><path d="M0,0 -8,-1.5 V1.5 L0,0" style="stroke:#00007f;fill:#00007f;stroke-width:1.3399999999999999;stroke-linecap:round;stroke-linejoin:bevel;" transform="translate(111.0 0.0) rotate(-90.0 0 0)" /></g><text x="111.0" y="592.2799999999997" style="white-space:pre;" fill="#005400" font-family="DejaVu Sans" font-size="16.08" text-anchor="middle" dominant-baseline="baseline" xml:space="preserve">RLRb 1⌀16,span=0</text></g></svg>
  TextPositionType = 0
  WayPoints = (2) [(0,0,0),(50,0,0)]
  WayPointsType = 0
  X = 148.5
  Y = 105
FEATURE [TechDraw::DrawViewSymbolPython] ReinforcementDimensioning055  # drawing view (typed FeaturePython)
  DimensionBottomOffset = 40
  DimensionFormat = %M %C⌀%D,span=%S
  DimensionLeftOffset = 22
  DimensionRightOffset = 22
  DimensionTopOffset = 34
  Font = DejaVu Sans
  FontSize = 3
  LineEndSymbol = 0
  LineMidPointSymbol = 1
  LineStartSymbol = 3
  LineStyle = 0
  LockPosition = false
  MultiRebar_LineEndSymbol = 0
  MultiRebar_LineStartSymbol = 0
  MultiRebar_OuterDimension = true
  MultiRebar_TextPositionType = 0
  ParentDrawingView = -> ReinforcementDrawingView003
  Rebar = -> Rebar014
  Rotation = 0
  Scale = 0.186567
  ScaleType = 2
  SingleRebar_LineEndSymbol = 0
  SingleRebar_LineStartSymbol = 3
  SingleRebar_OuterDimension = false
  SingleRebar_TextPositionType = 1
  StrokeWidth = 0.25
  Symbol = <svg version="1.1" xmlns="http://www.w3.org/2000/svg" xmlns:xlink="http://www.w3.org/1999/xlink" xmlns:freecad="http://www.freecadweb.org/wiki/index.php?title=Svg_Namespace" width="400.0mm" height="804.0mm" viewBox="0 0 400.0 804.0"><g transform="translate(200.0, 402.0000000000002)"><g><path d="M65.0 -584.2400000000002 L65.0 -46.000000000000455" style="stroke:#00007f;stroke-width:1.3399999999999999;stroke-linecap:round;fill:none;" stroke-dasharray="" /><g id="line_mid_points" /><path d="M0,0 -8,-1.5 V1.5 L0,0" style="stroke:#00007f;fill:#00007f;stroke-width:1.3399999999999999;stroke-linecap:round;stroke-linejoin:bevel;" transform="translate(65.0 -46.000000000000455) rotate(90.0 0 0)" /></g><text x="65.0" y="-584.2400000000002" style="white-space:pre;" fill="#005400" font-family="DejaVu Sans" font-size="16.08" text-anchor="middle" dominant-baseline="baseline" xml:space="preserve">RLRb 1⌀16,span=0</text></g></svg>
  TextPositionType = 0
  WayPoints = (2) [(0,0,0),(50,0,0)]
  WayPointsType = 0
  X = 148.5
  Y = 105
FEATURE [TechDraw::DrawPage] TechDraw__DrawPage003  label="Beam Drawing003"
  KeepUpdated = true
  NextBalloonIndex = 1
  ProjectionType = 0
  Template = -> Template003
  Views = -> [ReinforcementDrawingView003,ReinforcementDimensioning041,ReinforcementDimensioning042,ReinforcementDimensioning043,ReinforcementDimensioning044,ReinforcementDimensioning045,ReinforcementDimensioning046,ReinforcementDimensioning047,ReinforcementDimensioning048,ReinforcementDimensioning049,ReinforcementDimensioning050,ReinforcementDimensioning051,ReinforcementDimensioning052,+3 more]
FEATURE [TechDraw::DrawSVGTemplate] Template004
  Height = 210
  Orientation = 1
  Width = 297
FEATURE [TechDraw::DrawViewSymbolPython] ReinforcementDrawingView004  label="Top View"  # drawing view (typed FeaturePython)
  DimensionBottomOffset = 40
  DimensionLeftOffset = 10
  DimensionRightOffset = 34
  DimensionTopOffset = 34
  Height = 400
  LeftOffset = 20
  LockPosition = false
  MaxHeight = 210
  MaxWidth = 297
  MinBottomOffset = 20
  MinRightOffset = 20
  PositionType = 0
  Rebars = -> [Rebar,Rebar001,Rebar002,Rebar003,Rebar004,Rebar005,Rebar006,Rebar007,Rebar008,Rebar009,Rebar010,Rebar011,Rebar012,Rebar013,Rebar014]
  RebarsColorStyle = 0
  RebarsStrokeWidth = 0.35
  Rotation = 0
  Scale = 0.116818
  ScaleType = 1
  Structure = -> Structure
  StructureColorStyle = 0
  StructureStrokeWidth = 0.5
  Symbol = <blob: 9845 chars omitted>
  Template = -> Template004
  TopOffset = 81.6364
  View = 4
  VisibleRebars = -> [Rebar,Rebar001,Rebar002,Rebar003,Rebar004,Rebar005,Rebar006,Rebar007,Rebar008,Rebar009,Rebar010,Rebar012,Rebar013]
  Width = 2200
  X = 148.5
  Y = 105
  expr: TopOffset = .Template.Height.Value / 2 - .Height.Value * .Scale / 2
  expr: LeftOffset = .Template.Width.Value / 2 - .Width.Value * .Scale / 2
FEATURE [TechDraw::DrawViewSymbolPython] ReinforcementDimensioning056  # drawing view (typed FeaturePython)
  DimensionBottomOffset = 10
  DimensionFormat = %M %C⌀%D,span=%S
  DimensionLeftOffset = 10
  DimensionRightOffset = 10
  DimensionTopOffset = 10
  Font = DejaVu Sans
  FontSize = 3
  LineEndSymbol = 0
  LineMidPointSymbol = 1
  LineStartSymbol = 3
  LineStyle = 0
  LockPosition = false
  MultiRebar_LineEndSymbol = 0
  MultiRebar_LineStartSymbol = 0
  MultiRebar_OuterDimension = true
  MultiRebar_TextPositionType = 0
  ParentDrawingView = -> ReinforcementDrawingView004
  Rebar = -> Rebar
  Rotation = 0
  Scale = 0.116818
  ScaleType = 2
  SingleRebar_LineEndSymbol = 0
  SingleRebar_LineStartSymbol = 3
  SingleRebar_OuterDimension = false
  SingleRebar_TextPositionType = 1
  StrokeWidth = 0.25
  Symbol = <blob: 5819 chars omitted>
  TextPositionType = 0
  WayPoints = (2) [(0,0,0),(50,0,0)]
  WayPointsType = 0
  X = 148.5
  Y = 105
FEATURE [TechDraw::DrawViewSymbolPython] ReinforcementDimensioning057  # drawing view (typed FeaturePython)
  DimensionBottomOffset = 16
  DimensionFormat = %M %C⌀%D,span=%S
  DimensionLeftOffset = 10
  DimensionRightOffset = 10
  DimensionTopOffset = 10
  Font = DejaVu Sans
  FontSize = 3
  LineEndSymbol = 0
  LineMidPointSymbol = 1
  LineStartSymbol = 3
  LineStyle = 0
  LockPosition = false
  MultiRebar_LineEndSymbol = 0
  MultiRebar_LineStartSymbol = 0
  MultiRebar_OuterDimension = true
  MultiRebar_TextPositionType = 0
  ParentDrawingView = -> ReinforcementDrawingView004
  Rebar = -> Rebar001
  Rotation = 0
  Scale = 0.116818
  ScaleType = 2
  SingleRebar_LineEndSymbol = 0
  SingleRebar_LineStartSymbol = 3
  SingleRebar_OuterDimension = false
  SingleRebar_TextPositionType = 1
  StrokeWidth = 0.25
  Symbol = <svg version="1.1" xmlns="http://www.w3.org/2000/svg" xmlns:xlink="http://www.w3.org/1999/xlink" xmlns:freecad="http://www.freecadweb.org/wiki/index.php?title=Svg_Namespace" width="2200.0mm" height="400.0mm" viewBox="0 0 2200.0 400.0"><g transform="translate(100.00000000000023, 200.0)"><g><path d="M1653.0 336.96498054474705 L1653.0 161.99999999999994" style="stroke:#00007f;stroke-width:2.140077821011673;stroke-linecap:round;fill:none;" stroke-dasharray="" /><g id="line_mid_points" /><path d="M0,0 -8,-1.5 V1.5 L0,0" style="stroke:#00007f;fill:#00007f;stroke-width:2.140077821011673;stroke-linecap:round;stroke-linejoin:bevel;" transform="translate(1653.0 161.99999999999994) rotate(-90.0 0 0)" /></g><text x="1653.0" y="349.8054474708171" style="white-space:pre;" fill="#005400" font-family="DejaVu Sans" font-size="25.68093385214008" text-anchor="middle" dominant-baseline="baseline" xml:space="preserve">TLRb 1⌀20,span=0</text></g></svg>
  TextPositionType = 0
  WayPoints = (2) [(0,0,0),(50,0,0)]
  WayPointsType = 0
  X = 148.5
  Y = 105
FEATURE [TechDraw::DrawViewSymbolPython] ReinforcementDimensioning058  # drawing view (typed FeaturePython)
  DimensionBottomOffset = 22
  DimensionFormat = %M %C⌀%D,span=%S
  DimensionLeftOffset = 10
  DimensionRightOffset = 10
  DimensionTopOffset = 10
  Font = DejaVu Sans
  FontSize = 3
  LineEndSymbol = 0
  LineMidPointSymbol = 1
  LineStartSymbol = 3
  LineStyle = 0
  LockPosition = false
  MultiRebar_LineEndSymbol = 0
  MultiRebar_LineStartSymbol = 0
  MultiRebar_OuterDimension = true
  MultiRebar_TextPositionType = 0
  ParentDrawingView = -> ReinforcementDrawingView004
  Rebar = -> Rebar002
  Rotation = 0
  Scale = 0.116818
  ScaleType = 2
  SingleRebar_LineEndSymbol = 0
  SingleRebar_LineStartSymbol = 3
  SingleRebar_OuterDimension = false
  SingleRebar_TextPositionType = 1
  StrokeWidth = 0.25
  Symbol = <svg version="1.1" xmlns="http://www.w3.org/2000/svg" xmlns:xlink="http://www.w3.org/1999/xlink" xmlns:freecad="http://www.freecadweb.org/wiki/index.php?title=Svg_Namespace" width="2200.0mm" height="400.0mm" viewBox="0 0 2200.0 400.0"><g transform="translate(100.00000000000023, 200.0)"><g><path d="M2142.8015564202337 53.33333333333326 L2185.603112840467 53.33333333333326 L2185.603112840467 -53.333333333333485 L2142.8015564202337 -53.333333333333485" style="stroke:#00007f;stroke-width:2.140077821011673;stroke-linecap:round;fill:none;" stroke-dasharray="" /><path d="M0,0 -8,-1.5 V1.5 L0,0" style="stroke:#00007f;fill:#00007f;stroke-width:2.140077821011673;stroke-linecap:round;stroke-linejoin:bevel;" transform="translate(2142.8015564202337 53.33333333333326) rotate(180.0 0 0)" /><g id="line_mid_points"><circle cx="0" cy="0" r="4.280155642023346" fill="#00007f" transform="translate(2185.603112840467 53.33333333333326) rotate(0.0 0 0)" /><circle cx="0" cy="0" r="4.280155642023346" fill="#00007f" transform="translate(2185.603112840467 -53.333333333333485) rotate(-90.0 0 0)" /></g><path d="M0,0 -8,-1.5 V1.5 L0,0" style="stroke:#00007f;fill:#00007f;stroke-width:2.140077821011673;stroke-linecap:round;stroke-linejoin:bevel;" transform="translate(2142.8015564202337 -53.333333333333485) rotate(180.0 0 0)" /></g><text x="2185.603112840467" y="-4.28015564202346" style="white-space:pre;" fill="#005400" font-family="DejaVu Sans" font-size="25.68093385214008" text-anchor="middle" dominant-baseline="baseline" xml:space="preserve" transform="rotate(-90 2185.603112840467 -1.1368683772161603e-13)">TLRb 2⌀16,span=107</text></g></svg>
  TextPositionType = 0
  WayPoints = (2) [(0,0,0),(50,0,0)]
  WayPointsType = 0
  X = 148.5
  Y = 105
FEATURE [TechDraw::DrawViewSymbolPython] ReinforcementDimensioning059  # drawing view (typed FeaturePython)
  DimensionBottomOffset = 22
  DimensionFormat = %M %C⌀%D,span=%S
  DimensionLeftOffset = 10
  DimensionRightOffset = 16
  DimensionTopOffset = 10
  Font = DejaVu Sans
  FontSize = 3
  LineEndSymbol = 0
  LineMidPointSymbol = 1
  LineStartSymbol = 3
  LineStyle = 0
  LockPosition = false
  MultiRebar_LineEndSymbol = 0
  MultiRebar_LineStartSymbol = 0
  MultiRebar_OuterDimension = true
  MultiRebar_TextPositionType = 0
  ParentDrawingView = -> ReinforcementDrawingView004
  Rebar = -> Rebar003
  Rotation = 0
  Scale = 0.116818
  ScaleType = 2
  SingleRebar_LineEndSymbol = 0
  SingleRebar_LineStartSymbol = 3
  SingleRebar_OuterDimension = false
  SingleRebar_TextPositionType = 1
  StrokeWidth = 0.25
  Symbol = <svg version="1.1" xmlns="http://www.w3.org/2000/svg" xmlns:xlink="http://www.w3.org/1999/xlink" xmlns:freecad="http://www.freecadweb.org/wiki/index.php?title=Svg_Namespace" width="2200.0mm" height="400.0mm" viewBox="0 0 2200.0 400.0"><g transform="translate(100.00000000000023, 200.0)"><g><path d="M1861.0 -285.6031128404669 L1861.0 -162.00000000000006" style="stroke:#00007f;stroke-width:2.140077821011673;stroke-linecap:round;fill:none;" stroke-dasharray="" /><g id="line_mid_points" /><path d="M0,0 -8,-1.5 V1.5 L0,0" style="stroke:#00007f;fill:#00007f;stroke-width:2.140077821011673;stroke-linecap:round;stroke-linejoin:bevel;" transform="translate(1861.0 -162.00000000000006) rotate(90.0 0 0)" /></g><text x="1861.0" y="-285.6031128404669" style="white-space:pre;" fill="#005400" font-family="DejaVu Sans" font-size="25.68093385214008" text-anchor="middle" dominant-baseline="baseline" xml:space="preserve">TLRb 1⌀20,span=0</text></g></svg>
  TextPositionType = 0
  WayPoints = (2) [(0,0,0),(50,0,0)]
  WayPointsType = 0
  X = 148.5
  Y = 105
FEATURE [TechDraw::DrawViewSymbolPython] ReinforcementDimensioning060  # drawing view (typed FeaturePython)
  DimensionBottomOffset = 22
  DimensionFormat = %M %C⌀%D,span=%S
  DimensionLeftOffset = 10
  DimensionRightOffset = 16
  DimensionTopOffset = 16
  Font = DejaVu Sans
  FontSize = 3
  LineEndSymbol = 0
  LineMidPointSymbol = 1
  LineStartSymbol = 3
  LineStyle = 0
  LockPosition = false
  MultiRebar_LineEndSymbol = 0
  MultiRebar_LineStartSymbol = 0
  MultiRebar_OuterDimension = true
  MultiRebar_TextPositionType = 0
  ParentDrawingView = -> ReinforcementDrawingView004
  Rebar = -> Rebar004
  Rotation = 0
  Scale = 0.116818
  ScaleType = 2
  SingleRebar_LineEndSymbol = 0
  SingleRebar_LineStartSymbol = 3
  SingleRebar_OuterDimension = false
  SingleRebar_TextPositionType = 1
  StrokeWidth = 0.25
  Symbol = <svg version="1.1" xmlns="http://www.w3.org/2000/svg" xmlns:xlink="http://www.w3.org/1999/xlink" xmlns:freecad="http://www.freecadweb.org/wiki/index.php?title=Svg_Namespace" width="2200.0mm" height="400.0mm" viewBox="0 0 2200.0 400.0"><g transform="translate(100.00000000000023, 200.0)"><g><path d="M2194.1634241245138 163.99999999999994 L2236.964980544747 163.99999999999994 L2236.964980544747 -1.4210854715202004e-13 L2236.964980544747 -164.00000000000017 L2194.1634241245138 -164.00000000000017" style="stroke:#00007f;stroke-width:2.140077821011673;stroke-linecap:round;fill:none;" stroke-dasharray="" /><path d="M0,0 -8,-1.5 V1.5 L0,0" style="stroke:#00007f;fill:#00007f;stroke-width:2.140077821011673;stroke-linecap:round;stroke-linejoin:bevel;" transform="translate(2194.1634241245138 163.99999999999994) rotate(180.0 0 0)" /><g id="line_mid_points"><circle cx="0" cy="0" r="4.280155642023346" fill="#00007f" transform="translate(2236.964980544747 163.99999999999994) rotate(0.0 0 0)" /><circle cx="0" cy="0" r="4.280155642023346" fill="#00007f" transform="translate(2236.964980544747 -1.4210854715202004e-13) rotate(-90.0 0 0)" /><circle cx="0" cy="0" r="4.280155642023346" fill="#00007f" transform="translate(2236.964980544747 -164.00000000000017) rotate(-90.0 0 0)" /></g><path d="M0,0 -8,-1.5 V1.5 L0,0" style="stroke:#00007f;fill:#00007f;stroke-width:2.140077821011673;stroke-linecap:round;stroke-linejoin:bevel;" transform="translate(2194.1634241245138 -164.00000000000017) rotate(180.0 0 0)" /></g><text x="2236.964980544747" y="-4.280155642023488" style="white-space:pre;" fill="#005400" font-family="DejaVu Sans" font-size="25.68093385214008" text-anchor="middle" dominant-baseline="baseline" xml:space="preserve" transform="rotate(-90 2236.964980544747 -1.4210854715202004e-13)">TLRb 3⌀16,span=328</text></g></svg>
  TextPositionType = 0
  WayPoints = (2) [(0,0,0),(50,0,0)]
  WayPointsType = 0
  X = 148.5
  Y = 105
FEATURE [TechDraw::DrawViewSymbolPython] ReinforcementDimensioning061  # drawing view (typed FeaturePython)
  DimensionBottomOffset = 22
  DimensionFormat = %M %C⌀%D,span=%S
  DimensionLeftOffset = 10
  DimensionRightOffset = 22
  DimensionTopOffset = 16
  Font = DejaVu Sans
  FontSize = 3
  LineEndSymbol = 0
  LineMidPointSymbol = 1
  LineStartSymbol = 3
  LineStyle = 0
  LockPosition = false
  MultiRebar_LineEndSymbol = 0
  MultiRebar_LineStartSymbol = 0
  MultiRebar_OuterDimension = true
  MultiRebar_TextPositionType = 0
  ParentDrawingView = -> ReinforcementDrawingView004
  Rebar = -> Rebar005
  Rotation = 0
  Scale = 0.116818
  ScaleType = 2
  SingleRebar_LineEndSymbol = 0
  SingleRebar_LineStartSymbol = 3
  SingleRebar_OuterDimension = false
  SingleRebar_TextPositionType = 1
  StrokeWidth = 0.25
  Symbol = <svg version="1.1" xmlns="http://www.w3.org/2000/svg" xmlns:xlink="http://www.w3.org/1999/xlink" xmlns:freecad="http://www.freecadweb.org/wiki/index.php?title=Svg_Namespace" width="2200.0mm" height="400.0mm" viewBox="0 0 2200.0 400.0"><g transform="translate(100.00000000000023, 200.0)"><g><path d="M2010.0 388.3268482490272 L2010.0 162.00000000000006" style="stroke:#00007f;stroke-width:2.140077821011673;stroke-linecap:round;fill:none;" stroke-dasharray="" /><g id="line_mid_points" /><path d="M0,0 -8,-1.5 V1.5 L0,0" style="stroke:#00007f;fill:#00007f;stroke-width:2.140077821011673;stroke-linecap:round;stroke-linejoin:bevel;" transform="translate(2010.0 162.00000000000006) rotate(-90.0 0 0)" /></g><text x="2010.0" y="401.16731517509726" style="white-space:pre;" fill="#005400" font-family="DejaVu Sans" font-size="25.68093385214008" text-anchor="middle" dominant-baseline="baseline" xml:space="preserve">BLRb 1⌀20,span=0</text></g></svg>
  TextPositionType = 0
  WayPoints = (2) [(0,0,0),(50,0,0)]
  WayPointsType = 0
  X = 148.5
  Y = 105
FEATURE [TechDraw::DrawViewSymbolPython] ReinforcementDimensioning062  # drawing view (typed FeaturePython)
  DimensionBottomOffset = 28
  DimensionFormat = %M %C⌀%D,span=%S
  DimensionLeftOffset = 10
  DimensionRightOffset = 22
  DimensionTopOffset = 16
  Font = DejaVu Sans
  FontSize = 3
  LineEndSymbol = 0
  LineMidPointSymbol = 1
  LineStartSymbol = 3
  LineStyle = 0
  LockPosition = false
  MultiRebar_LineEndSymbol = 0
  MultiRebar_LineStartSymbol = 0
  MultiRebar_OuterDimension = true
  MultiRebar_TextPositionType = 0
  ParentDrawingView = -> ReinforcementDrawingView004
  Rebar = -> Rebar006
  Rotation = 0
  Scale = 0.116818
  ScaleType = 2
  SingleRebar_LineEndSymbol = 0
  SingleRebar_LineStartSymbol = 3
  SingleRebar_OuterDimension = false
  SingleRebar_TextPositionType = 1
  StrokeWidth = 0.25
  Symbol = <svg version="1.1" xmlns="http://www.w3.org/2000/svg" xmlns:xlink="http://www.w3.org/1999/xlink" xmlns:freecad="http://www.freecadweb.org/wiki/index.php?title=Svg_Namespace" width="2200.0mm" height="400.0mm" viewBox="0 0 2200.0 400.0"><g transform="translate(100.00000000000023, 200.0)"><g><path d="M2245.525291828794 53.33333333333337 L2288.326848249027 53.33333333333337 L2288.326848249027 -53.33333333333337 L2245.525291828794 -53.33333333333337" style="stroke:#00007f;stroke-width:2.140077821011673;stroke-linecap:round;fill:none;" stroke-dasharray="" /><path d="M0,0 -8,-1.5 V1.5 L0,0" style="stroke:#00007f;fill:#00007f;stroke-width:2.140077821011673;stroke-linecap:round;stroke-linejoin:bevel;" transform="translate(2245.525291828794 53.33333333333337) rotate(180.0 0 0)" /><g id="line_mid_points"><circle cx="0" cy="0" r="4.280155642023346" fill="#00007f" transform="translate(2288.326848249027 53.33333333333337) rotate(0.0 0 0)" /><circle cx="0" cy="0" r="4.280155642023346" fill="#00007f" transform="translate(2288.326848249027 -53.33333333333337) rotate(-90.0 0 0)" /></g><path d="M0,0 -8,-1.5 V1.5 L0,0" style="stroke:#00007f;fill:#00007f;stroke-width:2.140077821011673;stroke-linecap:round;stroke-linejoin:bevel;" transform="translate(2245.525291828794 -53.33333333333337) rotate(180.0 0 0)" /></g><text x="2288.326848249027" y="-4.280155642023346" style="white-space:pre;" fill="#005400" font-family="DejaVu Sans" font-size="25.68093385214008" text-anchor="middle" dominant-baseline="baseline" xml:space="preserve" transform="rotate(-90 2288.326848249027 0.0)">BLRb 2⌀16,span=107</text></g></svg>
  TextPositionType = 0
  WayPoints = (2) [(0,0,0),(50,0,0)]
  WayPointsType = 0
  X = 148.5
  Y = 105
FEATURE [TechDraw::DrawViewSymbolPython] ReinforcementDimensioning063  # drawing view (typed FeaturePython)
  DimensionBottomOffset = 28
  DimensionFormat = %M %C⌀%D,span=%S
  DimensionLeftOffset = 10
  DimensionRightOffset = 28
  DimensionTopOffset = 16
  Font = DejaVu Sans
  FontSize = 3
  LineEndSymbol = 0
  LineMidPointSymbol = 1
  LineStartSymbol = 3
  LineStyle = 0
  LockPosition = false
  MultiRebar_LineEndSymbol = 0
  MultiRebar_LineStartSymbol = 0
  MultiRebar_OuterDimension = true
  MultiRebar_TextPositionType = 0
  ParentDrawingView = -> ReinforcementDrawingView004
  Rebar = -> Rebar007
  Rotation = 0
  Scale = 0.116818
  ScaleType = 2
  SingleRebar_LineEndSymbol = 0
  SingleRebar_LineStartSymbol = 3
  SingleRebar_OuterDimension = false
  SingleRebar_TextPositionType = 1
  StrokeWidth = 0.25
  Symbol = <svg version="1.1" xmlns="http://www.w3.org/2000/svg" xmlns:xlink="http://www.w3.org/1999/xlink" xmlns:freecad="http://www.freecadweb.org/wiki/index.php?title=Svg_Namespace" width="2200.0mm" height="400.0mm" viewBox="0 0 2200.0 400.0"><g transform="translate(100.00000000000023, 200.0)"><g><path d="M1330.0 -336.96498054474705 L1330.0 -161.99999999999994" style="stroke:#00007f;stroke-width:2.140077821011673;stroke-linecap:round;fill:none;" stroke-dasharray="" /><g id="line_mid_points" /><path d="M0,0 -8,-1.5 V1.5 L0,0" style="stroke:#00007f;fill:#00007f;stroke-width:2.140077821011673;stroke-linecap:round;stroke-linejoin:bevel;" transform="translate(1330.0 -161.99999999999994) rotate(90.0 0 0)" /></g><text x="1330.0" y="-336.96498054474705" style="white-space:pre;" fill="#005400" font-family="DejaVu Sans" font-size="25.68093385214008" text-anchor="middle" dominant-baseline="baseline" xml:space="preserve">BLRb 1⌀20,span=0</text></g></svg>
  TextPositionType = 0
  WayPoints = (2) [(0,0,0),(50,0,0)]
  WayPointsType = 0
  X = 148.5
  Y = 105
FEATURE [TechDraw::DrawViewSymbolPython] ReinforcementDimensioning064  # drawing view (typed FeaturePython)
  DimensionBottomOffset = 28
  DimensionFormat = %M %C⌀%D,span=%S
  DimensionLeftOffset = 10
  DimensionRightOffset = 28
  DimensionTopOffset = 22
  Font = DejaVu Sans
  FontSize = 3
  LineEndSymbol = 0
  LineMidPointSymbol = 1
  LineStartSymbol = 3
  LineStyle = 0
  LockPosition = false
  MultiRebar_LineEndSymbol = 0
  MultiRebar_LineStartSymbol = 0
  MultiRebar_OuterDimension = true
  MultiRebar_TextPositionType = 0
  ParentDrawingView = -> ReinforcementDrawingView004
  Rebar = -> Rebar008
  Rotation = 0
  Scale = 0.116818
  ScaleType = 2
  SingleRebar_LineEndSymbol = 0
  SingleRebar_LineStartSymbol = 3
  SingleRebar_OuterDimension = false
  SingleRebar_TextPositionType = 1
  StrokeWidth = 0.25
  Symbol = <svg version="1.1" xmlns="http://www.w3.org/2000/svg" xmlns:xlink="http://www.w3.org/1999/xlink" xmlns:freecad="http://www.freecadweb.org/wiki/index.php?title=Svg_Namespace" width="2200.0mm" height="400.0mm" viewBox="0 0 2200.0 400.0"><g transform="translate(100.00000000000023, 200.0)"><g><path d="M2296.8871595330743 164.00000000000006 L2339.6887159533076 164.00000000000006 L2339.6887159533076 -0.0 L2339.6887159533076 -164.00000000000006 L2296.8871595330743 -164.00000000000006" style="stroke:#00007f;stroke-width:2.140077821011673;stroke-linecap:round;fill:none;" stroke-dasharray="" /><path d="M0,0 -8,-1.5 V1.5 L0,0" style="stroke:#00007f;fill:#00007f;stroke-width:2.140077821011673;stroke-linecap:round;stroke-linejoin:bevel;" transform="translate(2296.8871595330743 164.00000000000006) rotate(180.0 0 0)" /><g id="line_mid_points"><circle cx="0" cy="0" r="4.280155642023346" fill="#00007f" transform="translate(2339.6887159533076 164.00000000000006) rotate(0.0 0 0)" /><circle cx="0" cy="0" r="4.280155642023346" fill="#00007f" transform="translate(2339.6887159533076 -0.0) rotate(-90.0 0 0)" /><circle cx="0" cy="0" r="4.280155642023346" fill="#00007f" transform="translate(2339.6887159533076 -164.00000000000006) rotate(-90.0 0 0)" /></g><path d="M0,0 -8,-1.5 V1.5 L0,0" style="stroke:#00007f;fill:#00007f;stroke-width:2.140077821011673;stroke-linecap:round;stroke-linejoin:bevel;" transform="translate(2296.8871595330743 -164.00000000000006) rotate(180.0 0 0)" /></g><text x="2339.6887159533076" y="-4.280155642023346" style="white-space:pre;" fill="#005400" font-family="DejaVu Sans" font-size="25.68093385214008" text-anchor="middle" dominant-baseline="baseline" xml:space="preserve" transform="rotate(-90 2339.6887159533076 -0.0)">BLRb 3⌀16,span=328</text></g></svg>
  TextPositionType = 0
  WayPoints = (2) [(0,0,0),(50,0,0)]
  WayPointsType = 0
  X = 148.5
  Y = 105
FEATURE [TechDraw::DrawViewSymbolPython] ReinforcementDimensioning065  # drawing view (typed FeaturePython)
  DimensionBottomOffset = 28
  DimensionFormat = %M %C⌀%D,span=%S
  DimensionLeftOffset = 10
  DimensionRightOffset = 34
  DimensionTopOffset = 22
  Font = DejaVu Sans
  FontSize = 3
  LineEndSymbol = 0
  LineMidPointSymbol = 1
  LineStartSymbol = 3
  LineStyle = 0
  LockPosition = false
  MultiRebar_LineEndSymbol = 0
  MultiRebar_LineStartSymbol = 0
  MultiRebar_OuterDimension = true
  MultiRebar_TextPositionType = 0
  ParentDrawingView = -> ReinforcementDrawingView004
  Rebar = -> Rebar009
  Rotation = 0
  Scale = 0.116818
  ScaleType = 2
  SingleRebar_LineEndSymbol = 0
  SingleRebar_LineStartSymbol = 3
  SingleRebar_OuterDimension = false
  SingleRebar_TextPositionType = 1
  StrokeWidth = 0.25
  Symbol = <svg version="1.1" xmlns="http://www.w3.org/2000/svg" xmlns:xlink="http://www.w3.org/1999/xlink" xmlns:freecad="http://www.freecadweb.org/wiki/index.php?title=Svg_Namespace" width="2200.0mm" height="400.0mm" viewBox="0 0 2200.0 400.0"><g transform="translate(100.00000000000023, 200.0)"><g><path d="M640.0 439.6887159533074 L640.0 164.0" style="stroke:#00007f;stroke-width:2.140077821011673;stroke-linecap:round;fill:none;" stroke-dasharray="" /><g id="line_mid_points" /><path d="M0,0 -8,-1.5 V1.5 L0,0" style="stroke:#00007f;fill:#00007f;stroke-width:2.140077821011673;stroke-linecap:round;stroke-linejoin:bevel;" transform="translate(640.0 164.0) rotate(-90.0 0 0)" /></g><text x="640.0" y="452.52918287937746" style="white-space:pre;" fill="#005400" font-family="DejaVu Sans" font-size="25.68093385214008" text-anchor="middle" dominant-baseline="baseline" xml:space="preserve">LLRb 1⌀16,span=0</text></g></svg>
  TextPositionType = 0
  WayPoints = (2) [(0,0,0),(50,0,0)]
  WayPointsType = 0
  X = 148.5
  Y = 105
FEATURE [TechDraw::DrawViewSymbolPython] ReinforcementDimensioning066  # drawing view (typed FeaturePython)
  DimensionBottomOffset = 34
  DimensionFormat = %M %C⌀%D,span=%S
  DimensionLeftOffset = 10
  DimensionRightOffset = 34
  DimensionTopOffset = 22
  Font = DejaVu Sans
  FontSize = 3
  LineEndSymbol = 0
  LineMidPointSymbol = 1
  LineStartSymbol = 3
  LineStyle = 0
  LockPosition = false
  MultiRebar_LineEndSymbol = 0
  MultiRebar_LineStartSymbol = 0
  MultiRebar_OuterDimension = true
  MultiRebar_TextPositionType = 0
  ParentDrawingView = -> ReinforcementDrawingView004
  Rebar = -> Rebar010
  Rotation = 0
  Scale = 0.116818
  ScaleType = 2
  SingleRebar_LineEndSymbol = 0
  SingleRebar_LineStartSymbol = 3
  SingleRebar_OuterDimension = false
  SingleRebar_TextPositionType = 1
  StrokeWidth = 0.25
  Symbol = <svg version="1.1" xmlns="http://www.w3.org/2000/svg" xmlns:xlink="http://www.w3.org/1999/xlink" xmlns:freecad="http://www.freecadweb.org/wiki/index.php?title=Svg_Namespace" width="2200.0mm" height="400.0mm" viewBox="0 0 2200.0 400.0"><g transform="translate(100.00000000000023, 200.0)"><g><path d="M227.0 491.05058365758754 L227.0 164.0" style="stroke:#00007f;stroke-width:2.140077821011673;stroke-linecap:round;fill:none;" stroke-dasharray="" /><g id="line_mid_points" /><path d="M0,0 -8,-1.5 V1.5 L0,0" style="stroke:#00007f;fill:#00007f;stroke-width:2.140077821011673;stroke-linecap:round;stroke-linejoin:bevel;" transform="translate(227.0 164.0) rotate(-90.0 0 0)" /></g><text x="227.0" y="503.8910505836576" style="white-space:pre;" fill="#005400" font-family="DejaVu Sans" font-size="25.68093385214008" text-anchor="middle" dominant-baseline="baseline" xml:space="preserve">LLRb 1⌀16,span=0</text></g></svg>
  TextPositionType = 0
  WayPoints = (2) [(0,0,0),(50,0,0)]
  WayPointsType = 0
  X = 148.5
  Y = 105
FEATURE [TechDraw::DrawViewSymbolPython] ReinforcementDimensioning067  # drawing view (typed FeaturePython)
  DimensionBottomOffset = 40
  DimensionFormat = %M %C⌀%D,span=%S
  DimensionLeftOffset = 10
  DimensionRightOffset = 34
  DimensionTopOffset = 22
  Font = DejaVu Sans
  FontSize = 3
  LineEndSymbol = 0
  LineMidPointSymbol = 1
  LineStartSymbol = 3
  LineStyle = 0
  LockPosition = false
  MultiRebar_LineEndSymbol = 0
  MultiRebar_LineStartSymbol = 0
  MultiRebar_OuterDimension = true
  MultiRebar_TextPositionType = 0
  ParentDrawingView = -> ReinforcementDrawingView004
  Rebar = -> Rebar012
  Rotation = 0
  Scale = 0.116818
  ScaleType = 2
  SingleRebar_LineEndSymbol = 0
  SingleRebar_LineStartSymbol = 3
  SingleRebar_OuterDimension = false
  SingleRebar_TextPositionType = 1
  StrokeWidth = 0.25
  Symbol = <svg version="1.1" xmlns="http://www.w3.org/2000/svg" xmlns:xlink="http://www.w3.org/1999/xlink" xmlns:freecad="http://www.freecadweb.org/wiki/index.php?title=Svg_Namespace" width="2200.0mm" height="400.0mm" viewBox="0 0 2200.0 400.0"><g transform="translate(100.00000000000023, 200.0)"><g><path d="M685.0 -388.3268482490272 L685.0 -164.0" style="stroke:#00007f;stroke-width:2.140077821011673;stroke-linecap:round;fill:none;" stroke-dasharray="" /><g id="line_mid_points" /><path d="M0,0 -8,-1.5 V1.5 L0,0" style="stroke:#00007f;fill:#00007f;stroke-width:2.140077821011673;stroke-linecap:round;stroke-linejoin:bevel;" transform="translate(685.0 -164.0) rotate(90.0 0 0)" /></g><text x="685.0" y="-388.3268482490272" style="white-space:pre;" fill="#005400" font-family="DejaVu Sans" font-size="25.68093385214008" text-anchor="middle" dominant-baseline="baseline" xml:space="preserve">RLRb 1⌀16,span=0</text></g></svg>
  TextPositionType = 0
  WayPoints = (2) [(0,0,0),(50,0,0)]
  WayPointsType = 0
  X = 148.5
  Y = 105
FEATURE [TechDraw::DrawViewSymbolPython] ReinforcementDimensioning068  # drawing view (typed FeaturePython)
  DimensionBottomOffset = 40
  DimensionFormat = %M %C⌀%D,span=%S
  DimensionLeftOffset = 10
  DimensionRightOffset = 34
  DimensionTopOffset = 28
  Font = DejaVu Sans
  FontSize = 3
  LineEndSymbol = 0
  LineMidPointSymbol = 1
  LineStartSymbol = 3
  LineStyle = 0
  LockPosition = false
  MultiRebar_LineEndSymbol = 0
  MultiRebar_LineStartSymbol = 0
  MultiRebar_OuterDimension = true
  MultiRebar_TextPositionType = 0
  ParentDrawingView = -> ReinforcementDrawingView004
  Rebar = -> Rebar013
  Rotation = 0
  Scale = 0.116818
  ScaleType = 2
  SingleRebar_LineEndSymbol = 0
  SingleRebar_LineStartSymbol = 3
  SingleRebar_OuterDimension = false
  SingleRebar_TextPositionType = 1
  StrokeWidth = 0.25
  Symbol = <svg version="1.1" xmlns="http://www.w3.org/2000/svg" xmlns:xlink="http://www.w3.org/1999/xlink" xmlns:freecad="http://www.freecadweb.org/wiki/index.php?title=Svg_Namespace" width="2200.0mm" height="400.0mm" viewBox="0 0 2200.0 400.0"><g transform="translate(100.00000000000023, 200.0)"><g><path d="M100.0 -439.6887159533074 L100.0 -164.0" style="stroke:#00007f;stroke-width:2.140077821011673;stroke-linecap:round;fill:none;" stroke-dasharray="" /><g id="line_mid_points" /><path d="M0,0 -8,-1.5 V1.5 L0,0" style="stroke:#00007f;fill:#00007f;stroke-width:2.140077821011673;stroke-linecap:round;stroke-linejoin:bevel;" transform="translate(100.0 -164.0) rotate(90.0 0 0)" /></g><text x="100.0" y="-439.6887159533074" style="white-space:pre;" fill="#005400" font-family="DejaVu Sans" font-size="25.68093385214008" text-anchor="middle" dominant-baseline="baseline" xml:space="preserve">RLRb 1⌀16,span=0</text></g></svg>
  TextPositionType = 0
  WayPoints = (2) [(0,0,0),(50,0,0)]
  WayPointsType = 0
  X = 148.5
  Y = 105
FEATURE [TechDraw::DrawPage] TechDraw__DrawPage004  label="Beam Drawing004"
  KeepUpdated = true
  NextBalloonIndex = 1
  ProjectionType = 0
  Template = -> Template004
  Views = -> [ReinforcementDrawingView004,ReinforcementDimensioning056,ReinforcementDimensioning057,ReinforcementDimensioning058,ReinforcementDimensioning059,ReinforcementDimensioning060,ReinforcementDimensioning061,ReinforcementDimensioning062,ReinforcementDimensioning063,ReinforcementDimensioning064,ReinforcementDimensioning065,ReinforcementDimensioning066,ReinforcementDimensioning067,+1 more]
FEATURE [TechDraw::DrawSVGTemplate] Template005
  Height = 210
  Orientation = 1
  Width = 297
FEATURE [TechDraw::DrawViewSymbolPython] ReinforcementDrawingView005  label="Bottom View"  # drawing view (typed FeaturePython)
  DimensionBottomOffset = 40
  DimensionLeftOffset = 10
  DimensionRightOffset = 34
  DimensionTopOffset = 34
  Height = 400
  LeftOffset = 20
  LockPosition = false
  MaxHeight = 210
  MaxWidth = 297
  MinBottomOffset = 20
  MinRightOffset = 20
  PositionType = 0
  Rebars = -> [Rebar,Rebar001,Rebar002,Rebar003,Rebar004,Rebar005,Rebar006,Rebar007,Rebar008,Rebar009,Rebar010,Rebar011,Rebar012,Rebar013,Rebar014]
  RebarsColorStyle = 0
  RebarsStrokeWidth = 0.35
  Rotation = 0
  Scale = 0.116818
  ScaleType = 1
  Structure = -> Structure
  StructureColorStyle = 0
  StructureStrokeWidth = 0.5
  Symbol = <blob: 9845 chars omitted>
  Template = -> Template005
  TopOffset = 81.6364
  View = 5
  VisibleRebars = -> [Rebar,Rebar001,Rebar002,Rebar003,Rebar004,Rebar005,Rebar006,Rebar007,Rebar008,Rebar009,Rebar010,Rebar012,Rebar013]
  Width = 2200
  X = 148.5
  Y = 105
  expr: TopOffset = .Template.Height.Value / 2 - .Height.Value * .Scale / 2
  expr: LeftOffset = .Template.Width.Value / 2 - .Width.Value * .Scale / 2
FEATURE [TechDraw::DrawViewSymbolPython] ReinforcementDimensioning069  # drawing view (typed FeaturePython)
  DimensionBottomOffset = 10
  DimensionFormat = %M %C⌀%D,span=%S
  DimensionLeftOffset = 10
  DimensionRightOffset = 10
  DimensionTopOffset = 10
  Font = DejaVu Sans
  FontSize = 3
  LineEndSymbol = 0
  LineMidPointSymbol = 1
  LineStartSymbol = 3
  LineStyle = 0
  LockPosition = false
  MultiRebar_LineEndSymbol = 0
  MultiRebar_LineStartSymbol = 0
  MultiRebar_OuterDimension = true
  MultiRebar_TextPositionType = 0
  ParentDrawingView = -> ReinforcementDrawingView005
  Rebar = -> Rebar
  Rotation = 0
  Scale = 0.116818
  ScaleType = 2
  SingleRebar_LineEndSymbol = 0
  SingleRebar_LineStartSymbol = 3
  SingleRebar_OuterDimension = false
  SingleRebar_TextPositionType = 1
  StrokeWidth = 0.25
  Symbol = <blob: 5819 chars omitted>
  TextPositionType = 0
  WayPoints = (2) [(0,0,0),(50,0,0)]
  WayPointsType = 0
  X = 148.5
  Y = 105
FEATURE [TechDraw::DrawViewSymbolPython] ReinforcementDimensioning070  # drawing view (typed FeaturePython)
  DimensionBottomOffset = 16
  DimensionFormat = %M %C⌀%D,span=%S
  DimensionLeftOffset = 10
  DimensionRightOffset = 10
  DimensionTopOffset = 10
  Font = DejaVu Sans
  FontSize = 3
  LineEndSymbol = 0
  LineMidPointSymbol = 1
  LineStartSymbol = 3
  LineStyle = 0
  LockPosition = false
  MultiRebar_LineEndSymbol = 0
  MultiRebar_LineStartSymbol = 0
  MultiRebar_OuterDimension = true
  MultiRebar_TextPositionType = 0
  ParentDrawingView = -> ReinforcementDrawingView005
  Rebar = -> Rebar001
  Rotation = 0
  Scale = 0.116818
  ScaleType = 2
  SingleRebar_LineEndSymbol = 0
  SingleRebar_LineStartSymbol = 3
  SingleRebar_OuterDimension = false
  SingleRebar_TextPositionType = 1
  StrokeWidth = 0.25
  Symbol = <svg version="1.1" xmlns="http://www.w3.org/2000/svg" xmlns:xlink="http://www.w3.org/1999/xlink" xmlns:freecad="http://www.freecadweb.org/wiki/index.php?title=Svg_Namespace" width="2200.0mm" height="400.0mm" viewBox="0 0 2200.0 400.0"><g transform="translate(100.00000000000023, 200.0)"><g><path d="M1846.0 -285.6031128404669 L1846.0 -161.99999999999994" style="stroke:#00007f;stroke-width:2.140077821011673;stroke-linecap:round;fill:none;" stroke-dasharray="" /><g id="line_mid_points" /><path d="M0,0 -8,-1.5 V1.5 L0,0" style="stroke:#00007f;fill:#00007f;stroke-width:2.140077821011673;stroke-linecap:round;stroke-linejoin:bevel;" transform="translate(1846.0 -161.99999999999994) rotate(90.0 0 0)" /></g><text x="1846.0" y="-285.6031128404669" style="white-space:pre;" fill="#005400" font-family="DejaVu Sans" font-size="25.68093385214008" text-anchor="middle" dominant-baseline="baseline" xml:space="preserve">TLRb 1⌀20,span=0</text></g></svg>
  TextPositionType = 0
  WayPoints = (2) [(0,0,0),(50,0,0)]
  WayPointsType = 0
  X = 148.5
  Y = 105
FEATURE [TechDraw::DrawViewSymbolPython] ReinforcementDimensioning071  # drawing view (typed FeaturePython)
  DimensionBottomOffset = 16
  DimensionFormat = %M %C⌀%D,span=%S
  DimensionLeftOffset = 10
  DimensionRightOffset = 10
  DimensionTopOffset = 16
  Font = DejaVu Sans
  FontSize = 3
  LineEndSymbol = 0
  LineMidPointSymbol = 1
  LineStartSymbol = 3
  LineStyle = 0
  LockPosition = false
  MultiRebar_LineEndSymbol = 0
  MultiRebar_LineStartSymbol = 0
  MultiRebar_OuterDimension = true
  MultiRebar_TextPositionType = 0
  ParentDrawingView = -> ReinforcementDrawingView005
  Rebar = -> Rebar002
  Rotation = 0
  Scale = 0.116818
  ScaleType = 2
  SingleRebar_LineEndSymbol = 0
  SingleRebar_LineStartSymbol = 3
  SingleRebar_OuterDimension = false
  SingleRebar_TextPositionType = 1
  StrokeWidth = 0.25
  Symbol = <svg version="1.1" xmlns="http://www.w3.org/2000/svg" xmlns:xlink="http://www.w3.org/1999/xlink" xmlns:freecad="http://www.freecadweb.org/wiki/index.php?title=Svg_Namespace" width="2200.0mm" height="400.0mm" viewBox="0 0 2200.0 400.0"><g transform="translate(100.00000000000023, 200.0)"><g><path d="M2142.8015564202337 -53.33333333333326 L2185.603112840467 -53.33333333333326 L2185.603112840467 53.333333333333485 L2142.8015564202337 53.333333333333485" style="stroke:#00007f;stroke-width:2.140077821011673;stroke-linecap:round;fill:none;" stroke-dasharray="" /><path d="M0,0 -8,-1.5 V1.5 L0,0" style="stroke:#00007f;fill:#00007f;stroke-width:2.140077821011673;stroke-linecap:round;stroke-linejoin:bevel;" transform="translate(2142.8015564202337 -53.33333333333326) rotate(180.0 0 0)" /><g id="line_mid_points"><circle cx="0" cy="0" r="4.280155642023346" fill="#00007f" transform="translate(2185.603112840467 -53.33333333333326) rotate(0.0 0 0)" /><circle cx="0" cy="0" r="4.280155642023346" fill="#00007f" transform="translate(2185.603112840467 53.333333333333485) rotate(90.0 0 0)" /></g><path d="M0,0 -8,-1.5 V1.5 L0,0" style="stroke:#00007f;fill:#00007f;stroke-width:2.140077821011673;stroke-linecap:round;stroke-linejoin:bevel;" transform="translate(2142.8015564202337 53.333333333333485) rotate(180.0 0 0)" /></g><text x="2185.603112840467" y="-4.2801556420232325" style="white-space:pre;" fill="#005400" font-family="DejaVu Sans" font-size="25.68093385214008" text-anchor="middle" dominant-baseline="baseline" xml:space="preserve" transform="rotate(-90 2185.603112840467 1.1368683772161603e-13)">TLRb 2⌀16,span=107</text></g></svg>
  TextPositionType = 0
  WayPoints = (2) [(0,0,0),(50,0,0)]
  WayPointsType = 0
  X = 148.5
  Y = 105
FEATURE [TechDraw::DrawViewSymbolPython] ReinforcementDimensioning072  # drawing view (typed FeaturePython)
  DimensionBottomOffset = 16
  DimensionFormat = %M %C⌀%D,span=%S
  DimensionLeftOffset = 10
  DimensionRightOffset = 16
  DimensionTopOffset = 16
  Font = DejaVu Sans
  FontSize = 3
  LineEndSymbol = 0
  LineMidPointSymbol = 1
  LineStartSymbol = 3
  LineStyle = 0
  LockPosition = false
  MultiRebar_LineEndSymbol = 0
  MultiRebar_LineStartSymbol = 0
  MultiRebar_OuterDimension = true
  MultiRebar_TextPositionType = 0
  ParentDrawingView = -> ReinforcementDrawingView005
  Rebar = -> Rebar003
  Rotation = 0
  Scale = 0.116818
  ScaleType = 2
  SingleRebar_LineEndSymbol = 0
  SingleRebar_LineStartSymbol = 3
  SingleRebar_OuterDimension = false
  SingleRebar_TextPositionType = 1
  StrokeWidth = 0.25
  Symbol = <svg version="1.1" xmlns="http://www.w3.org/2000/svg" xmlns:xlink="http://www.w3.org/1999/xlink" xmlns:freecad="http://www.freecadweb.org/wiki/index.php?title=Svg_Namespace" width="2200.0mm" height="400.0mm" viewBox="0 0 2200.0 400.0"><g transform="translate(100.00000000000023, 200.0)"><g><path d="M417.0 336.96498054474705 L417.0 162.00000000000006" style="stroke:#00007f;stroke-width:2.140077821011673;stroke-linecap:round;fill:none;" stroke-dasharray="" /><g id="line_mid_points" /><path d="M0,0 -8,-1.5 V1.5 L0,0" style="stroke:#00007f;fill:#00007f;stroke-width:2.140077821011673;stroke-linecap:round;stroke-linejoin:bevel;" transform="translate(417.0 162.00000000000006) rotate(-90.0 0 0)" /></g><text x="417.0" y="349.8054474708171" style="white-space:pre;" fill="#005400" font-family="DejaVu Sans" font-size="25.68093385214008" text-anchor="middle" dominant-baseline="baseline" xml:space="preserve">TLRb 1⌀20,span=0</text></g></svg>
  TextPositionType = 0
  WayPoints = (2) [(0,0,0),(50,0,0)]
  WayPointsType = 0
  X = 148.5
  Y = 105
FEATURE [TechDraw::DrawViewSymbolPython] ReinforcementDimensioning073  # drawing view (typed FeaturePython)
  DimensionBottomOffset = 22
  DimensionFormat = %M %C⌀%D,span=%S
  DimensionLeftOffset = 10
  DimensionRightOffset = 16
  DimensionTopOffset = 16
  Font = DejaVu Sans
  FontSize = 3
  LineEndSymbol = 0
  LineMidPointSymbol = 1
  LineStartSymbol = 3
  LineStyle = 0
  LockPosition = false
  MultiRebar_LineEndSymbol = 0
  MultiRebar_LineStartSymbol = 0
  MultiRebar_OuterDimension = true
  MultiRebar_TextPositionType = 0
  ParentDrawingView = -> ReinforcementDrawingView005
  Rebar = -> Rebar004
  Rotation = 0
  Scale = 0.116818
  ScaleType = 2
  SingleRebar_LineEndSymbol = 0
  SingleRebar_LineStartSymbol = 3
  SingleRebar_OuterDimension = false
  SingleRebar_TextPositionType = 1
  StrokeWidth = 0.25
  Symbol = <svg version="1.1" xmlns="http://www.w3.org/2000/svg" xmlns:xlink="http://www.w3.org/1999/xlink" xmlns:freecad="http://www.freecadweb.org/wiki/index.php?title=Svg_Namespace" width="2200.0mm" height="400.0mm" viewBox="0 0 2200.0 400.0"><g transform="translate(100.00000000000023, 200.0)"><g><path d="M2194.1634241245138 -163.99999999999994 L2236.964980544747 -163.99999999999994 L2236.964980544747 -1.4210854715202004e-13 L2236.964980544747 164.00000000000017 L2194.1634241245138 164.00000000000017" style="stroke:#00007f;stroke-width:2.140077821011673;stroke-linecap:round;fill:none;" stroke-dasharray="" /><path d="M0,0 -8,-1.5 V1.5 L0,0" style="stroke:#00007f;fill:#00007f;stroke-width:2.140077821011673;stroke-linecap:round;stroke-linejoin:bevel;" transform="translate(2194.1634241245138 -163.99999999999994) rotate(180.0 0 0)" /><g id="line_mid_points"><circle cx="0" cy="0" r="4.280155642023346" fill="#00007f" transform="translate(2236.964980544747 -163.99999999999994) rotate(0.0 0 0)" /><circle cx="0" cy="0" r="4.280155642023346" fill="#00007f" transform="translate(2236.964980544747 -1.4210854715202004e-13) rotate(90.0 0 0)" /><circle cx="0" cy="0" r="4.280155642023346" fill="#00007f" transform="translate(2236.964980544747 164.00000000000017) rotate(90.0 0 0)" /></g><path d="M0,0 -8,-1.5 V1.5 L0,0" style="stroke:#00007f;fill:#00007f;stroke-width:2.140077821011673;stroke-linecap:round;stroke-linejoin:bevel;" transform="translate(2194.1634241245138 164.00000000000017) rotate(180.0 0 0)" /></g><text x="2236.964980544747" y="-4.280155642023488" style="white-space:pre;" fill="#005400" font-family="DejaVu Sans" font-size="25.68093385214008" text-anchor="middle" dominant-baseline="baseline" xml:space="preserve" transform="rotate(-90 2236.964980544747 -1.4210854715202004e-13)">TLRb 3⌀16,span=328</text></g></svg>
  TextPositionType = 0
  WayPoints = (2) [(0,0,0),(50,0,0)]
  WayPointsType = 0
  X = 148.5
  Y = 105
FEATURE [TechDraw::DrawViewSymbolPython] ReinforcementDimensioning074  # drawing view (typed FeaturePython)
  DimensionBottomOffset = 22
  DimensionFormat = %M %C⌀%D,span=%S
  DimensionLeftOffset = 10
  DimensionRightOffset = 22
  DimensionTopOffset = 16
  Font = DejaVu Sans
  FontSize = 3
  LineEndSymbol = 0
  LineMidPointSymbol = 1
  LineStartSymbol = 3
  LineStyle = 0
  LockPosition = false
  MultiRebar_LineEndSymbol = 0
  MultiRebar_LineStartSymbol = 0
  MultiRebar_OuterDimension = true
  MultiRebar_TextPositionType = 0
  ParentDrawingView = -> ReinforcementDrawingView005
  Rebar = -> Rebar005
  Rotation = 0
  Scale = 0.116818
  ScaleType = 2
  SingleRebar_LineEndSymbol = 0
  SingleRebar_LineStartSymbol = 3
  SingleRebar_OuterDimension = false
  SingleRebar_TextPositionType = 1
  StrokeWidth = 0.25
  Symbol = <svg version="1.1" xmlns="http://www.w3.org/2000/svg" xmlns:xlink="http://www.w3.org/1999/xlink" xmlns:freecad="http://www.freecadweb.org/wiki/index.php?title=Svg_Namespace" width="2200.0mm" height="400.0mm" viewBox="0 0 2200.0 400.0"><g transform="translate(100.00000000000023, 200.0)"><g><path d="M235.0 -336.96498054474705 L235.0 -162.00000000000006" style="stroke:#00007f;stroke-width:2.140077821011673;stroke-linecap:round;fill:none;" stroke-dasharray="" /><g id="line_mid_points" /><path d="M0,0 -8,-1.5 V1.5 L0,0" style="stroke:#00007f;fill:#00007f;stroke-width:2.140077821011673;stroke-linecap:round;stroke-linejoin:bevel;" transform="translate(235.0 -162.00000000000006) rotate(90.0 0 0)" /></g><text x="235.0" y="-336.96498054474705" style="white-space:pre;" fill="#005400" font-family="DejaVu Sans" font-size="25.68093385214008" text-anchor="middle" dominant-baseline="baseline" xml:space="preserve">BLRb 1⌀20,span=0</text></g></svg>
  TextPositionType = 0
  WayPoints = (2) [(0,0,0),(50,0,0)]
  WayPointsType = 0
  X = 148.5
  Y = 105
FEATURE [TechDraw::DrawViewSymbolPython] ReinforcementDimensioning075  # drawing view (typed FeaturePython)
  DimensionBottomOffset = 22
  DimensionFormat = %M %C⌀%D,span=%S
  DimensionLeftOffset = 10
  DimensionRightOffset = 22
  DimensionTopOffset = 22
  Font = DejaVu Sans
  FontSize = 3
  LineEndSymbol = 0
  LineMidPointSymbol = 1
  LineStartSymbol = 3
  LineStyle = 0
  LockPosition = false
  MultiRebar_LineEndSymbol = 0
  MultiRebar_LineStartSymbol = 0
  MultiRebar_OuterDimension = true
  MultiRebar_TextPositionType = 0
  ParentDrawingView = -> ReinforcementDrawingView005
  Rebar = -> Rebar006
  Rotation = 0
  Scale = 0.116818
  ScaleType = 2
  SingleRebar_LineEndSymbol = 0
  SingleRebar_LineStartSymbol = 3
  SingleRebar_OuterDimension = false
  SingleRebar_TextPositionType = 1
  StrokeWidth = 0.25
  Symbol = <svg version="1.1" xmlns="http://www.w3.org/2000/svg" xmlns:xlink="http://www.w3.org/1999/xlink" xmlns:freecad="http://www.freecadweb.org/wiki/index.php?title=Svg_Namespace" width="2200.0mm" height="400.0mm" viewBox="0 0 2200.0 400.0"><g transform="translate(100.00000000000023, 200.0)"><g><path d="M2245.525291828794 -53.33333333333337 L2288.326848249027 -53.33333333333337 L2288.326848249027 53.33333333333337 L2245.525291828794 53.33333333333337" style="stroke:#00007f;stroke-width:2.140077821011673;stroke-linecap:round;fill:none;" stroke-dasharray="" /><path d="M0,0 -8,-1.5 V1.5 L0,0" style="stroke:#00007f;fill:#00007f;stroke-width:2.140077821011673;stroke-linecap:round;stroke-linejoin:bevel;" transform="translate(2245.525291828794 -53.33333333333337) rotate(180.0 0 0)" /><g id="line_mid_points"><circle cx="0" cy="0" r="4.280155642023346" fill="#00007f" transform="translate(2288.326848249027 -53.33333333333337) rotate(0.0 0 0)" /><circle cx="0" cy="0" r="4.280155642023346" fill="#00007f" transform="translate(2288.326848249027 53.33333333333337) rotate(90.0 0 0)" /></g><path d="M0,0 -8,-1.5 V1.5 L0,0" style="stroke:#00007f;fill:#00007f;stroke-width:2.140077821011673;stroke-linecap:round;stroke-linejoin:bevel;" transform="translate(2245.525291828794 53.33333333333337) rotate(180.0 0 0)" /></g><text x="2288.326848249027" y="-4.280155642023346" style="white-space:pre;" fill="#005400" font-family="DejaVu Sans" font-size="25.68093385214008" text-anchor="middle" dominant-baseline="baseline" xml:space="preserve" transform="rotate(-90 2288.326848249027 0.0)">BLRb 2⌀16,span=107</text></g></svg>
  TextPositionType = 0
  WayPoints = (2) [(0,0,0),(50,0,0)]
  WayPointsType = 0
  X = 148.5
  Y = 105
FEATURE [TechDraw::DrawViewSymbolPython] ReinforcementDimensioning076  # drawing view (typed FeaturePython)
  DimensionBottomOffset = 22
  DimensionFormat = %M %C⌀%D,span=%S
  DimensionLeftOffset = 10
  DimensionRightOffset = 28
  DimensionTopOffset = 22
  Font = DejaVu Sans
  FontSize = 3
  LineEndSymbol = 0
  LineMidPointSymbol = 1
  LineStartSymbol = 3
  LineStyle = 0
  LockPosition = false
  MultiRebar_LineEndSymbol = 0
  MultiRebar_LineStartSymbol = 0
  MultiRebar_OuterDimension = true
  MultiRebar_TextPositionType = 0
  ParentDrawingView = -> ReinforcementDrawingView005
  Rebar = -> Rebar007
  Rotation = 0
  Scale = 0.116818
  ScaleType = 2
  SingleRebar_LineEndSymbol = 0
  SingleRebar_LineStartSymbol = 3
  SingleRebar_OuterDimension = false
  SingleRebar_TextPositionType = 1
  StrokeWidth = 0.25
  Symbol = <svg version="1.1" xmlns="http://www.w3.org/2000/svg" xmlns:xlink="http://www.w3.org/1999/xlink" xmlns:freecad="http://www.freecadweb.org/wiki/index.php?title=Svg_Namespace" width="2200.0mm" height="400.0mm" viewBox="0 0 2200.0 400.0"><g transform="translate(100.00000000000023, 200.0)"><g><path d="M512.0 388.3268482490272 L512.0 161.99999999999994" style="stroke:#00007f;stroke-width:2.140077821011673;stroke-linecap:round;fill:none;" stroke-dasharray="" /><g id="line_mid_points" /><path d="M0,0 -8,-1.5 V1.5 L0,0" style="stroke:#00007f;fill:#00007f;stroke-width:2.140077821011673;stroke-linecap:round;stroke-linejoin:bevel;" transform="translate(512.0 161.99999999999994) rotate(-90.0 0 0)" /></g><text x="512.0" y="401.16731517509726" style="white-space:pre;" fill="#005400" font-family="DejaVu Sans" font-size="25.68093385214008" text-anchor="middle" dominant-baseline="baseline" xml:space="preserve">BLRb 1⌀20,span=0</text></g></svg>
  TextPositionType = 0
  WayPoints = (2) [(0,0,0),(50,0,0)]
  WayPointsType = 0
  X = 148.5
  Y = 105
FEATURE [TechDraw::DrawViewSymbolPython] ReinforcementDimensioning077  # drawing view (typed FeaturePython)
  DimensionBottomOffset = 28
  DimensionFormat = %M %C⌀%D,span=%S
  DimensionLeftOffset = 10
  DimensionRightOffset = 28
  DimensionTopOffset = 22
  Font = DejaVu Sans
  FontSize = 3
  LineEndSymbol = 0
  LineMidPointSymbol = 1
  LineStartSymbol = 3
  LineStyle = 0
  LockPosition = false
  MultiRebar_LineEndSymbol = 0
  MultiRebar_LineStartSymbol = 0
  MultiRebar_OuterDimension = true
  MultiRebar_TextPositionType = 0
  ParentDrawingView = -> ReinforcementDrawingView005
  Rebar = -> Rebar008
  Rotation = 0
  Scale = 0.116818
  ScaleType = 2
  SingleRebar_LineEndSymbol = 0
  SingleRebar_LineStartSymbol = 3
  SingleRebar_OuterDimension = false
  SingleRebar_TextPositionType = 1
  StrokeWidth = 0.25
  Symbol = <svg version="1.1" xmlns="http://www.w3.org/2000/svg" xmlns:xlink="http://www.w3.org/1999/xlink" xmlns:freecad="http://www.freecadweb.org/wiki/index.php?title=Svg_Namespace" width="2200.0mm" height="400.0mm" viewBox="0 0 2200.0 400.0"><g transform="translate(100.00000000000023, 200.0)"><g><path d="M2296.8871595330743 -164.00000000000006 L2339.6887159533076 -164.00000000000006 L2339.6887159533076 -0.0 L2339.6887159533076 164.00000000000006 L2296.8871595330743 164.00000000000006" style="stroke:#00007f;stroke-width:2.140077821011673;stroke-linecap:round;fill:none;" stroke-dasharray="" /><path d="M0,0 -8,-1.5 V1.5 L0,0" style="stroke:#00007f;fill:#00007f;stroke-width:2.140077821011673;stroke-linecap:round;stroke-linejoin:bevel;" transform="translate(2296.8871595330743 -164.00000000000006) rotate(180.0 0 0)" /><g id="line_mid_points"><circle cx="0" cy="0" r="4.280155642023346" fill="#00007f" transform="translate(2339.6887159533076 -164.00000000000006) rotate(0.0 0 0)" /><circle cx="0" cy="0" r="4.280155642023346" fill="#00007f" transform="translate(2339.6887159533076 -0.0) rotate(90.0 0 0)" /><circle cx="0" cy="0" r="4.280155642023346" fill="#00007f" transform="translate(2339.6887159533076 164.00000000000006) rotate(90.0 0 0)" /></g><path d="M0,0 -8,-1.5 V1.5 L0,0" style="stroke:#00007f;fill:#00007f;stroke-width:2.140077821011673;stroke-linecap:round;stroke-linejoin:bevel;" transform="translate(2296.8871595330743 164.00000000000006) rotate(180.0 0 0)" /></g><text x="2339.6887159533076" y="-4.280155642023346" style="white-space:pre;" fill="#005400" font-family="DejaVu Sans" font-size="25.68093385214008" text-anchor="middle" dominant-baseline="baseline" xml:space="preserve" transform="rotate(-90 2339.6887159533076 -0.0)">BLRb 3⌀16,span=328</text></g></svg>
  TextPositionType = 0
  WayPoints = (2) [(0,0,0),(50,0,0)]
  WayPointsType = 0
  X = 148.5
  Y = 105
FEATURE [TechDraw::DrawViewSymbolPython] ReinforcementDimensioning078  # drawing view (typed FeaturePython)
  DimensionBottomOffset = 28
  DimensionFormat = %M %C⌀%D,span=%S
  DimensionLeftOffset = 10
  DimensionRightOffset = 34
  DimensionTopOffset = 22
  Font = DejaVu Sans
  FontSize = 3
  LineEndSymbol = 0
  LineMidPointSymbol = 1
  LineStartSymbol = 3
  LineStyle = 0
  LockPosition = false
  MultiRebar_LineEndSymbol = 0
  MultiRebar_LineStartSymbol = 0
  MultiRebar_OuterDimension = true
  MultiRebar_TextPositionType = 0
  ParentDrawingView = -> ReinforcementDrawingView005
  Rebar = -> Rebar009
  Rotation = 0
  Scale = 0.116818
  ScaleType = 2
  SingleRebar_LineEndSymbol = 0
  SingleRebar_LineStartSymbol = 3
  SingleRebar_OuterDimension = false
  SingleRebar_TextPositionType = 1
  StrokeWidth = 0.25
  Symbol = <svg version="1.1" xmlns="http://www.w3.org/2000/svg" xmlns:xlink="http://www.w3.org/1999/xlink" xmlns:freecad="http://www.freecadweb.org/wiki/index.php?title=Svg_Namespace" width="2200.0mm" height="400.0mm" viewBox="0 0 2200.0 400.0"><g transform="translate(100.00000000000023, 200.0)"><g><path d="M901.0 -388.3268482490272 L901.0 -164.0" style="stroke:#00007f;stroke-width:2.140077821011673;stroke-linecap:round;fill:none;" stroke-dasharray="" /><g id="line_mid_points" /><path d="M0,0 -8,-1.5 V1.5 L0,0" style="stroke:#00007f;fill:#00007f;stroke-width:2.140077821011673;stroke-linecap:round;stroke-linejoin:bevel;" transform="translate(901.0 -164.0) rotate(90.0 0 0)" /></g><text x="901.0" y="-388.3268482490272" style="white-space:pre;" fill="#005400" font-family="DejaVu Sans" font-size="25.68093385214008" text-anchor="middle" dominant-baseline="baseline" xml:space="preserve">LLRb 1⌀16,span=0</text></g></svg>
  TextPositionType = 0
  WayPoints = (2) [(0,0,0),(50,0,0)]
  WayPointsType = 0
  X = 148.5
  Y = 105
FEATURE [TechDraw::DrawViewSymbolPython] ReinforcementDimensioning079  # drawing view (typed FeaturePython)
  DimensionBottomOffset = 28
  DimensionFormat = %M %C⌀%D,span=%S
  DimensionLeftOffset = 10
  DimensionRightOffset = 34
  DimensionTopOffset = 28
  Font = DejaVu Sans
  FontSize = 3
  LineEndSymbol = 0
  LineMidPointSymbol = 1
  LineStartSymbol = 3
  LineStyle = 0
  LockPosition = false
  MultiRebar_LineEndSymbol = 0
  MultiRebar_LineStartSymbol = 0
  MultiRebar_OuterDimension = true
  MultiRebar_TextPositionType = 0
  ParentDrawingView = -> ReinforcementDrawingView005
  Rebar = -> Rebar010
  Rotation = 0
  Scale = 0.116818
  ScaleType = 2
  SingleRebar_LineEndSymbol = 0
  SingleRebar_LineStartSymbol = 3
  SingleRebar_OuterDimension = false
  SingleRebar_TextPositionType = 1
  StrokeWidth = 0.25
  Symbol = <svg version="1.1" xmlns="http://www.w3.org/2000/svg" xmlns:xlink="http://www.w3.org/1999/xlink" xmlns:freecad="http://www.freecadweb.org/wiki/index.php?title=Svg_Namespace" width="2200.0mm" height="400.0mm" viewBox="0 0 2200.0 400.0"><g transform="translate(100.00000000000023, 200.0)"><g><path d="M20.0 -439.6887159533074 L20.0 -164.0" style="stroke:#00007f;stroke-width:2.140077821011673;stroke-linecap:round;fill:none;" stroke-dasharray="" /><g id="line_mid_points" /><path d="M0,0 -8,-1.5 V1.5 L0,0" style="stroke:#00007f;fill:#00007f;stroke-width:2.140077821011673;stroke-linecap:round;stroke-linejoin:bevel;" transform="translate(20.0 -164.0) rotate(90.0 0 0)" /></g><text x="20.0" y="-439.6887159533074" style="white-space:pre;" fill="#005400" font-family="DejaVu Sans" font-size="25.68093385214008" text-anchor="middle" dominant-baseline="baseline" xml:space="preserve">LLRb 1⌀16,span=0</text></g></svg>
  TextPositionType = 0
  WayPoints = (2) [(0,0,0),(50,0,0)]
  WayPointsType = 0
  X = 148.5
  Y = 105
FEATURE [TechDraw::DrawViewSymbolPython] ReinforcementDimensioning080  # drawing view (typed FeaturePython)
  DimensionBottomOffset = 28
  DimensionFormat = %M %C⌀%D,span=%S
  DimensionLeftOffset = 10
  DimensionRightOffset = 34
  DimensionTopOffset = 34
  Font = DejaVu Sans
  FontSize = 3
  LineEndSymbol = 0
  LineMidPointSymbol = 1
  LineStartSymbol = 3
  LineStyle = 0
  LockPosition = false
  MultiRebar_LineEndSymbol = 0
  MultiRebar_LineStartSymbol = 0
  MultiRebar_OuterDimension = true
  MultiRebar_TextPositionType = 0
  ParentDrawingView = -> ReinforcementDrawingView005
  Rebar = -> Rebar012
  Rotation = 0
  Scale = 0.116818
  ScaleType = 2
  SingleRebar_LineEndSymbol = 0
  SingleRebar_LineStartSymbol = 3
  SingleRebar_OuterDimension = false
  SingleRebar_TextPositionType = 1
  StrokeWidth = 0.25
  Symbol = <svg version="1.1" xmlns="http://www.w3.org/2000/svg" xmlns:xlink="http://www.w3.org/1999/xlink" xmlns:freecad="http://www.freecadweb.org/wiki/index.php?title=Svg_Namespace" width="2200.0mm" height="400.0mm" viewBox="0 0 2200.0 400.0"><g transform="translate(100.00000000000023, 200.0)"><g><path d="M1836.0 439.6887159533074 L1836.0 164.0" style="stroke:#00007f;stroke-width:2.140077821011673;stroke-linecap:round;fill:none;" stroke-dasharray="" /><g id="line_mid_points" /><path d="M0,0 -8,-1.5 V1.5 L0,0" style="stroke:#00007f;fill:#00007f;stroke-width:2.140077821011673;stroke-linecap:round;stroke-linejoin:bevel;" transform="translate(1836.0 164.0) rotate(-90.0 0 0)" /></g><text x="1836.0" y="452.52918287937746" style="white-space:pre;" fill="#005400" font-family="DejaVu Sans" font-size="25.68093385214008" text-anchor="middle" dominant-baseline="baseline" xml:space="preserve">RLRb 1⌀16,span=0</text></g></svg>
  TextPositionType = 0
  WayPoints = (2) [(0,0,0),(50,0,0)]
  WayPointsType = 0
  X = 148.5
  Y = 105
FEATURE [TechDraw::DrawViewSymbolPython] ReinforcementDimensioning081  # drawing view (typed FeaturePython)
  DimensionBottomOffset = 34
  DimensionFormat = %M %C⌀%D,span=%S
  DimensionLeftOffset = 10
  DimensionRightOffset = 34
  DimensionTopOffset = 34
  Font = DejaVu Sans
  FontSize = 3
  LineEndSymbol = 0
  LineMidPointSymbol = 1
  LineStartSymbol = 3
  LineStyle = 0
  LockPosition = false
  MultiRebar_LineEndSymbol = 0
  MultiRebar_LineStartSymbol = 0
  MultiRebar_OuterDimension = true
  MultiRebar_TextPositionType = 0
  ParentDrawingView = -> ReinforcementDrawingView005
  Rebar = -> Rebar013
  Rotation = 0
  Scale = 0.116818
  ScaleType = 2
  SingleRebar_LineEndSymbol = 0
  SingleRebar_LineStartSymbol = 3
  SingleRebar_OuterDimension = false
  SingleRebar_TextPositionType = 1
  StrokeWidth = 0.25
  Symbol = <svg version="1.1" xmlns="http://www.w3.org/2000/svg" xmlns:xlink="http://www.w3.org/1999/xlink" xmlns:freecad="http://www.freecadweb.org/wiki/index.php?title=Svg_Namespace" width="2200.0mm" height="400.0mm" viewBox="0 0 2200.0 400.0"><g transform="translate(100.00000000000023, 200.0)"><g><path d="M647.0 491.05058365758754 L647.0 164.0" style="stroke:#00007f;stroke-width:2.140077821011673;stroke-linecap:round;fill:none;" stroke-dasharray="" /><g id="line_mid_points" /><path d="M0,0 -8,-1.5 V1.5 L0,0" style="stroke:#00007f;fill:#00007f;stroke-width:2.140077821011673;stroke-linecap:round;stroke-linejoin:bevel;" transform="translate(647.0 164.0) rotate(-90.0 0 0)" /></g><text x="647.0" y="503.8910505836576" style="white-space:pre;" fill="#005400" font-family="DejaVu Sans" font-size="25.68093385214008" text-anchor="middle" dominant-baseline="baseline" xml:space="preserve">RLRb 1⌀16,span=0</text></g></svg>
  TextPositionType = 0
  WayPoints = (2) [(0,0,0),(50,0,0)]
  WayPointsType = 0
  X = 148.5
  Y = 105
FEATURE [TechDraw::DrawPage] TechDraw__DrawPage005  label="Beam Drawing005"
  KeepUpdated = true
  NextBalloonIndex = 1
  ProjectionType = 0
  Template = -> Template005
  Views = -> [ReinforcementDrawingView005,ReinforcementDimensioning069,ReinforcementDimensioning070,ReinforcementDimensioning071,ReinforcementDimensioning072,ReinforcementDimensioning073,ReinforcementDimensioning074,ReinforcementDimensioning075,ReinforcementDimensioning076,ReinforcementDimensioning077,ReinforcementDimensioning078,ReinforcementDimensioning079,ReinforcementDimensioning080,+1 more]
